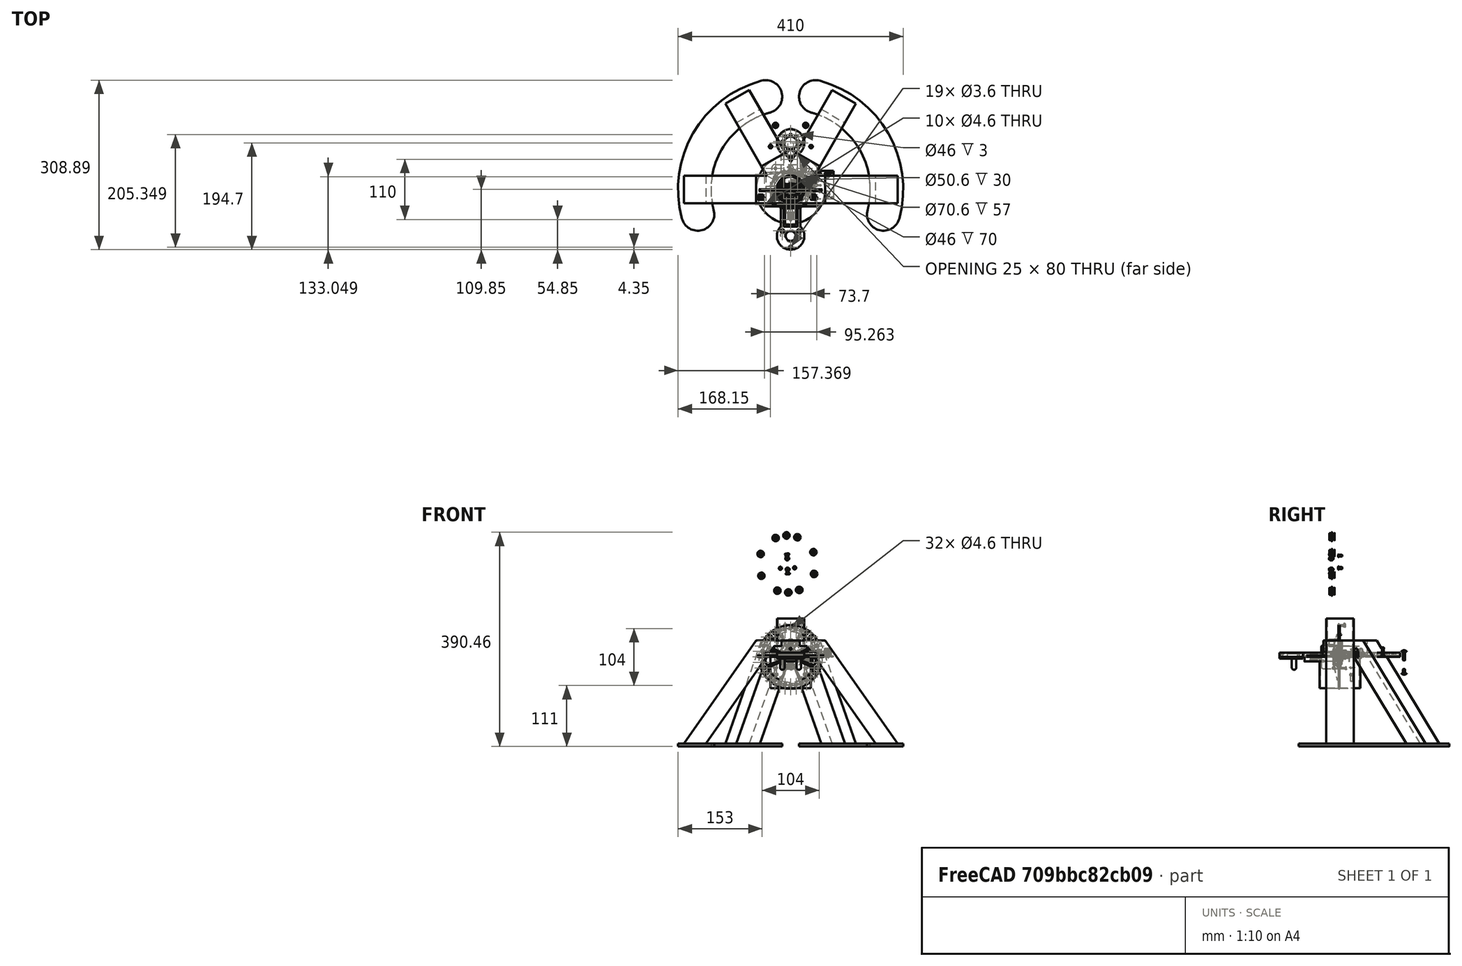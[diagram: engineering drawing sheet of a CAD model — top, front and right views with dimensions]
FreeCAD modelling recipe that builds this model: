
FCSTD DOCUMENT  (FreeCAD 1.1R44227 +568 (Git))
Label: assembly_Pendulum
License: All rights reserved
LicenseURL: https://en.wikipedia.org/wiki/All_rights_reserved
objects: Part::Feature×169, App::Point×115, App::Part×100, Sketcher::SketchObject×56, Part::FeaturePython×51, PartDesign::Pad×36, PartDesign::CoordinateSystem×29, PartDesign::Pocket×18, App::Link×17, PartDesign::Body×15, Mesh::Feature×9, PartDesign::Fillet×8, PartDesign::PolarPattern×7, App::DocumentObjectGroup×5, PartDesign::Chamfer×4, App::FeaturePython×1, PartDesign::Revolution×1, PartDesign::Hole×1
note: 594 computed .brp shape members not serialized (recipe doc carries the construction recipe); baked Part::Feature solids carry a one-line shape summary decoded from their .brp

FEATURE [PartDesign::CoordinateSystem] LCS_Origin
  AttacherType = Attacher::AttachEngine3D
  AttachmentSupport = -> [X_Axis]
  MapMode = 2
FEATURE [App::DocumentObjectGroup] Constraints
FEATURE [App::FeaturePython] Variables  # WARN: FeaturePython — macro-defined, semantics opaque (R4)
  Type = App::PropertyContainer
  arm_rotation = 2
FEATURE [App::DocumentObjectGroup] Configurations
FEATURE [Sketcher::SketchObject] Sketch
  ArcFitTolerance = 1e-06
  AttachmentSupport = -> [XZ_Plane001]
  ExternalTypes = [0]
  FullyConstrained = true
  MakeInternals = false
  MapMode = 5
  Placement = pos=(0,0,0) rot=(1,0,0;1.5708rad)
  _ExternalGeoVersion = 0
  sketch-geometry (13):
    g0: LineSegment StartX=5.6759 StartY=30.0968 StartZ=0 EndX=23.0689 EndY=6 EndZ=0
    g1: LineSegment StartX=23.0689 StartY=6 StartZ=0 EndX=34 EndY=6 EndZ=0
    g2: LineSegment StartX=34 StartY=6 StartZ=0 EndX=34 EndY=0 EndZ=0
    g3: LineSegment StartX=34 StartY=0 StartZ=0 EndX=20 EndY=0 EndZ=0
    g4: LineSegment StartX=20 StartY=0 StartZ=0 EndX=4.86567 EndY=20.9676 EndZ=0
    g5: LineSegment StartX=-4.86567 StartY=20.9676 StartZ=0 EndX=-20 EndY=0 EndZ=0
    g6: LineSegment StartX=-20 StartY=0 StartZ=0 EndX=-34 EndY=0 EndZ=0
    g7: LineSegment StartX=-34 StartY=0 StartZ=0 EndX=-34 EndY=6 EndZ=0
    g8: LineSegment StartX=-34 StartY=6 StartZ=0 EndX=-23.0689 EndY=6 EndZ=0
    g9: LineSegment StartX=-23.0689 StartY=6 StartZ=0 EndX=-5.6759 EndY=30.0968 EndZ=0
    g10: Circle CenterX=-1e-16 CenterY=26 CenterZ=0 NormalX=0 NormalY=0 NormalZ=1 AngleXU=0 Radius=2.8
    g11: ArcOfCircle CenterX=-1e-16 CenterY=26 CenterZ=0 NormalX=0 NormalY=0 NormalZ=1 AngleXU=0 Radius=7 StartAngle=0.625205 EndAngle=2.51639
    g12: ArcOfCircle CenterX=-1e-16 CenterY=26 CenterZ=0 NormalX=0 NormalY=0 NormalZ=1 AngleXU=0 Radius=7 StartAngle=3.94384 EndAngle=5.48094
  constraints (36):
    c: Coincident(g0,g1)
    c: Horizontal(g1)
    c: Coincident(g1,g2)
    c: PointOnObject(g2,g-1)
    c: Coincident(g2,g3)
    c: PointOnObject(g3,g-1)
    c: Coincident(g3,g4)
    c: Coincident(g5,g6)
    c: PointOnObject(g6,g-1)
    c: Coincident(g6,g7)
    c: Vertical(g7)
    c: Coincident(g7,g8)
    c: Horizontal(g8)
    c: Coincident(g8,g9)
    c: Symmetric(g9,g0,g-2)
    c: Parallel(g9,g5)
    c: Parallel(g0,g4)
    c: Vertical(g2)
    c: Equal(g7,g2)
    c: DistanceY(g7,g7) = 6
    c: Equal(g8,g1)
    c: DistanceX(g6,g6) = 14
    c: DistanceX(g5,g3) = 40
    c: Diameter(g10) = 5.6
    c: Coincident(g11,g10)
    c: Coincident(g11,g0)
    c: Equal(g11,g12)
    c: Coincident(g11,g12)
    c: Coincident(g4,g12)
    c: Coincident(g5,g12)
    c: DistanceY(g-1,g10) = 26
    c: Distance(g5,g9) = 6
    c: Distance(g4,g0) = 6
    c: Tangent(g9,g11) = 1.5708
    c: Diameter(g11) = 14
    c: Symmetric(g5,g3,g-2)
FEATURE [PartDesign::Pad] Pad  label="Pad_Main"
  Direction = (0,-1,2e-16)
  Length = 10
  Length2 = 10
  Placement = pos=(0,0,0) rot=(1,0,0;1.5708rad)
  Profile = -> Sketch
  ReferenceAxis = -> Sketch [N_Axis]
  Refine = true
  SideType = 0
  Suppressed = false
  Type = 0
  Type2 = 0
FEATURE [Sketcher::SketchObject] Sketch001
  ArcFitTolerance = 1e-06
  AttachmentSupport = -> [Pad]
  ExternalGeometry = -> [Pad]
  ExternalTypes = [0]
  FullyConstrained = true
  MakeInternals = false
  MapMode = 5
  Placement = pos=(0,-10,0) rot=(1,0,0;1.5708rad)
  _ExternalGeoVersion = 0
  sketch-geometry (2):
    g0: Circle CenterX=0 CenterY=26 CenterZ=0 NormalX=0 NormalY=0 NormalZ=1 AngleXU=0 Radius=3.8
    g1: Circle CenterX=0 CenterY=26 CenterZ=0 NormalX=0 NormalY=0 NormalZ=1 AngleXU=0 Radius=2.8
  constraints (4):
    c: Coincident(g0,g-3)
    c: Coincident(g1,g0)
    c: Diameter(g1) = 5.6
    c: Diameter(g0) = 7.6
FEATURE [PartDesign::Pad] Pad001  label="Pad_Shaft"
  BaseFeature = -> Pad
  Direction = (0,-1,2e-16)
  Length = 16.6
  Length2 = 10
  Placement = pos=(0,0,0) rot=(1,0,0;1.5708rad)
  Profile = -> Sketch001
  ReferenceAxis = -> Sketch001 [N_Axis]
  Refine = true
  SideType = 0
  Suppressed = false
  Type = 0
  Type2 = 0
FEATURE [Sketcher::SketchObject] Sketch002
  ArcFitTolerance = 1e-06
  AttachmentSupport = -> [Pad001]
  ExternalGeometry = -> [Pad001]
  ExternalTypes = [0]
  FullyConstrained = true
  MakeInternals = false
  MapMode = 5
  Placement = pos=(0,-10,0) rot=(1,0,0;1.5708rad)
  _ExternalGeoVersion = 0
  sketch-geometry (2):
    g0: Circle CenterX=0 CenterY=26 CenterZ=0 NormalX=0 NormalY=0 NormalZ=1 AngleXU=0 Radius=3.8
    g1: Circle CenterX=0 CenterY=26 CenterZ=0 NormalX=0 NormalY=0 NormalZ=1 AngleXU=0 Radius=6.5
  constraints (4):
    c: Coincident(g0,g-3)
    c: Equal(g0,g-3)
    c: Coincident(g1,g0)
    c: Diameter(g1) = 13
FEATURE [PartDesign::Pad] Pad002  label="Pad_Thrust"
  BaseFeature = -> Pad001
  Direction = (0,-1,2e-16)
  Length = 10
  Length2 = 10
  Placement = pos=(0,0,0) rot=(1,0,0;1.5708rad)
  Profile = -> Sketch002
  ReferenceAxis = -> Sketch002 [N_Axis]
  Refine = true
  SideType = 0
  Suppressed = false
  Type = 0
  Type2 = 0
FEATURE [Sketcher::SketchObject] Sketch003
  ArcFitTolerance = 1e-06
  AttachmentSupport = -> [Pad002]
  ExternalTypes = [0]
  FullyConstrained = true
  MakeInternals = false
  MapMode = 5
  Placement = pos=(0,2.9e-15,0) rot=(-1,0,0;1.5708rad)
  _ExternalGeoVersion = 0
  sketch-geometry (7):
    g0: LineSegment StartX=-4.8 StartY=-26 StartZ=0 EndX=-2.4 EndY=-30.1569 EndZ=0
    g1: LineSegment StartX=-2.4 StartY=-30.1569 StartZ=0 EndX=2.4 EndY=-30.1569 EndZ=0
    g2: LineSegment StartX=2.4 StartY=-30.1569 StartZ=0 EndX=4.8 EndY=-26 EndZ=0
    g3: LineSegment StartX=4.8 StartY=-26 StartZ=0 EndX=2.4 EndY=-21.8431 EndZ=0
    g4: LineSegment StartX=2.4 StartY=-21.8431 StartZ=0 EndX=-2.4 EndY=-21.8431 EndZ=0
    g5: LineSegment StartX=-2.4 StartY=-21.8431 StartZ=0 EndX=-4.8 EndY=-26 EndZ=0
    g6: Circle [constr] CenterX=0 CenterY=-26 CenterZ=0 NormalX=0 NormalY=0 NormalZ=1 AngleXU=0 Radius=4.8
  constraints (16):
    c: Coincident(g0,g1)
    c: Coincident(g1,g2)
    c: Coincident(g2,g3)
    c: Coincident(g3,g4)
    c: Coincident(g4,g5)
    c: Coincident(g5,g0)
    c: Equal(g0, g1-g5) x5
    c: PointOnObject(g0,g6)
    c: PointOnObject(g1,g6)
    c: PointOnObject(g2,g6)
    c: PointOnObject(g3,g6)
    c: PointOnObject(g4,g6)
    c: PointOnObject(g5,g6)
    c: Coincident(g6,g-3)
    c: Horizontal(g4)
    c: Diameter(g6) = 9.6
FEATURE [PartDesign::Pocket] Pocket
  BaseFeature = -> Pad002
  Direction = (0,-1,-2e-16)
  Length = 3
  Length2 = 5
  Placement = pos=(0,0,0) rot=(1,0,0;1.5708rad)
  Profile = -> Sketch003
  ReferenceAxis = -> Sketch003 [N_Axis]
  Refine = true
  SideType = 0
  Suppressed = false
  Type = 0
  Type2 = 0
FEATURE [Sketcher::SketchObject] Sketch005  label="Sketch_section"
  ArcFitTolerance = 0
  AttachmentSupport = -> [XZ_Plane003]
  ExternalTypes = [0]
  FullyConstrained = true
  MakeInternals = false
  MapMode = 5
  Placement = pos=(0,0,0) rot=(1,0,0;1.5708rad)
  _ExternalGeoVersion = 0
  sketch-geometry (12):
    g0: LineSegment StartX=4 StartY=-3.5 StartZ=0 EndX=6.5 EndY=-3.5 EndZ=0
    g1: LineSegment StartX=11 StartY=-3.5 StartZ=0 EndX=11 EndY=3.5 EndZ=0
    g2: LineSegment StartX=11 StartY=3.5 StartZ=0 EndX=9.25 EndY=3.5 EndZ=0
    g3: LineSegment StartX=4 StartY=3.5 StartZ=0 EndX=4 EndY=-3.5 EndZ=0
    g4: LineSegment StartX=6.5 StartY=3.5 StartZ=0 EndX=6.75 EndY=3.25 EndZ=0
    g5: LineSegment StartX=6.75 StartY=3.25 StartZ=0 EndX=9 EndY=3.25 EndZ=0
    g6: LineSegment StartX=9 StartY=3.25 StartZ=0 EndX=9.25 EndY=3.5 EndZ=0
    g7: LineSegment StartX=6.5 StartY=-3.5 StartZ=0 EndX=6.75 EndY=-3.25 EndZ=0
    g8: LineSegment StartX=6.75 StartY=-3.25 StartZ=0 EndX=9 EndY=-3.25 EndZ=0
    g9: LineSegment StartX=9 StartY=-3.25 StartZ=0 EndX=9.25 EndY=-3.5 EndZ=0
    g10: LineSegment StartX=6.5 StartY=3.5 StartZ=0 EndX=4 EndY=3.5 EndZ=0
    g11: LineSegment StartX=9.25 StartY=-3.5 StartZ=0 EndX=11 EndY=-3.5 EndZ=0
  constraints (33):
    c: Coincident(g11,g1)
    c: Coincident(g1,g2)
    c: Coincident(g10,g3)
    c: Coincident(g3,g0)
    c: Horizontal(g0)
    c: Horizontal(g2)
    c: Vertical(g1)
    c: DistanceY(g1) = 7
    c: DistanceX(g0) = 4
    c: DistanceX(g11) = 11
    c: Coincident(g4,g5)
    c: Horizontal(g5)
    c: Coincident(g5,g6)
    c: Coincident(g7,g8)
    c: Horizontal(g8)
    c: Coincident(g8,g9)
    c: Coincident(g2,g6)
    c: Coincident(g10,g4)
    c: Tangent(g2,g10)
    c: Coincident(g0,g7)
    c: Coincident(g11,g9)
    c: Tangent(g0,g11)
    c: Equal(g4,g6)
    c: Equal(g6,g7)
    c: Angle(g10,g4) = 2.35619
    c: DistanceX(g2) = -1.75
    c: DistanceX(g10) = -2.5
    c: Equal(g0,g10)
    c: Equal(g11,g2)
    c: Equal(g9,g7)
    c: Parallel(g9,g4)
    c: DistanceY(g5,g1) = 0.25
    c: Symmetric(g0,g3,g-1)
FEATURE [PartDesign::Revolution] Revolution
  Angle = 360
  Angle2 = 60
  Axis = (0,2e-16,1)
  Base = (0,0,0)
  FuseOrder = 1
  Placement = pos=(0,0,0) rot=(1,0,0;1.5708rad)
  Profile = -> Sketch005
  ReferenceAxis = -> Sketch005 [V_Axis]
  Refine = true
  Suppressed = false
  Type = 0
FEATURE [PartDesign::Chamfer] Chamfer
  Angle = 45
  Base = -> Revolution [Edge12,Edge11]
  BaseFeature = -> Revolution
  ChamferType = 0
  FlipDirection = false
  Placement = pos=(0,0,0) rot=(1,0,0;1.5708rad)
  Refine = true
  Size = 0.25
  Size2 = 1
  SupportTransform = false
  Suppressed = false
  UseAllEdges = false
FEATURE [PartDesign::CoordinateSystem] Bearing_Axis
  AttacherType = Attacher::AttachEngine3D
  AttachmentSupport = -> [Chamfer]
  MapMode = 45
  Placement = pos=(1.89e-14,1.7e-15,3.5) rot=(0,0,1;0rad)
FEATURE [PartDesign::Body] Body002  label="Body_Bearing"
  AllowCompound = false
  Group = -> [Sketch005,Revolution,Chamfer,Bearing_Axis]
  Origin = -> Origin003
  Tip = -> Chamfer
FEATURE [Sketcher::SketchObject] Sketch006
  ArcFitTolerance = 1e-06
  AttachmentSupport = -> [XY_Plane004]
  ExternalTypes = [0]
  FullyConstrained = true
  MakeInternals = false
  MapMode = 5
  _ExternalGeoVersion = 0
  sketch-geometry (1):
    g0: Circle CenterX=0 CenterY=84.85 CenterZ=0 NormalX=0 NormalY=0 NormalZ=1 AngleXU=0 Radius=23
  constraints (3):
    c: PointOnObject(g0,g-2)
    c: DistanceY(g-1,g0) = 84.85
    c: Diameter(g0) = 46
FEATURE [Sketcher::SketchObject] Sketch007
  ArcFitTolerance = 1e-06
  AttachmentSupport = -> [XY_Plane004]
  ExternalTypes = [0]
  FullyConstrained = true
  MakeInternals = false
  MapMode = 5
  _ExternalGeoVersion = 0
  sketch-geometry (33):
    g0: LineSegment StartX=-18 StartY=67.5 StartZ=0 EndX=-18 EndY=-67.5 EndZ=0
    g1: LineSegment StartX=18 StartY=-67.5 StartZ=0 EndX=18 EndY=67.5 EndZ=0
    g2: ArcOfCircle CenterX=0 CenterY=84.8494 CenterZ=0 NormalX=0 NormalY=0 NormalZ=1 AngleXU=0 Radius=25 StartAngle=5.51619 EndAngle=10.1918
    g3: Circle CenterX=0 CenterY=84.8494 CenterZ=0 NormalX=0 NormalY=0 NormalZ=1 AngleXU=0 Radius=11.5
    g4: Circle CenterX=0 CenterY=99.8494 CenterZ=0 NormalX=0 NormalY=0 NormalZ=1 AngleXU=0 Radius=1.8
    g5: Circle CenterX=9.64181 CenterY=96.34 CenterZ=0 NormalX=0 NormalY=0 NormalZ=1 AngleXU=0 Radius=1.8
    g6: Circle CenterX=14.7721 CenterY=87.4541 CenterZ=0 NormalX=0 NormalY=0 NormalZ=1 AngleXU=0 Radius=1.8
    g7: Circle CenterX=12.9904 CenterY=77.3494 CenterZ=0 NormalX=0 NormalY=0 NormalZ=1 AngleXU=0 Radius=1.8
    g8: Circle CenterX=5.1303 CenterY=70.754 CenterZ=0 NormalX=0 NormalY=0 NormalZ=1 AngleXU=0 Radius=1.8
    g9: Circle CenterX=-5.1303 CenterY=70.754 CenterZ=0 NormalX=0 NormalY=0 NormalZ=1 AngleXU=0 Radius=1.8
    g10: Circle CenterX=-12.9904 CenterY=77.3494 CenterZ=0 NormalX=0 NormalY=0 NormalZ=1 AngleXU=0 Radius=1.8
    g11: Circle CenterX=-14.7721 CenterY=87.4541 CenterZ=0 NormalX=0 NormalY=0 NormalZ=1 AngleXU=0 Radius=1.8
    g12: Circle CenterX=-9.64181 CenterY=96.34 CenterZ=0 NormalX=0 NormalY=0 NormalZ=1 AngleXU=0 Radius=1.8
    g13: LineSegment [constr] StartX=-9.64181 StartY=96.34 StartZ=0 EndX=0 EndY=84.8494 EndZ=0
    g14: LineSegment [constr] StartX=-14.7721 StartY=87.4541 StartZ=0 EndX=0 EndY=84.8494 EndZ=0
    g15: LineSegment [constr] StartX=-12.9904 StartY=77.3494 StartZ=0 EndX=0 EndY=84.8494 EndZ=0
    g16: LineSegment [constr] StartX=-5.1303 StartY=70.754 StartZ=0 EndX=0 EndY=84.8494 EndZ=0
    g17: LineSegment [constr] StartX=5.1303 StartY=70.754 StartZ=0 EndX=0 EndY=84.8494 EndZ=0
    g18: LineSegment [constr] StartX=12.9904 StartY=77.3494 StartZ=0 EndX=0 EndY=84.8494 EndZ=0
    g19: LineSegment [constr] StartX=14.7721 StartY=87.4541 StartZ=0 EndX=0 EndY=84.8494 EndZ=0
    g20: LineSegment [constr] StartX=9.64181 StartY=96.34 StartZ=0 EndX=0 EndY=84.8494 EndZ=0
    g21: Circle CenterX=-7.78 CenterY=-27 CenterZ=0 NormalX=0 NormalY=0 NormalZ=1 AngleXU=0 Radius=1.8
    g22: Circle CenterX=7.78 CenterY=-27 CenterZ=0 NormalX=0 NormalY=0 NormalZ=1 AngleXU=0 Radius=1.8
    g23: ArcOfCircle CenterX=0 CenterY=-84.8494 CenterZ=0 NormalX=0 NormalY=0 NormalZ=1 AngleXU=0 Radius=25 StartAngle=2.3746 EndAngle=7.05018
    g24: Circle CenterX=0 CenterY=-84.8494 CenterZ=0 NormalX=0 NormalY=0 NormalZ=1 AngleXU=0 Radius=11.25
    g25: LineSegment StartX=-12.5 StartY=63.1987 StartZ=0 EndX=-12.5 EndY=-16.8013 EndZ=0
    g26: LineSegment StartX=-12.5 StartY=-16.8013 StartZ=0 EndX=12.5 EndY=-16.8013 EndZ=0
    g27: LineSegment StartX=12.5 StartY=-16.8013 StartZ=0 EndX=12.5 EndY=63.1987 EndZ=0
    g28: LineSegment StartX=-12.5 StartY=-33.5 StartZ=0 EndX=-12.5 EndY=-67.5 EndZ=0
    g29: LineSegment StartX=-12.5 StartY=-67.5 StartZ=0 EndX=12.5 EndY=-67.5 EndZ=0
    g30: LineSegment StartX=12.5 StartY=-67.5 StartZ=0 EndX=12.5 EndY=-33.5 EndZ=0
    g31: LineSegment StartX=12.5 StartY=-33.5 StartZ=0 EndX=-12.5 EndY=-33.5 EndZ=0
    g32: ArcOfCircle CenterX=0 CenterY=84.8494 CenterZ=0 NormalX=0 NormalY=0 NormalZ=1 AngleXU=0 Radius=25 StartAngle=4.18879 EndAngle=5.23599
  constraints (88):
    c: Vertical(g0)
    c: Vertical(g1)
    c: Symmetric(g0,g1,g-1)
    c: DistanceX(g0,g1) = 36
    c: DistanceY(g1,g1) = 135
    c: PointOnObject(g2,g-2)
    c: Diameter(g2) = 50
    c: Coincident(g2,g0)
    c: Coincident(g2,g1)
    c: Coincident(g3,g2)
    c: Diameter(g3) = 23
    c: PointOnObject(g4,g-2)
    c: Coincident(g13,g12)
    c: Coincident(g13,g2)
    c: Coincident(g14,g11)
    c: Coincident(g14,g2)
    c: Coincident(g15,g10)
    c: Coincident(g15,g2)
    c: Coincident(g16,g9)
    c: Coincident(g16,g2)
    c: Coincident(g17,g8)
    c: Coincident(g17,g2)
    c: Coincident(g18,g7)
    c: Coincident(g18,g2)
    c: Coincident(g19,g6)
    c: Coincident(g19,g2)
    c: Coincident(g20,g5)
    c: Coincident(g20,g2)
    c: Equal(g4,g5)
    c: Equal(g5,g6)
    c: Equal(g6,g7)
    c: Equal(g7,g8)
    c: Equal(g8,g9)
    c: Equal(g9,g10)
    c: Equal(g10,g11)
    c: Equal(g11,g12)
    c: Equal(g13,g14)
    c: Equal(g14,g15)
    c: Equal(g15,g16)
    c: Equal(g16,g17)
    c: Equal(g17,g18)
    c: Equal(g18,g19)
    c: Equal(g19,g20)
    c: DistanceY(g2,g4) = 15
    c: Distance(g13) = 15
    c: Diameter(g4) = 3.6
    c: Angle(g-2,g20) = 2.44346
    c: Angle(g19,g20) = 0.698132
    c: Angle(g18,g19) = 0.698132
    c: Angle(g17,g18) = 0.698132
    c: Angle(g16,g17) = 0.698132
    c: Angle(g15,g16) = 0.698132
    c: Angle(g14,g15) = 0.698132
    c: Angle(g13,g14) = 0.698132
    c: Equal(g22,g21)
    c: Diameter(g21) = 3.6
    c: DistanceX(g21,g22) = 15.56
    c: Symmetric(g21,g22,g-2)
    c: DistanceY(g22,g-1) = 27
    c: PointOnObject(g23,g-2)
    c: Diameter(g23) = 50
    c: Coincident(g23,g1)
    c: Coincident(g23,g0)
    c: Coincident(g24,g23)
    c: Diameter(g24) = 22.5
    c: Vertical(g25)
    c: Vertical(g27)
    c: Horizontal(g26)
    c: Coincident(g28,g29)
    c: Coincident(g29,g30)
    c: Coincident(g30,g31)
    c: Coincident(g31,g28)
    c: Vertical(g28)
    c: Vertical(g30)
    c: Horizontal(g29)
    c: Symmetric(g27,g25,g-2)
    c: DistanceY(g25,g25) = 80
    c: DistanceX(g25,g27) = 25
    c: PointOnObject(g1,g29)
    c: Symmetric(g28,g30,g-2)
    c: DistanceX(g31,g31) = 25
    c: DistanceY(g28,g28) = 34
    c: Diameter(g32) = 50
    c: Coincident(g32,g25)
    c: Coincident(g32,g27)
    c: Coincident(g32,g2)
    c: Coincident(g26,g25)
    c: Coincident(g27,g26)
FEATURE [PartDesign::Pad] Pad004  label="Pad_Arm"
  Direction = (0,0,1)
  Length = 8
  Length2 = 10
  Profile = -> Sketch007
  ReferenceAxis = -> Sketch007 [N_Axis]
  Refine = true
  SideType = 0
  Suppressed = false
  Type = 0
  Type2 = 0
FEATURE [PartDesign::Pocket] Pocket001  label="Pocket_Motor"
  BaseFeature = -> Pad004
  Direction = (0,0,-1)
  Length = 3
  Length2 = 5
  Profile = -> Sketch006
  ReferenceAxis = -> Sketch006 [N_Axis]
  Refine = true
  Reversed = true
  SideType = 0
  Suppressed = false
  Type = 0
  Type2 = 0
FEATURE [PartDesign::CoordinateSystem] Arm_Axis_Top
  AttacherType = Attacher::AttachEngine3D
  AttachmentOffset = pos=(0,0,0) rot=(0,0,-1;1.5708rad)
  AttachmentSupport = -> [Pocket001]
  MapMode = 11
  Placement = pos=(2e-16,99.8494,8) rot=(0,0,1;0rad)
FEATURE [Sketcher::SketchObject] Sketch008
  ArcFitTolerance = 1e-06
  AttachmentSupport = -> [XZ_Plane005]
  ExternalTypes = [0]
  FullyConstrained = true
  MakeInternals = false
  MapMode = 5
  Placement = pos=(0,0,0) rot=(1,0,0;1.5708rad)
  _ExternalGeoVersion = 0
  sketch-geometry (8):
    g0: LineSegment StartX=-3.7 StartY=11.6 StartZ=0 EndX=-3.7 EndY=8 EndZ=0
    g1: LineSegment StartX=-3.7 StartY=8 StartZ=0 EndX=3.7 EndY=8 EndZ=0
    g2: LineSegment StartX=3.7 StartY=8 StartZ=0 EndX=3.7 EndY=11.6 EndZ=0
    g3: LineSegment StartX=3.7 StartY=11.6 StartZ=0 EndX=-3.7 EndY=11.6 EndZ=0
    g4: LineSegment StartX=-3.7 StartY=-8 StartZ=0 EndX=-3.7 EndY=-11.6 EndZ=0
    g5: LineSegment StartX=-3.7 StartY=-11.6 StartZ=0 EndX=3.7 EndY=-11.6 EndZ=0
    g6: LineSegment StartX=3.7 StartY=-11.6 StartZ=0 EndX=3.7 EndY=-8 EndZ=0
    g7: LineSegment StartX=3.7 StartY=-8 StartZ=0 EndX=-3.7 EndY=-8 EndZ=0
  constraints (21):
    c: Coincident(g0,g1)
    c: Coincident(g1,g2)
    c: Coincident(g2,g3)
    c: Coincident(g3,g0)
    c: Vertical(g0)
    c: Vertical(g2)
    c: Coincident(g4,g5)
    c: Coincident(g5,g6)
    c: Coincident(g6,g7)
    c: Coincident(g7,g4)
    c: Vertical(g4)
    c: Vertical(g6)
    c: Horizontal(g5)
    c: Horizontal(g7)
    c: Symmetric(g0,g6,g-1)
    c: DistanceY(g-1,g1) = 8
    c: DistanceY(g2,g2) = 3.6
    c: DistanceX(g3,g3) = 7.4
    c: Symmetric(g2,g4,g-1)
    c: Symmetric(g1,g0,g-2)
    c: Horizontal(g3)
FEATURE [Sketcher::SketchObject] Sketch009
  ArcFitTolerance = 1e-06
  AttachmentSupport = -> [XY_Plane005]
  ExternalTypes = [0]
  FullyConstrained = true
  MakeInternals = false
  MapMode = 5
  _ExternalGeoVersion = 0
  sketch-geometry (1):
    g0: Circle CenterX=0 CenterY=-6 CenterZ=0 NormalX=0 NormalY=0 NormalZ=1 AngleXU=0 Radius=2.25
  constraints (3):
    c: PointOnObject(g0,g-2)
    c: Diameter(g0) = 4.5
    c: DistanceY(g0,g-1) = 6
FEATURE [Sketcher::SketchObject] Sketch010
  ArcFitTolerance = 1e-06
  AttachmentOffset = pos=(0,0,0) rot=(1,0,0;0.392699rad)
  AttachmentSupport = -> [YZ_Plane005]
  ExternalTypes = [0]
  FullyConstrained = true
  MakeInternals = false
  MapMode = 5
  Placement = pos=(0,0,0) rot=(0.639338,0.639338,0.427192;2.33414rad)
  _ExternalGeoVersion = 0
  sketch-geometry (4):
    g0: LineSegment StartX=-3 StartY=14.5 StartZ=0 EndX=-12 EndY=14.5 EndZ=0
    g1: LineSegment StartX=-12 StartY=14.5 StartZ=0 EndX=-5 EndY=44.5 EndZ=0
    g2: LineSegment StartX=-5 StartY=44.5 StartZ=0 EndX=-3 EndY=44.5 EndZ=0
    g3: LineSegment StartX=-3 StartY=44.5 StartZ=0 EndX=-3 EndY=14.5 EndZ=0
  constraints (12):
    c: Coincident(g0,g1)
    c: Coincident(g1,g2)
    c: Horizontal(g2)
    c: Coincident(g2,g3)
    c: Coincident(g3,g0)
    c: Horizontal(g0)
    c: Vertical(g3)
    c: DistanceX(g0,g-1) = 3
    c: DistanceY(g-1,g0) = 14.5
    c: DistanceY(g3,g3) = 30
    c: DistanceX(g2,g2) = 2
    c: DistanceX(g0,g0) = 9
FEATURE [Sketcher::SketchObject] Sketch011
  ArcFitTolerance = 1e-06
  AttachmentSupport = -> [XZ_Plane005]
  ExternalTypes = [0]
  FullyConstrained = true
  MakeInternals = false
  MapMode = 5
  Placement = pos=(0,0,0) rot=(1,0,0;1.5708rad)
  _ExternalGeoVersion = 0
  sketch-geometry (1):
    g0: Circle CenterX=0 CenterY=52 CenterZ=0 NormalX=0 NormalY=0 NormalZ=1 AngleXU=0 Radius=2.3
  constraints (3):
    c: PointOnObject(g0,g-2)
    c: Diameter(g0) = 4.6
    c: DistanceY(g-1,g0) = 52
FEATURE [Sketcher::SketchObject] Sketch012
  ArcFitTolerance = 1e-06
  AttachmentSupport = -> [XZ_Plane005]
  ExternalTypes = [0]
  FullyConstrained = true
  MakeInternals = false
  MapMode = 5
  Placement = pos=(0,0,0) rot=(1,0,0;1.5708rad)
  _ExternalGeoVersion = 0
  sketch-geometry (5):
    g0: LineSegment StartX=0 StartY=0 StartZ=0 EndX=-1.04189 EndY=5.90885 EndZ=0
    g1: LineSegment StartX=-1.04189 StartY=5.90885 StartZ=0 EndX=-0.2 EndY=5.3692 EndZ=0
    g2: LineSegment StartX=-0.2 StartY=5.3692 StartZ=0 EndX=0.2 EndY=5.3692 EndZ=0
    g3: LineSegment StartX=0.2 StartY=5.3692 StartZ=0 EndX=1.04189 EndY=5.90885 EndZ=0
    g4: LineSegment StartX=1.04189 StartY=5.90885 StartZ=0 EndX=0 EndY=0 EndZ=0
  constraints (13):
    c: Coincident(g-1,g0)
    c: Coincident(g0,g1)
    c: Coincident(g1,g2)
    c: Horizontal(g2)
    c: Coincident(g2,g3)
    c: Coincident(g3,g4)
    c: Coincident(g4,g0)
    c: Symmetric(g3,g0,g-2)
    c: Angle(g4,g0) = 0.349066
    c: DistanceX(g2,g2) = 0.4
    c: Distance(g4) = 6
    c: Distance(g3) = 1
    c: Distance(g1) = 1
FEATURE [Sketcher::SketchObject] Sketch013
  ArcFitTolerance = 1e-06
  AttachmentSupport = -> [XZ_Plane005]
  ExternalTypes = [0]
  FullyConstrained = true
  MakeInternals = false
  MapMode = 5
  Placement = pos=(0,0,0) rot=(1,0,0;1.5708rad)
  _ExternalGeoVersion = 0
  sketch-geometry (2):
    g0: Circle CenterX=0 CenterY=0 CenterZ=0 NormalX=0 NormalY=0 NormalZ=1 AngleXU=0 Radius=5
    g1: Circle CenterX=0 CenterY=0 CenterZ=0 NormalX=0 NormalY=0 NormalZ=1 AngleXU=0 Radius=15
  constraints (4):
    c: Coincident(g0,g-1)
    c: Coincident(g1,g0)
    c: Diameter(g1) = 30
    c: Diameter(g0) = 10
FEATURE [Sketcher::SketchObject] Sketch014
  ArcFitTolerance = 1e-06
  AttachmentSupport = -> [XZ_Plane005]
  ExternalTypes = [0]
  FullyConstrained = true
  MakeInternals = false
  MapMode = 5
  Placement = pos=(0,0,0) rot=(1,0,0;1.5708rad)
  _ExternalGeoVersion = 0
  sketch-geometry (6):
    g0: ArcOfCircle CenterX=0 CenterY=0 CenterZ=0 NormalX=0 NormalY=0 NormalZ=1 AngleXU=0 Radius=15 StartAngle=1.23918 EndAngle=1.90241
    g1: ArcOfCircle CenterX=0 CenterY=0 CenterZ=0 NormalX=0 NormalY=0 NormalZ=1 AngleXU=0 Radius=46 StartAngle=1.23918 EndAngle=1.90241
    g2: LineSegment [constr] StartX=0 StartY=0 StartZ=0 EndX=-19.5341 EndY=56.7311 EndZ=0
    g3: LineSegment [constr] StartX=0 StartY=0 StartZ=0 EndX=19.5341 EndY=56.7311 EndZ=0
    g4: LineSegment StartX=-4.88352 StartY=14.1828 StartZ=0 EndX=-14.9761 EndY=43.4939 EndZ=0
    g5: LineSegment StartX=14.9761 StartY=43.4939 StartZ=0 EndX=4.88352 EndY=14.1828 EndZ=0
  constraints (17):
    c: Coincident(g0,g-1)
    c: Coincident(g1,g0)
    c: Coincident(g2,g0)
    c: Coincident(g3,g0)
    c: Coincident(g4,g0)
    c: Coincident(g4,g1)
    c: Coincident(g5,g1)
    c: Coincident(g5,g0)
    c: Symmetric(g2,g3,g-2)
    c: Angle(g3,g2) = 0.663225
    c: PointOnObject(g0,g3)
    c: PointOnObject(g1,g3)
    c: PointOnObject(g0,g2)
    c: PointOnObject(g1,g2)
    c: Diameter(g1) = 92
    c: Diameter(g0) = 30
    c: Distance(g3) = 60
FEATURE [Sketcher::SketchObject] Sketch015
  ArcFitTolerance = 1e-06
  AttachmentSupport = -> [XZ_Plane005]
  ExternalTypes = [0]
  FullyConstrained = true
  MakeInternals = false
  MapMode = 5
  Placement = pos=(0,0,0) rot=(1,0,0;1.5708rad)
  _ExternalGeoVersion = 0
  sketch-geometry (2):
    g0: Circle CenterX=0 CenterY=0 CenterZ=0 NormalX=0 NormalY=0 NormalZ=1 AngleXU=0 Radius=58
    g1: Circle CenterX=0 CenterY=0 CenterZ=0 NormalX=0 NormalY=0 NormalZ=1 AngleXU=0 Radius=5
  constraints (4):
    c: Coincident(g0,g-1)
    c: Diameter(g0) = 116
    c: Coincident(g1,g0)
    c: Diameter(g1) = 10
FEATURE [PartDesign::Pad] Pad005  label="Pad_External"
  Direction = (0,-1,2e-16)
  Length = 3
  Length2 = 10
  Placement = pos=(0,0,0) rot=(1,0,0;1.5708rad)
  Profile = -> Sketch015
  ReferenceAxis = -> Sketch015 [N_Axis]
  Refine = true
  SideType = 0
  Suppressed = false
  Type = 0
  Type2 = 0
FEATURE [PartDesign::Pocket] Pocket002  label="Pocket_Gap"
  BaseFeature = -> Pad005
  Direction = (0,1,-2e-16)
  Length = 5
  Length2 = 5
  Placement = pos=(0,0,0) rot=(1,0,0;1.5708rad)
  Profile = -> Sketch014
  ReferenceAxis = -> Sketch014 [N_Axis]
  Refine = true
  Reversed = true
  SideType = 0
  Suppressed = false
  Type = 0
  Type2 = 0
FEATURE [PartDesign::PolarPattern] PolarPattern  label="PolarPattern_Gaps"
  Angle = 360
  Axis = -> Sketch014 [N_Axis]
  BaseFeature = -> Pocket002
  Mode = 0
  Occurrences = 8
  Offset = 120
  Originals = -> [Pocket002]
  Placement = pos=(0,0,0) rot=(1,0,0;1.5708rad)
  Refine = true
  SpacingPattern = [0]
  Spacings = [-1,-1,-1,-1,-1,-1,-1]
  Suppressed = false
  TransformMode = 0
FEATURE [PartDesign::Pad] Pad006  label="Pad_Center"
  BaseFeature = -> PolarPattern
  Direction = (0,-1,2e-16)
  Length = 12
  Length2 = 10
  Placement = pos=(0,0,0) rot=(1,0,0;1.5708rad)
  Profile = -> Sketch013
  ReferenceAxis = -> Sketch013 [N_Axis]
  Refine = true
  SideType = 0
  Suppressed = false
  Type = 0
  Type2 = 0
FEATURE [PartDesign::Pocket] Pocket003  label="Pocket_Shaft"
  BaseFeature = -> Pad006
  Direction = (0,1,-2e-16)
  Length = 5
  Length2 = 5
  Placement = pos=(0,0,0) rot=(1,0,0;1.5708rad)
  Profile = -> Sketch012
  ReferenceAxis = -> Sketch012 [N_Axis]
  Refine = true
  Reversed = true
  SideType = 0
  Suppressed = false
  Type = 1
  Type2 = 0
FEATURE [PartDesign::PolarPattern] PolarPattern001  label="PolarPattern_DriveShaft"
  Angle = 360
  Axis = -> Sketch012 [N_Axis]
  BaseFeature = -> Pocket003
  Mode = 0
  Occurrences = 18
  Offset = 120
  Originals = -> [Pocket003]
  Placement = pos=(0,0,0) rot=(1,0,0;1.5708rad)
  Refine = true
  SpacingPattern = [0]
  Spacings = [-1,-1,-1,-1,-1,-1,-1,-1,-1,-1,-1,-1,-1,-1,-1,-1,-1]
  Suppressed = false
  TransformMode = 0
FEATURE [PartDesign::Pocket] Pocket004  label="Pocket_Screw"
  BaseFeature = -> PolarPattern001
  Direction = (0,1,-2e-16)
  Length = 5
  Length2 = 5
  Placement = pos=(0,0,0) rot=(1,0,0;1.5708rad)
  Profile = -> Sketch011
  ReferenceAxis = -> Sketch011 [N_Axis]
  Refine = true
  Reversed = true
  SideType = 0
  Suppressed = false
  Type = 1
  Type2 = 0
FEATURE [PartDesign::PolarPattern] PolarPattern002  label="PolarPattern_Inertia"
  Angle = 360
  Axis = -> Sketch011 [N_Axis]
  BaseFeature = -> Pocket004
  Mode = 0
  Occurrences = 32
  Offset = 120
  Originals = -> [Pocket004]
  Placement = pos=(0,0,0) rot=(1,0,0;1.5708rad)
  Refine = true
  SpacingPattern = [0]
  Spacings = [-1,-1,-1,-1,-1,-1,-1,-1,-1,-1,-1,-1,-1,-1,-1,-1,-1,-1,-1,-1,-1,-1,-1,-1,-1,-1,-1,-1,-1,-1,-1]
  Suppressed = false
  TransformMode = 0
FEATURE [PartDesign::Pad] Pad007  label="Pad_Reinforcement"
  BaseFeature = -> PolarPattern002
  Direction = (0.92388,0,-0.382683)
  Length = 2
  Length2 = 10
  Placement = pos=(0,0,0) rot=(1,0,0;1.5708rad)
  Profile = -> Sketch010
  ReferenceAxis = -> Sketch010 [N_Axis]
  Refine = true
  SideType = 2
  Suppressed = false
  Type = 0
  Type2 = 0
FEATURE [PartDesign::PolarPattern] PolarPattern003  label="PolarPattern_Reinforcements"
  Angle = 360
  Axis = -> Y_Axis005
  BaseFeature = -> Pad007
  Mode = 0
  Occurrences = 8
  Offset = 120
  Originals = -> [Pad007]
  Placement = pos=(0,0,0) rot=(1,0,0;1.5708rad)
  Refine = true
  SpacingPattern = [0]
  Spacings = [-1,-1,-1,-1,-1,-1,-1]
  Suppressed = false
  TransformMode = 0
FEATURE [PartDesign::Pocket] Pocket005  label="Pocket_Fixation"
  BaseFeature = -> PolarPattern003
  Direction = (0,0,-1)
  Length = 30
  Length2 = 5
  Placement = pos=(0,0,0) rot=(1,0,0;1.5708rad)
  Profile = -> Sketch009
  ReferenceAxis = -> Sketch009 [N_Axis]
  Refine = true
  SideType = 2
  Suppressed = false
  Type = 0
  Type2 = 0
FEATURE [PartDesign::Pocket] Pocket006  label="Pocket_Bolts"
  BaseFeature = -> Pocket005
  Direction = (0,1,-2e-16)
  Length = 12
  Length2 = 5
  Placement = pos=(0,0,0) rot=(1,0,0;1.5708rad)
  Profile = -> Sketch008
  ReferenceAxis = -> Sketch008 [N_Axis]
  Refine = true
  Reversed = true
  SideType = 0
  Suppressed = false
  Type = 0
  Type2 = 0
FEATURE [Sketcher::SketchObject] Sketch016
  ArcFitTolerance = 1e-06
  AttachmentSupport = -> [XY_Plane006]
  ExternalTypes = [0]
  FullyConstrained = true
  MakeInternals = false
  MapMode = 5
  _ExternalGeoVersion = 0
  sketch-geometry (8):
    g0: LineSegment StartX=-7.5 StartY=-8 StartZ=0 EndX=-7.5 EndY=-13 EndZ=0
    g1: LineSegment StartX=7.5 StartY=-13 StartZ=0 EndX=7.5 EndY=-8 EndZ=0
    g2: LineSegment StartX=7.5 StartY=-8 StartZ=0 EndX=-7.5 EndY=-8 EndZ=0
    g3: LineSegment StartX=-10 StartY=-13 StartZ=0 EndX=-10 EndY=-14.2 EndZ=0
    g4: LineSegment StartX=-10 StartY=-14.2 StartZ=0 EndX=10 EndY=-14.2 EndZ=0
    g5: LineSegment StartX=10 StartY=-14.2 StartZ=0 EndX=10 EndY=-13 EndZ=0
    g6: LineSegment StartX=10 StartY=-13 StartZ=0 EndX=7.5 EndY=-13 EndZ=0
    g7: LineSegment StartX=-7.5 StartY=-13 StartZ=0 EndX=-10 EndY=-13 EndZ=0
  constraints (21):
    c: Coincident(g1,g2)
    c: Coincident(g2,g0)
    c: Vertical(g0)
    c: Coincident(g3,g4)
    c: Coincident(g4,g5)
    c: Coincident(g5,g6)
    c: Coincident(g7,g3)
    c: Vertical(g3)
    c: Vertical(g5)
    c: Horizontal(g6)
    c: Coincident(g6,g1)
    c: Coincident(g0,g7)
    c: Symmetric(g0,g1,g-2)
    c: Symmetric(g3,g4,g-2)
    c: Symmetric(g0,g1,g-2)
    c: DistanceX(g2,g2) = 15
    c: DistanceX(g4,g4) = 20
    c: DistanceY(g3,g3) = 1.2
    c: Horizontal(g7)
    c: DistanceY(g0,g0) = 5
    c: DistanceY(g0,g-1) = 8
FEATURE [Sketcher::SketchObject] Sketch017
  ArcFitTolerance = 1e-06
  AttachmentOffset = pos=(0,0,42) rot=(0,0,1;0rad)
  AttachmentSupport = -> [XZ_Plane006]
  ExternalTypes = [0]
  FullyConstrained = true
  MakeInternals = false
  MapMode = 5
  Placement = pos=(0,-42,9.3e-15) rot=(1,0,0;1.5708rad)
  _ExternalGeoVersion = 0
  sketch-geometry (5):
    g0: LineSegment StartX=-0.955065 StartY=5.41644 StartZ=0 EndX=0 EndY=0 EndZ=0
    g1: LineSegment StartX=0.955065 StartY=5.41644 StartZ=0 EndX=0 EndY=0 EndZ=0
    g2: LineSegment StartX=-0.955065 StartY=5.41644 StartZ=0 EndX=-0.2 EndY=4.76079 EndZ=0
    g3: LineSegment StartX=-0.2 StartY=4.76079 StartZ=0 EndX=0.2 EndY=4.76079 EndZ=0
    g4: LineSegment StartX=0.2 StartY=4.76079 StartZ=0 EndX=0.955065 EndY=5.41644 EndZ=0
  constraints (12):
    c: Coincident(g0,g-1)
    c: Coincident(g1,g0)
    c: Coincident(g3,g2)
    c: Coincident(g4,g3)
    c: Coincident(g4,g1)
    c: Symmetric(g3,g2,g-2)
    c: Coincident(g2,g0)
    c: Symmetric(g0,g1,g-2)
    c: Angle(g1,g0) = 0.349066
    c: DistanceX(g3,g3) = 0.4
    c: Distance(g1) = 5.5
    c: Distance(g4) = 1
FEATURE [Sketcher::SketchObject] Sketch018
  ArcFitTolerance = 1e-06
  AttachmentSupport = -> [XZ_Plane006]
  ExternalTypes = [0]
  FullyConstrained = true
  MakeInternals = false
  MapMode = 5
  Placement = pos=(0,0,0) rot=(1,0,0;1.5708rad)
  _ExternalGeoVersion = 0
  sketch-geometry (1):
    g0: Circle CenterX=0 CenterY=0 CenterZ=0 NormalX=0 NormalY=0 NormalZ=1 AngleXU=0 Radius=21
  constraints (2):
    c: Coincident(g0,g-1)
    c: Diameter(g0) = 42
FEATURE [PartDesign::Pad] Pad008  label="Pad_Cylinder"
  Direction = (0,-1,2e-16)
  Length = 34
  Length2 = 10
  Placement = pos=(0,0,0) rot=(1,0,0;1.5708rad)
  Profile = -> Sketch018
  ReferenceAxis = -> Sketch018 [N_Axis]
  Refine = true
  SideType = 0
  Suppressed = false
  Type = 0
  Type2 = 0
FEATURE [Sketcher::SketchObject] Sketch019
  ArcFitTolerance = 1e-06
  AttachmentSupport = -> [Pad008]
  ExternalTypes = [0]
  FullyConstrained = true
  MakeInternals = false
  MapMode = 5
  Placement = pos=(0,-34,0) rot=(1,0,0;1.5708rad)
  _ExternalGeoVersion = 0
  sketch-geometry (1):
    g0: Circle CenterX=0 CenterY=0 CenterZ=0 NormalX=0 NormalY=0 NormalZ=1 AngleXU=0 Radius=7.5
  constraints (2):
    c: Coincident(g0,g-1)
    c: Diameter(g0) = 15
FEATURE [PartDesign::Pad] Pad009  label="Pad_Bearing"
  BaseFeature = -> Pad008
  Direction = (0,-1,2e-16)
  Length = 1.2
  Length2 = 10
  Placement = pos=(0,0,0) rot=(1,0,0;1.5708rad)
  Profile = -> Sketch019
  ReferenceAxis = -> Sketch019 [N_Axis]
  Refine = true
  SideType = 0
  Suppressed = false
  Type = 0
  Type2 = 0
FEATURE [Sketcher::SketchObject] Sketch020
  ArcFitTolerance = 1e-06
  AttachmentSupport = -> [Pad009]
  ExternalTypes = [0]
  FullyConstrained = true
  MakeInternals = false
  MapMode = 5
  Placement = pos=(0,-35.2,0) rot=(1,0,0;1.5708rad)
  _ExternalGeoVersion = 0
  sketch-geometry (1):
    g0: Circle CenterX=0 CenterY=0 CenterZ=0 NormalX=0 NormalY=0 NormalZ=1 AngleXU=0 Radius=3
  constraints (2):
    c: Coincident(g0,g-1)
    c: Diameter(g0) = 6
FEATURE [PartDesign::Pad] Pad010  label="Pad_Drive_Shaft"
  BaseFeature = -> Pad009
  Direction = (0,-1,2e-16)
  Length = 6.4
  Length2 = 10
  Placement = pos=(0,0,0) rot=(1,0,0;1.5708rad)
  Profile = -> Sketch020
  ReferenceAxis = -> Sketch020 [N_Axis]
  Refine = true
  SideType = 0
  Suppressed = false
  Type = 0
  Type2 = 0
FEATURE [Sketcher::SketchObject] Sketch021
  ArcFitTolerance = 1e-06
  AttachmentSupport = -> [Pad010]
  ExternalTypes = [0]
  FullyConstrained = true
  MakeInternals = false
  MapMode = 5
  Placement = pos=(0,-41.6,0) rot=(1,0,0;1.5708rad)
  _ExternalGeoVersion = 0
  sketch-geometry (1):
    g0: Circle CenterX=0 CenterY=0 CenterZ=0 NormalX=0 NormalY=0 NormalZ=1 AngleXU=0 Radius=7.5
  constraints (2):
    c: Coincident(g0,g-1)
    c: Diameter(g0) = 15
FEATURE [PartDesign::Pad] Pad011  label="Pad_Thrust001"
  BaseFeature = -> Pad010
  Direction = (0,-1,2e-16)
  Length = 1.3
  Length2 = 10
  Placement = pos=(0,0,0) rot=(1,0,0;1.5708rad)
  Profile = -> Sketch021
  ReferenceAxis = -> Sketch021 [N_Axis]
  Refine = true
  SideType = 0
  Suppressed = false
  Type = 0
  Type2 = 0
FEATURE [PartDesign::Pad] Pad012  label="Pad_Tooth"
  BaseFeature = -> Pad011
  Direction = (0,-1,2e-16)
  Length = 12
  Length2 = 10
  Placement = pos=(0,0,0) rot=(1,0,0;1.5708rad)
  Profile = -> Sketch017
  ReferenceAxis = -> Sketch017 [N_Axis]
  Refine = true
  SideType = 0
  Suppressed = false
  Type = 0
  Type2 = 0
FEATURE [PartDesign::PolarPattern] PolarPattern004  label="PolarPattern_Shaft"
  Angle = 360
  Axis = -> Sketch017 [N_Axis]
  BaseFeature = -> Pad012
  Mode = 0
  Occurrences = 18
  Offset = 120
  Originals = -> [Pad012]
  Placement = pos=(0,0,0) rot=(1,0,0;1.5708rad)
  Refine = true
  SpacingPattern = [0]
  Spacings = [-1,-1,-1,-1,-1,-1,-1,-1,-1,-1,-1,-1,-1,-1,-1,-1,-1]
  Suppressed = false
  TransformMode = 0
FEATURE [Sketcher::SketchObject] Sketch022
  ArcFitTolerance = 1e-06
  AttachmentSupport = -> [PolarPattern004]
  ExternalTypes = [0]
  FullyConstrained = true
  MakeInternals = false
  MapMode = 5
  Placement = pos=(0,-34,0) rot=(1,0,0;1.5708rad)
  _ExternalGeoVersion = 0
  sketch-geometry (1):
    g0: Circle CenterX=0 CenterY=15 CenterZ=0 NormalX=0 NormalY=0 NormalZ=1 AngleXU=0 Radius=1.75
  constraints (3):
    c: PointOnObject(g0,g-2)
    c: Diameter(g0) = 3.5
    c: DistanceY(g-1,g0) = 15
FEATURE [PartDesign::Pocket] Pocket007  label="Pocket_Screw001"
  BaseFeature = -> PolarPattern004
  Direction = (0,1,-2e-16)
  Length = 5
  Length2 = 5
  Placement = pos=(0,0,0) rot=(1,0,0;1.5708rad)
  Profile = -> Sketch022
  ReferenceAxis = -> Sketch022 [N_Axis]
  Refine = true
  SideType = 0
  Suppressed = false
  Type = 0
  Type2 = 0
FEATURE [PartDesign::PolarPattern] PolarPattern005  label="PolarPattern_Fixations"
  Angle = 360
  Axis = -> Sketch022 [N_Axis]
  BaseFeature = -> Pocket007
  Mode = 0
  Occurrences = 3
  Offset = 120
  Originals = -> [Pocket007]
  Placement = pos=(0,0,0) rot=(1,0,0;1.5708rad)
  Refine = true
  SpacingPattern = [0]
  Spacings = [-1,-1]
  Suppressed = false
  TransformMode = 0
FEATURE [PartDesign::Pad] Pad013  label="Pad_Connector"
  BaseFeature = -> PolarPattern005
  Direction = (0,0,1)
  Length = 22
  Length2 = 10
  Placement = pos=(0,0,0) rot=(1,0,0;1.5708rad)
  Profile = -> Sketch016
  ReferenceAxis = -> Sketch016 [N_Axis]
  Refine = true
  Reversed = true
  SideType = 0
  Suppressed = false
  Type = 0
  Type2 = 0
FEATURE [Sketcher::SketchObject] Sketch023
  ArcFitTolerance = 1e-06
  AttachmentSupport = -> [Pad013]
  ExternalGeometry = -> [Pad013]
  ExternalTypes = [0]
  FullyConstrained = true
  MakeInternals = false
  MapMode = 5
  Placement = pos=(0,0,-22) rot=(1,0,0;3.14159rad)
  _ExternalGeoVersion = 0
  sketch-geometry (4):
    g0: LineSegment StartX=-6.5 StartY=12 StartZ=0 EndX=-6.5 EndY=9 EndZ=0
    g1: LineSegment StartX=-6.5 StartY=9 StartZ=0 EndX=6.5 EndY=9 EndZ=0
    g2: LineSegment StartX=6.5 StartY=9 StartZ=0 EndX=6.5 EndY=12 EndZ=0
    g3: LineSegment StartX=6.5 StartY=12 StartZ=0 EndX=-6.5 EndY=12 EndZ=0
  constraints (12):
    c: Coincident(g0,g1)
    c: Coincident(g1,g2)
    c: Coincident(g2,g3)
    c: Coincident(g3,g0)
    c: Vertical(g0)
    c: Vertical(g2)
    c: Horizontal(g1)
    c: Horizontal(g3)
    c: DistanceX(g-3,g0) = 1
    c: DistanceX(g1,g-4) = 1
    c: DistanceY(g-4,g1) = 1
    c: DistanceY(g0,g-3) = 1
FEATURE [PartDesign::Pocket] Pocket008  label="Pocket_Pins"
  BaseFeature = -> Pad013
  Direction = (0,0,1)
  Length = 5
  Length2 = 5
  Placement = pos=(0,0,0) rot=(1,0,0;1.5708rad)
  Profile = -> Sketch023
  ReferenceAxis = -> Sketch023 [N_Axis]
  Refine = true
  SideType = 0
  Suppressed = false
  Type = 0
  Type2 = 0
FEATURE [PartDesign::Fillet] Fillet001  label="Fillet_Cylinder"
  Base = -> Pocket008 [Edge3,Edge1]
  BaseFeature = -> Pocket008
  Placement = pos=(0,0,0) rot=(1,0,0;1.5708rad)
  Radius = 3
  Refine = true
  SupportTransform = false
  Suppressed = false
  UseAllEdges = false
FEATURE [PartDesign::Fillet] Fillet002  label="Fillet_Thrust_Bearing"
  Base = -> Fillet001 [Edge61,Edge43]
  BaseFeature = -> Fillet001
  Placement = pos=(0,0,0) rot=(1,0,0;1.5708rad)
  Radius = 1
  Refine = true
  SupportTransform = false
  Suppressed = false
  UseAllEdges = false
FEATURE [PartDesign::CoordinateSystem] Motor
  AttacherType = Attacher::AttachEngine3D
  AttachmentOffset = pos=(0,0,0) rot=(-0.57735,0.57735,-0.57735;2.0944rad)
  AttachmentSupport = -> [Fillet002]
  MapMode = 11
  Placement = pos=(0,-34,15) rot=(0,0,1;0rad)
FEATURE [PartDesign::Chamfer] Chamfer001
  Angle = 45
  Base = -> Pocket006 [Edge336,Edge335,Edge334,Edge333,Edge315,Edge311,Edge310,Edge292,Edge291,Edge284,Edge285,Edge283,Edge286,Edge287,Edge296,Edge297,Edge298,Edge299,Edge300,Edge301,Edge305,Edge309,Edge342,Edge343,Edge344,Edge351,Edge350,Edge352,Edge349,Edge348,Edge338,Edge337]
  BaseFeature = -> Pocket006
  ChamferType = 0
  FlipDirection = true
  Placement = pos=(0,0,0) rot=(1,0,0;1.5708rad)
  Refine = true
  Size = 1.5
  Size2 = 1
  SupportTransform = false
  Suppressed = false
  UseAllEdges = false
FEATURE [PartDesign::CoordinateSystem] reactionWheel
  AttacherType = Attacher::AttachEngine3D
  AttachmentOffset = pos=(0,0,0) rot=(-0.57735,0.57735,-0.57735;2.0944rad)
  AttachmentSupport = -> [Chamfer001]
  MapMode = 11
  Placement = pos=(0,-12,5.3e-15) rot=(0,0,1;0rad)
FEATURE [PartDesign::Body] Body004  label="Body_ReactionWheel"
  AllowCompound = false
  Group = -> [Sketch015,Pad005,Sketch014,Pocket002,PolarPattern,Sketch013,Pad006,Sketch012,Pocket003,PolarPattern001,Sketch011,Pocket004,PolarPattern002,Sketch010,Pad007,PolarPattern003,Sketch009,Pocket005,Sketch008,Pocket006,reactionWheel,Chamfer001]
  Origin = -> Origin005
  Tip = -> Chamfer001
FEATURE [PartDesign::CoordinateSystem] Support
  AttacherType = Attacher::AttachEngine3D
  AttachmentOffset = pos=(0,0,0) rot=(-0.57735,0.57735,-0.57735;2.0944rad)
  AttachmentSupport = -> [Pocket]
  MapMode = 11
  Placement = pos=(0,-26.6,26) rot=(0,0,1;0rad)
FEATURE [App::Link] Body_Support  label="Body_Support001"
  AttachedBy = #Support
  AttachedTo = Parent Assembly#LCS_Origin
  Description = Pendulum
  LinkPlacement = pos=(0,26.6,-26) rot=(0,0,1;0rad)
  LinkedObject = -> Body
  Placement = pos=(0,26.6,-26) rot=(0,0,1;0rad)
  SolverId = Asm4EE
  expr: Placement = LCS_Origin.Placement * AttachmentOffset * Support.Placement ^ -1
FEATURE [App::Link] Body_Bearing  label="Body_Bearing001"
  AttachedBy = #Bearing_Axis
  AttachedTo = Body_Support#Support
  AttachmentOffset = pos=(0,-1,0) rot=(1,0,0;1.5708rad)
  LinkPlacement = pos=(-2.99e-14,2.5,-7.4e-15) rot=(1,0,0;1.5708rad)
  LinkedObject = -> Body002
  Placement = pos=(-2.99e-14,2.5,-7.4e-15) rot=(1,0,0;1.5708rad)
  SolverId = Asm4EE
  expr: Placement = Body_Support.Placement * Support.Placement * AttachmentOffset * Bearing_Axis.Placement ^ -1
FEATURE [PartDesign::CoordinateSystem] Rondelle001
  AttacherType = Attacher::AttachEngine3D
  AttachmentOffset = pos=(0,0,0) rot=(-0.57735,0.57735,-0.57735;2.0944rad)
  MapMode = 11
  Placement = pos=(0,-20.2,26) rot=(0,0,1;0rad)
FEATURE [PartDesign::Body] Body001  label="Body_Rondelle"
  AllowCompound = false
  Group = -> [Rondelle001]
  Origin = -> Origin007
FEATURE [App::Link] Body_Rondelle  label="Body_Rondelle001"
  AttachedBy = #Rondelle001
  AttachedTo = Body_Bearing#Bearing_Axis
  AttachmentOffset = pos=(0,0,0.5) rot=(1,0,0;1.5708rad)
  LinkPlacement = pos=(-3.38e-14,-21.7,26) rot=(1,0,0;3.14159rad)
  LinkedObject = -> Body001
  Placement = pos=(-3.38e-14,-21.7,26) rot=(1,0,0;3.14159rad)
  SolverId = Asm4EE
  expr: Placement = Body_Bearing.Placement * Bearing_Axis.Placement * AttachmentOffset * Rondelle001.Placement ^ -1
FEATURE [App::Link] Body_Arm  label="Body_Arm001"
  AttachedBy = #Arm_Axis_Bottom
  AttachedTo = Body_Bearing#Bearing_Axis
  AttachmentOffset = pos=(0,0,1) rot=(0,0,1;0.034907rad)
  LinkPlacement = pos=(-2.9612,6,84.7977) rot=(0.999695,-0.01745,0.01745;1.5711rad)
  LinkedObject = -> Body003
  Placement = pos=(-2.9612,6,84.7977) rot=(0.999695,-0.01745,0.01745;1.5711rad)
  SolverId = Asm4EE
  expr: .AttachmentOffset.Rotation.Angle = Variables.arm_rotation
  expr: Placement = Body_Bearing.Placement * Bearing_Axis.Placement * AttachmentOffset * Arm_Axis_Bottom.Placement ^ -1
FEATURE [App::Link] Body_Motor  label="Body_Motor001"
  AttachedBy = #Motor
  AttachedTo = Body_Arm#Arm_Axis_Top
  AttachmentOffset = pos=(0,0,-2) rot=(1,0,0;4.71239rad)
  LinkPlacement = pos=(-5.9224,34,169.595) rot=(0,1,0;6.24828rad)
  LinkedObject = -> Body005
  Placement = pos=(-5.9224,34,169.595) rot=(0,1,0;6.24828rad)
  SolverId = Asm4EE
  expr: Placement = Body_Arm.Placement * Arm_Axis_Top.Placement * AttachmentOffset * Motor.Placement ^ -1
FEATURE [App::Link] Body_ReactionWheel  label="Body_ReactionWheel001"
  AttachedBy = #reactionWheel
  AttachedTo = Body_Motor#Motor_Shaft001
  AttachmentOffset = pos=(0,-13,0) rot=(0,0,1;0rad)
  LinkPlacement = pos=(-5.9224,-9.9,169.595) rot=(0,1,0;6.24828rad)
  LinkedObject = -> Body004
  Placement = pos=(-5.9224,-9.9,169.595) rot=(0,1,0;6.24828rad)
  SolverId = Asm4EE
  expr: Placement = Body_Motor.Placement * Motor_Shaft001.Placement * AttachmentOffset * reactionWheel.Placement ^ -1
FEATURE [PartDesign::CoordinateSystem] Motor_Shaft
  AttacherType = Attacher::AttachEngine3D
  AttachmentSupport = -> [Fillet002]
  MapMode = 11
  Placement = pos=(0,-42.9,9.5e-15) rot=(0.57735,-0.57735,0.57735;2.0944rad)
FEATURE [PartDesign::CoordinateSystem] Motor_Shaft001
  AttacherType = Attacher::AttachEngine3D
  AttachmentOffset = pos=(0,0,0) rot=(-0.57735,0.57735,-0.57735;2.0944rad)
  AttachmentSupport = -> [Fillet002]
  MapMode = 11
  Placement = pos=(0,-42.9,9.5e-15) rot=(0,0,1;0rad)
FEATURE [PartDesign::Body] Body005  label="Body_Motor"
  AllowCompound = false
  Group = -> [Sketch018,Pad008,Sketch019,Pad009,Sketch020,Pad010,Sketch021,Pad011,Sketch017,Pad012,PolarPattern004,Sketch022,Pocket007,PolarPattern005,Sketch016,Pad013,Sketch023,Pocket008,Fillet001,Fillet002,Motor,Motor_Shaft001]
  Origin = -> Origin006
  Tip = -> Fillet002
FEATURE [Sketcher::SketchObject] Sketch024
  ArcFitTolerance = 1e-06
  AttachmentSupport = -> [XZ_Plane008]
  ExternalTypes = [0]
  FullyConstrained = true
  MakeInternals = false
  MapMode = 5
  Placement = pos=(0,0,0) rot=(1,0,0;1.5708rad)
  _ExternalGeoVersion = 0
  sketch-geometry (76):
    g0: LineSegment StartX=-8.94 StartY=-2.15 StartZ=0 EndX=-11.04 EndY=-2.15 EndZ=0
    g1: LineSegment StartX=-11.04 StartY=-2.15 StartZ=0 EndX=-11.04 EndY=-3.15 EndZ=0
    g2: LineSegment StartX=-11.04 StartY=-3.15 StartZ=0 EndX=-8.94 EndY=-3.15 EndZ=0
    g3: LineSegment StartX=-8.94 StartY=-3.15 StartZ=0 EndX=-8.94 EndY=-2.15 EndZ=0
    g4: LineSegment StartX=-8.94 StartY=-3.65 StartZ=0 EndX=-11.04 EndY=-3.65 EndZ=0
    g5: LineSegment StartX=-11.04 StartY=-3.65 StartZ=0 EndX=-11.04 EndY=-4.65 EndZ=0
    g6: LineSegment StartX=-11.04 StartY=-4.65 StartZ=0 EndX=-8.94 EndY=-4.65 EndZ=0
    g7: LineSegment StartX=-8.94 StartY=-4.65 StartZ=0 EndX=-8.94 EndY=-3.65 EndZ=0
    g8: LineSegment StartX=-8.94 StartY=-5.15 StartZ=0 EndX=-11.04 EndY=-5.15 EndZ=0
    g9: LineSegment StartX=-11.04 StartY=-5.15 StartZ=0 EndX=-11.04 EndY=-6.15 EndZ=0
    g10: LineSegment StartX=-11.04 StartY=-6.15 StartZ=0 EndX=-8.94 EndY=-6.15 EndZ=0
    g11: LineSegment StartX=-8.94 StartY=-6.15 StartZ=0 EndX=-8.94 EndY=-5.15 EndZ=0
    g12: LineSegment StartX=-5.34 StartY=-3.65 StartZ=0 EndX=-7.44 EndY=-3.65 EndZ=0
    g13: LineSegment StartX=-7.44 StartY=-3.65 StartZ=0 EndX=-7.44 EndY=-4.65 EndZ=0
    g14: LineSegment StartX=-7.44 StartY=-4.65 StartZ=0 EndX=-5.34 EndY=-4.65 EndZ=0
    g15: LineSegment StartX=-5.34 StartY=-4.65 StartZ=0 EndX=-5.34 EndY=-3.65 EndZ=0
    g16: LineSegment StartX=-5.34 StartY=-5.15 StartZ=0 EndX=-7.44 EndY=-5.15 EndZ=0
    g17: LineSegment StartX=-7.44 StartY=-5.15 StartZ=0 EndX=-7.44 EndY=-6.15 EndZ=0
    g18: LineSegment StartX=-7.44 StartY=-6.15 StartZ=0 EndX=-5.34 EndY=-6.15 EndZ=0
    g19: LineSegment StartX=-5.34 StartY=-6.15 StartZ=0 EndX=-5.34 EndY=-5.15 EndZ=0
    g20: LineSegment StartX=-1.68 StartY=-9.16 StartZ=0 EndX=-3.06 EndY=-9.16 EndZ=0
    g21: LineSegment StartX=-3.06 StartY=-9.16 StartZ=0 EndX=-3.06 EndY=-13.54 EndZ=0
    g22: LineSegment StartX=-3.06 StartY=-13.54 StartZ=0 EndX=-1.68 EndY=-13.54 EndZ=0
    g23: LineSegment StartX=-1.68 StartY=-13.54 StartZ=0 EndX=-1.68 EndY=-9.16 EndZ=0
    g24: LineSegment StartX=-4.18 StartY=-6.8 StartZ=0 EndX=-11.54 EndY=-6.8 EndZ=0
    g25: LineSegment StartX=-11.54 StartY=-6.8 StartZ=0 EndX=-11.54 EndY=-14.14 EndZ=0
    g26: LineSegment StartX=-11.54 StartY=-14.14 StartZ=0 EndX=-4.18 EndY=-14.14 EndZ=0
    g27: LineSegment StartX=-4.18 StartY=-14.14 StartZ=0 EndX=-4.18 EndY=-6.8 EndZ=0
    g28: LineSegment StartX=-4 StartY=-15.5 StartZ=0 EndX=-7.4 EndY=-15.5 EndZ=0
    g29: LineSegment StartX=-7.4 StartY=-15.5 StartZ=0 EndX=-7.4 EndY=-15.96 EndZ=0
    g30: LineSegment StartX=-7.4 StartY=-15.96 StartZ=0 EndX=-4 EndY=-15.96 EndZ=0
    g31: LineSegment StartX=-4 StartY=-15.96 StartZ=0 EndX=-4 EndY=-15.5 EndZ=0
    g32: LineSegment StartX=-8.9 StartY=-15.5 StartZ=0 EndX=-12.3 EndY=-15.5 EndZ=0
    g33: LineSegment StartX=-12.3 StartY=-15.5 StartZ=0 EndX=-12.3 EndY=-15.96 EndZ=0
    g34: LineSegment StartX=-12.3 StartY=-15.96 StartZ=0 EndX=-8.9 EndY=-15.96 EndZ=0
    g35: LineSegment StartX=-8.9 StartY=-15.96 StartZ=0 EndX=-8.9 EndY=-15.5 EndZ=0
    g36: LineSegment StartX=-8.9 StartY=-16.11 StartZ=0 EndX=-12.3 EndY=-16.11 EndZ=0
    g37: LineSegment StartX=-12.3 StartY=-16.11 StartZ=0 EndX=-12.3 EndY=-16.81 EndZ=0
    g38: LineSegment StartX=-12.3 StartY=-16.81 StartZ=0 EndX=-8.9 EndY=-16.81 EndZ=0
    g39: LineSegment StartX=-8.9 StartY=-16.81 StartZ=0 EndX=-8.9 EndY=-16.11 EndZ=0
    g40: LineSegment StartX=-4 StartY=-16.11 StartZ=0 EndX=-7.4 EndY=-16.11 EndZ=0
    g41: LineSegment StartX=-7.4 StartY=-16.11 StartZ=0 EndX=-7.4 EndY=-16.81 EndZ=0
    g42: LineSegment StartX=-7.4 StartY=-16.81 StartZ=0 EndX=-4 EndY=-16.81 EndZ=0
    g43: LineSegment StartX=-4 StartY=-16.81 StartZ=0 EndX=-4 EndY=-16.11 EndZ=0
    g44: LineSegment StartX=-4.78 StartY=-17.8 StartZ=0 EndX=-5.58 EndY=-17.8 EndZ=0
    g45: LineSegment StartX=-5.58 StartY=-17.8 StartZ=0 EndX=-5.58 EndY=-20.1 EndZ=0
    g46: LineSegment StartX=-5.58 StartY=-20.1 StartZ=0 EndX=-4.78 EndY=-20.1 EndZ=0
    g47: LineSegment StartX=-4.78 StartY=-20.1 StartZ=0 EndX=-4.78 EndY=-17.8 EndZ=0
    g48: LineSegment StartX=-10.88 StartY=-17.8 StartZ=0 EndX=-11.68 EndY=-17.8 EndZ=0
    g49: LineSegment StartX=-11.68 StartY=-17.8 StartZ=0 EndX=-11.68 EndY=-20.1 EndZ=0
    g50: LineSegment StartX=-11.68 StartY=-20.1 StartZ=0 EndX=-10.88 EndY=-20.1 EndZ=0
    g51: LineSegment StartX=-10.88 StartY=-20.1 StartZ=0 EndX=-10.88 EndY=-17.8 EndZ=0
    g52: LineSegment StartX=-6.28 StartY=-17.8 StartZ=0 EndX=-6.73 EndY=-17.8 EndZ=0
    g53: LineSegment StartX=-6.73 StartY=-18.12 StartZ=0 EndX=-6.28 EndY=-18.12 EndZ=0
    g54: LineSegment StartX=-6.28 StartY=-18.12 StartZ=0 EndX=-6.28 EndY=-17.8 EndZ=0
    g55: LineSegment StartX=-6.28 StartY=-19.72 StartZ=0 EndX=-6.73 EndY=-19.72 EndZ=0
    g56: LineSegment StartX=-6.73 StartY=-20.04 StartZ=0 EndX=-6.28 EndY=-20.04 EndZ=0
    g57: LineSegment StartX=-6.28 StartY=-20.04 StartZ=0 EndX=-6.28 EndY=-19.72 EndZ=0
    g58: LineSegment StartX=-9.17 StartY=-17.915 StartZ=0 EndX=-9.95 EndY=-17.915 EndZ=0
    g59: LineSegment StartX=-9.95 StartY=-17.915 StartZ=0 EndX=-9.95 EndY=-18.275 EndZ=0
    g60: LineSegment StartX=-9.95 StartY=-18.275 StartZ=0 EndX=-9.17 EndY=-18.275 EndZ=0
    g61: LineSegment StartX=-9.17 StartY=-18.74 StartZ=0 EndX=-9.95 EndY=-18.74 EndZ=0
    g62: LineSegment StartX=-9.95 StartY=-18.74 StartZ=0 EndX=-9.95 EndY=-19.1 EndZ=0
    g63: LineSegment StartX=-9.95 StartY=-19.1 StartZ=0 EndX=-9.17 EndY=-19.1 EndZ=0
    g64: LineSegment StartX=-9.17 StartY=-19.565 StartZ=0 EndX=-9.95 EndY=-19.565 EndZ=0
    g65: LineSegment StartX=-9.95 StartY=-19.565 StartZ=0 EndX=-9.95 EndY=-19.925 EndZ=0
    g66: LineSegment StartX=-9.95 StartY=-19.925 StartZ=0 EndX=-9.17 EndY=-19.925 EndZ=0
    g67: LineSegment StartX=-6.73 StartY=-17.45 StartZ=0 EndX=-9.17 EndY=-17.45 EndZ=0
    g68: LineSegment StartX=-9.17 StartY=-17.45 StartZ=0 EndX=-9.17 EndY=-17.915 EndZ=0
    g69: LineSegment StartX=-9.17 StartY=-20.39 StartZ=0 EndX=-6.73 EndY=-20.39 EndZ=0
    g70: LineSegment StartX=-6.73 StartY=-20.39 StartZ=0 EndX=-6.73 EndY=-20.04 EndZ=0
    g71: LineSegment StartX=-6.73 StartY=-17.8 StartZ=0 EndX=-6.73 EndY=-17.45 EndZ=0
    g72: LineSegment StartX=-6.73 StartY=-19.72 StartZ=0 EndX=-6.73 EndY=-18.12 EndZ=0
    g73: LineSegment StartX=-9.17 StartY=-18.275 StartZ=0 EndX=-9.17 EndY=-18.74 EndZ=0
    g74: LineSegment StartX=-9.17 StartY=-19.1 StartZ=0 EndX=-9.17 EndY=-19.565 EndZ=0
    g75: LineSegment StartX=-9.17 StartY=-19.925 StartZ=0 EndX=-9.17 EndY=-20.39 EndZ=0
  constraints (228):
    c: Coincident(g0,g1)
    c: Coincident(g1,g2)
    c: Coincident(g2,g3)
    c: Coincident(g3,g0)
    c: Horizontal(g0)
    c: Horizontal(g2)
    c: Vertical(g1)
    c: Vertical(g3)
    c: Coincident(g4,g5)
    c: Coincident(g5,g6)
    c: Coincident(g6,g7)
    c: Coincident(g7,g4)
    c: Horizontal(g4)
    c: Horizontal(g6)
    c: Vertical(g5)
    c: Vertical(g7)
    c: Coincident(g8,g9)
    c: Coincident(g9,g10)
    c: Coincident(g10,g11)
    c: Coincident(g11,g8)
    c: Horizontal(g8)
    c: Horizontal(g10)
    c: Vertical(g9)
    c: Vertical(g11)
    c: Coincident(g12,g13)
    c: Coincident(g13,g14)
    c: Coincident(g14,g15)
    c: Coincident(g15,g12)
    c: Horizontal(g12)
    c: Horizontal(g14)
    c: Vertical(g13)
    c: Vertical(g15)
    c: Coincident(g16,g17)
    c: Coincident(g17,g18)
    c: Coincident(g18,g19)
    c: Coincident(g19,g16)
    c: Horizontal(g16)
    c: Horizontal(g18)
    c: Vertical(g17)
    c: Vertical(g19)
    c: Coincident(g20,g21)
    c: Coincident(g21,g22)
    c: Coincident(g22,g23)
    c: Coincident(g23,g20)
    c: Horizontal(g20)
    c: Horizontal(g22)
    c: Vertical(g21)
    c: Vertical(g23)
    c: Coincident(g24,g25)
    c: Coincident(g25,g26)
    c: Coincident(g26,g27)
    c: Coincident(g27,g24)
    c: Horizontal(g24)
    c: Horizontal(g26)
    c: Vertical(g25)
    c: Vertical(g27)
    c: Coincident(g28,g29)
    c: Coincident(g29,g30)
    c: Coincident(g30,g31)
    c: Coincident(g31,g28)
    c: Horizontal(g28)
    c: Horizontal(g30)
    c: Vertical(g29)
    c: Vertical(g31)
    c: Coincident(g32,g33)
    c: Coincident(g33,g34)
    c: Coincident(g34,g35)
    c: Coincident(g35,g32)
    c: Horizontal(g32)
    c: Horizontal(g34)
    c: Vertical(g33)
    c: Vertical(g35)
    c: Coincident(g36,g37)
    c: Coincident(g37,g38)
    c: Coincident(g38,g39)
    c: Coincident(g39,g36)
    c: Horizontal(g36)
    c: Horizontal(g38)
    c: Vertical(g37)
    c: Vertical(g39)
    c: Coincident(g40,g41)
    c: Coincident(g41,g42)
    c: Coincident(g42,g43)
    c: Coincident(g43,g40)
    c: Horizontal(g40)
    c: Horizontal(g42)
    c: Vertical(g41)
    c: Vertical(g43)
    c: Coincident(g44,g45)
    c: Coincident(g45,g46)
    c: Coincident(g46,g47)
    c: Coincident(g47,g44)
    c: Horizontal(g44)
    c: Horizontal(g46)
    c: Vertical(g45)
    c: Vertical(g47)
    c: Coincident(g48,g49)
    c: Coincident(g49,g50)
    c: Coincident(g50,g51)
    c: Coincident(g51,g48)
    c: Horizontal(g48)
    c: Horizontal(g50)
    c: Vertical(g49)
    c: Vertical(g51)
    c: Coincident(g53,g54)
    c: Coincident(g54,g52)
    c: Horizontal(g52)
    c: Horizontal(g53)
    c: Vertical(g54)
    c: Coincident(g56,g57)
    c: Coincident(g57,g55)
    c: Horizontal(g55)
    c: Horizontal(g56)
    c: Vertical(g57)
    c: Coincident(g58,g59)
    c: Coincident(g59,g60)
    c: Horizontal(g58)
    c: Horizontal(g60)
    c: Vertical(g59)
    c: Coincident(g61,g62)
    c: Coincident(g62,g63)
    c: Horizontal(g61)
    c: Horizontal(g63)
    c: Vertical(g62)
    c: Coincident(g64,g65)
    c: Coincident(g65,g66)
    c: Horizontal(g64)
    c: Horizontal(g66)
    c: Vertical(g65)
    c: Coincident(g67,g68)
    c: Coincident(g75,g69)
    c: Coincident(g69,g70)
    c: Coincident(g71,g67)
    c: Horizontal(g67)
    c: Horizontal(g69)
    c: Vertical(g68)
    c: Vertical(g70)
    c: Equal(g0,g4)
    c: Equal(g4,g8)
    c: Equal(g8,g16)
    c: Equal(g16,g12)
    c: Equal(g19,g11)
    c: Equal(g11,g15)
    c: Equal(g15,g7)
    c: Equal(g7,g3)
    c: DistanceX(g0,g0) = 2.1
    c: DistanceY(g1,g1) = 1
    c: DistanceX(g0,g-1) = 8.94
    c: DistanceX(g4,g12) = 1.5
    c: DistanceY(g4,g1) = 0.5
    c: DistanceY(g8,g5) = 0.5
    c: PointOnObject(g17,g10)
    c: PointOnObject(g13,g6)
    c: PointOnObject(g13,g17)
    c: PointOnObject(g6,g11)
    c: DistanceY(g0,g-1) = 2.15
    c: PointOnObject(g4,g3)
    c: DistanceX(g24,g24) = 7.36
    c: DistanceY(g27,g27) = 7.34
    c: DistanceX(g24,g-1) = 4.18
    c: DistanceY(g24,g-1) = 6.8
    c: DistanceX(g20,g20) = 1.38
    c: DistanceY(g23,g23) = 4.38
    c: DistanceX(g20,g-1) = 1.68
    c: DistanceY(g20,g-1) = 9.16
    c: Equal(g28,g40)
    c: Equal(g40,g32)
    c: Equal(g32,g36)
    c: Equal(g29,g35)
    c: Equal(g43,g39)
    c: PointOnObject(g30,g43)
    c: PointOnObject(g34,g39)
    c: PointOnObject(g40,g36)
    c: PointOnObject(g29,g34)
    c: DistanceX(g28,g28) = 3.4
    c: DistanceY(g31,g31) = 0.46
    c: DistanceY(g40,g30) = 0.15
    c: DistanceY(g43,g43) = 0.7
    c: DistanceX(g32,g28) = 1.5
    c: DistanceX(g28,g-1) = 4
    c: DistanceY(g28,g-1) = 15.5
    c: Equal(g44,g48)
    c: Equal(g47,g51)
    c: PointOnObject(g44,g48)
    c: DistanceX(g46,g46) = 0.8
    c: DistanceY(g47,g47) = 2.3
    c: DistanceX(g46,g-1) = 4.78
    c: DistanceY(g44,g-1) = 17.8
    c: DistanceX(g50,g45) = 5.3
    c: Coincident(g72,g55)
    c: Coincident(g56,g70)
    c: Vertical(g72)
    c: PointOnObject(g56,g72)
    c: Vertical(g71)
    c: Coincident(g72,g53)
    c: Coincident(g52,g71)
    c: Coincident(g58,g68)
    c: Coincident(g73,g60)
    c: Coincident(g61,g73)
    c: Coincident(g74,g63)
    c: Coincident(g64,g74)
    c: Coincident(g66,g75)
    c: Vertical(g74)
    c: Vertical(g75)
    c: PointOnObject(g58,g73)
    c: Vertical(g73)
    c: PointOnObject(g61,g74)
    c: PointOnObject(g64,g75)
    c: Equal(g58,g61)
    c: Equal(g61,g64)
    c: Equal(g59,g62)
    c: Equal(g62,g65)
    c: Equal(g52,g55)
    c: Equal(g54,g57)
    c: Equal(g71,g70)
    c: Equal(g68,g73)
    c: Equal(g73,g74)
    c: Equal(g74,g75)
    c: DistanceY(g71,g71) = 0.35
    c: DistanceY(g54,g54) = 0.32
    c: PointOnObject(g52,g72)
    c: DistanceX(g52,g52) = 0.45
    c: DistanceX(g53,g44) = 0.7
    c: DistanceY(g72,g72) = 1.6
    c: PointOnObject(g52,g44)
    c: DistanceX(g67,g67) = 2.44
    c: DistanceX(g58,g58) = 0.78
    c: DistanceY(g59,g59) = 0.36
FEATURE [Sketcher::SketchObject] Sketch025
  ArcFitTolerance = 1e-06
  AttachmentSupport = -> [XZ_Plane008]
  ExternalTypes = [0]
  FullyConstrained = true
  MakeInternals = false
  MapMode = 5
  Placement = pos=(0,0,0) rot=(1,0,0;1.5708rad)
  _ExternalGeoVersion = 0
  sketch-geometry (15):
    g0: LineSegment StartX=0 StartY=0 StartZ=0 EndX=-15.75 EndY=0 EndZ=0
    g1: LineSegment StartX=-15.75 StartY=0 StartZ=0 EndX=-15.75 EndY=-21.11 EndZ=0
    g2: LineSegment StartX=-15.75 StartY=-21.11 StartZ=0 EndX=0 EndY=-21.11 EndZ=0
    g3: LineSegment StartX=0 StartY=-21.11 StartZ=0 EndX=0 EndY=0 EndZ=0
    g4: Circle CenterX=-2.775 CenterY=-2.775 CenterZ=0 NormalX=0 NormalY=0 NormalZ=1 AngleXU=0 Radius=1.56
    g5: Circle CenterX=-2.775 CenterY=-18.335 CenterZ=0 NormalX=0 NormalY=0 NormalZ=1 AngleXU=0 Radius=1.56
    g6: Circle CenterX=-14.19 CenterY=-2.39 CenterZ=0 NormalX=0 NormalY=0 NormalZ=1 AngleXU=0 Radius=1.05
    g7: Circle CenterX=-14.19 CenterY=-4.73 CenterZ=0 NormalX=0 NormalY=0 NormalZ=1 AngleXU=0 Radius=1.05
    g8: Circle CenterX=-14.19 CenterY=-7.07 CenterZ=0 NormalX=0 NormalY=0 NormalZ=1 AngleXU=0 Radius=1.05
    g9: Circle CenterX=-14.19 CenterY=-9.41 CenterZ=0 NormalX=0 NormalY=0 NormalZ=1 AngleXU=0 Radius=1.05
    g10: Circle CenterX=-14.19 CenterY=-11.75 CenterZ=0 NormalX=0 NormalY=0 NormalZ=1 AngleXU=0 Radius=1.05
    g11: Circle CenterX=-14.19 CenterY=-14.09 CenterZ=0 NormalX=0 NormalY=0 NormalZ=1 AngleXU=0 Radius=1.05
    g12: Circle CenterX=-14.19 CenterY=-16.43 CenterZ=0 NormalX=0 NormalY=0 NormalZ=1 AngleXU=0 Radius=1.05
    g13: Circle CenterX=-14.19 CenterY=-18.77 CenterZ=0 NormalX=0 NormalY=0 NormalZ=1 AngleXU=0 Radius=1.05
    g14: LineSegment [constr] StartX=-14.19 StartY=0 StartZ=0 EndX=-14.19 EndY=-21.11 EndZ=0
  constraints (45):
    c: Coincident(g0,g1)
    c: Coincident(g1,g2)
    c: Coincident(g2,g3)
    c: Coincident(g3,g0)
    c: Horizontal(g0)
    c: Horizontal(g2)
    c: Vertical(g1)
    c: Vertical(g3)
    c: Coincident(g0,g-1)
    c: DistanceX(g2,g2) = 15.75
    c: DistanceY(g1,g1) = 21.11
    c: Equal(g5,g4)
    c: DistanceY(g5,g4) = 15.56
    c: Diameter(g4) = 3.12
    c: DistanceY(g4,g0) = 2.775
    c: DistanceX(g4,g0) = 2.775
    c: DistanceX(g5,g2) = 2.775
    c: Diameter(g6) = 2.1
    c: Equal(g6,g7)
    c: Equal(g7,g8)
    c: Equal(g8,g9)
    c: Equal(g9,g10)
    c: Equal(g10,g11)
    c: Equal(g11,g12)
    c: Equal(g12,g13)
    c: PointOnObject(g14,g0)
    c: PointOnObject(g14,g2)
    c: Vertical(g14)
    c: DistanceX(g0,g14) = 1.56
    c: PointOnObject(g6,g14)
    c: PointOnObject(g7,g14)
    c: PointOnObject(g8,g14)
    c: PointOnObject(g9,g14)
    c: PointOnObject(g10,g14)
    c: PointOnObject(g12,g14)
    c: PointOnObject(g11,g14)
    c: PointOnObject(g13,g14)
    c: DistanceY(g7,g6) = 2.34
    c: DistanceY(g8,g7) = 2.34
    c: DistanceY(g9,g8) = 2.34
    c: DistanceY(g10,g9) = 2.34
    c: DistanceY(g11,g10) = 2.34
    c: DistanceY(g12,g11) = 2.34
    c: DistanceY(g13,g12) = 2.34
    c: DistanceY(g6,g0) = 2.39
FEATURE [PartDesign::Pad] Pad014  label="Pad_Plate"
  Direction = (0,-1,2e-16)
  Length = 1
  Length2 = 10
  Placement = pos=(0,0,0) rot=(1,0,0;1.5708rad)
  Profile = -> Sketch025
  ReferenceAxis = -> Sketch025 [N_Axis]
  Refine = true
  SideType = 0
  Suppressed = false
  Type = 0
  Type2 = 0
FEATURE [PartDesign::Pad] Pad015  label="Pad_Circuit1"
  BaseFeature = -> Pad014
  Direction = (0,-1,2e-16)
  Length = 0.5
  Length2 = 10
  Placement = pos=(0,0,0) rot=(1,0,0;1.5708rad)
  Profile = -> Sketch024
  ReferenceAxis = -> Sketch024 [N_Axis]
  Refine = true
  Reversed = true
  SideType = 0
  Suppressed = false
  Type = 0
  Type2 = 0
FEATURE [Sketcher::SketchObject] Sketch026
  ArcFitTolerance = 1e-06
  AttachmentOffset = pos=(0,0,-0.5) rot=(0,0,1;0rad)
  AttachmentSupport = -> [XZ_Plane008]
  ExternalGeometry = -> [Pad015]
  ExternalTypes = [0]
  FullyConstrained = true
  MakeInternals = false
  MapMode = 5
  Placement = pos=(0,0.5,-1e-16) rot=(1,0,0;1.5708rad)
  _ExternalGeoVersion = 0
  sketch-geometry (56):
    g0: LineSegment StartX=-9.44 StartY=-2.15 StartZ=0 EndX=-10.44 EndY=-2.15 EndZ=0
    g1: LineSegment StartX=-10.44 StartY=-2.15 StartZ=0 EndX=-10.44 EndY=-3.15 EndZ=0
    g2: LineSegment StartX=-10.44 StartY=-3.15 StartZ=0 EndX=-9.44 EndY=-3.15 EndZ=0
    g3: LineSegment StartX=-9.44 StartY=-3.15 StartZ=0 EndX=-9.44 EndY=-2.15 EndZ=0
    g4: LineSegment StartX=-5.84 StartY=-3.65 StartZ=0 EndX=-6.84 EndY=-3.65 EndZ=0
    g5: LineSegment StartX=-6.84 StartY=-3.65 StartZ=0 EndX=-6.84 EndY=-4.65 EndZ=0
    g6: LineSegment StartX=-6.84 StartY=-4.65 StartZ=0 EndX=-5.84 EndY=-4.65 EndZ=0
    g7: LineSegment StartX=-5.84 StartY=-4.65 StartZ=0 EndX=-5.84 EndY=-3.65 EndZ=0
    g8: LineSegment StartX=-9.44 StartY=-3.65 StartZ=0 EndX=-10.44 EndY=-3.65 EndZ=0
    g9: LineSegment StartX=-10.44 StartY=-3.65 StartZ=0 EndX=-10.44 EndY=-4.65 EndZ=0
    g10: LineSegment StartX=-10.44 StartY=-4.65 StartZ=0 EndX=-9.44 EndY=-4.65 EndZ=0
    g11: LineSegment StartX=-9.44 StartY=-4.65 StartZ=0 EndX=-9.44 EndY=-3.65 EndZ=0
    g12: LineSegment StartX=-9.44 StartY=-5.15 StartZ=0 EndX=-10.44 EndY=-5.15 EndZ=0
    g13: LineSegment StartX=-10.44 StartY=-5.15 StartZ=0 EndX=-10.44 EndY=-6.15 EndZ=0
    g14: LineSegment StartX=-10.44 StartY=-6.15 StartZ=0 EndX=-9.44 EndY=-6.15 EndZ=0
    g15: LineSegment StartX=-9.44 StartY=-6.15 StartZ=0 EndX=-9.44 EndY=-5.15 EndZ=0
    g16: LineSegment StartX=-5.84 StartY=-5.15 StartZ=0 EndX=-6.84 EndY=-5.15 EndZ=0
    g17: LineSegment StartX=-6.84 StartY=-5.15 StartZ=0 EndX=-6.84 EndY=-6.15 EndZ=0
    g18: LineSegment StartX=-6.84 StartY=-6.15 StartZ=0 EndX=-5.84 EndY=-6.15 EndZ=0
    g19: LineSegment StartX=-5.84 StartY=-6.15 StartZ=0 EndX=-5.84 EndY=-5.15 EndZ=0
    g20: LineSegment StartX=-1.68 StartY=-9.96 StartZ=0 EndX=-3.06 EndY=-9.96 EndZ=0
    g21: LineSegment StartX=-3.06 StartY=-9.96 StartZ=0 EndX=-3.06 EndY=-12.74 EndZ=0
    g22: LineSegment StartX=-3.06 StartY=-12.74 StartZ=0 EndX=-1.68 EndY=-12.74 EndZ=0
    g23: LineSegment StartX=-1.68 StartY=-12.74 StartZ=0 EndX=-1.68 EndY=-9.96 EndZ=0
    g24: LineSegment StartX=-4.82 StartY=-7.44 StartZ=0 EndX=-10.9 EndY=-7.44 EndZ=0
    g25: LineSegment StartX=-10.9 StartY=-7.44 StartZ=0 EndX=-10.9 EndY=-13.5 EndZ=0
    g26: LineSegment StartX=-10.9 StartY=-13.5 StartZ=0 EndX=-4.82 EndY=-13.5 EndZ=0
    g27: LineSegment StartX=-4.82 StartY=-13.5 StartZ=0 EndX=-4.82 EndY=-7.44 EndZ=0
    g28: LineSegment StartX=-4.8 StartY=-15.5 StartZ=0 EndX=-6.6 EndY=-15.5 EndZ=0
    g29: LineSegment StartX=-6.6 StartY=-15.5 StartZ=0 EndX=-6.6 EndY=-15.96 EndZ=0
    g30: LineSegment StartX=-6.6 StartY=-15.96 StartZ=0 EndX=-4.8 EndY=-15.96 EndZ=0
    g31: LineSegment StartX=-4.8 StartY=-15.96 StartZ=0 EndX=-4.8 EndY=-15.5 EndZ=0
    g32: LineSegment StartX=-4.8 StartY=-16.11 StartZ=0 EndX=-6.6 EndY=-16.11 EndZ=0
    g33: LineSegment StartX=-6.6 StartY=-16.11 StartZ=0 EndX=-6.6 EndY=-16.81 EndZ=0
    g34: LineSegment StartX=-6.6 StartY=-16.81 StartZ=0 EndX=-4.8 EndY=-16.81 EndZ=0
    g35: LineSegment StartX=-4.8 StartY=-16.81 StartZ=0 EndX=-4.8 EndY=-16.11 EndZ=0
    g36: LineSegment StartX=-9.5 StartY=-15.5 StartZ=0 EndX=-11.7 EndY=-15.5 EndZ=0
    g37: LineSegment StartX=-11.7 StartY=-15.5 StartZ=0 EndX=-11.7 EndY=-15.96 EndZ=0
    g38: LineSegment StartX=-11.7 StartY=-15.96 StartZ=0 EndX=-9.5 EndY=-15.96 EndZ=0
    g39: LineSegment StartX=-9.5 StartY=-15.96 StartZ=0 EndX=-9.5 EndY=-15.5 EndZ=0
    g40: LineSegment StartX=-9.5 StartY=-16.11 StartZ=0 EndX=-11.7 EndY=-16.11 EndZ=0
    g41: LineSegment StartX=-11.7 StartY=-16.11 StartZ=0 EndX=-11.7 EndY=-16.81 EndZ=0
    g42: LineSegment StartX=-11.7 StartY=-16.81 StartZ=0 EndX=-9.5 EndY=-16.81 EndZ=0
    g43: LineSegment StartX=-9.5 StartY=-16.81 StartZ=0 EndX=-9.5 EndY=-16.11 EndZ=0
    g44: LineSegment StartX=-4.78 StartY=-18.4 StartZ=0 EndX=-5.58 EndY=-18.4 EndZ=0
    g45: LineSegment StartX=-5.58 StartY=-18.4 StartZ=0 EndX=-5.58 EndY=-19.5 EndZ=0
    g46: LineSegment StartX=-5.58 StartY=-19.5 StartZ=0 EndX=-4.78 EndY=-19.5 EndZ=0
    g47: LineSegment StartX=-4.78 StartY=-19.5 StartZ=0 EndX=-4.78 EndY=-18.4 EndZ=0
    g48: LineSegment StartX=-6.98 StartY=-17.7 StartZ=0 EndX=-8.92 EndY=-17.7 EndZ=0
    g49: LineSegment StartX=-8.92 StartY=-17.7 StartZ=0 EndX=-8.92 EndY=-20.14 EndZ=0
    g50: LineSegment StartX=-8.92 StartY=-20.14 StartZ=0 EndX=-6.98 EndY=-20.14 EndZ=0
    g51: LineSegment StartX=-6.98 StartY=-20.14 StartZ=0 EndX=-6.98 EndY=-17.7 EndZ=0
    g52: LineSegment StartX=-10.88 StartY=-18.4 StartZ=0 EndX=-11.68 EndY=-18.4 EndZ=0
    g53: LineSegment StartX=-11.68 StartY=-18.4 StartZ=0 EndX=-11.68 EndY=-19.5 EndZ=0
    g54: LineSegment StartX=-11.68 StartY=-19.5 StartZ=0 EndX=-10.88 EndY=-19.5 EndZ=0
    g55: LineSegment StartX=-10.88 StartY=-19.5 StartZ=0 EndX=-10.88 EndY=-18.4 EndZ=0
  constraints (168):
    c: Coincident(g0,g1)
    c: Coincident(g1,g2)
    c: Coincident(g2,g3)
    c: Coincident(g3,g0)
    c: Horizontal(g0)
    c: Horizontal(g2)
    c: Vertical(g1)
    c: Vertical(g3)
    c: Coincident(g4,g5)
    c: Coincident(g5,g6)
    c: Coincident(g6,g7)
    c: Coincident(g7,g4)
    c: Horizontal(g4)
    c: Horizontal(g6)
    c: Vertical(g5)
    c: Vertical(g7)
    c: Coincident(g8,g9)
    c: Coincident(g9,g10)
    c: Coincident(g10,g11)
    c: Coincident(g11,g8)
    c: Horizontal(g8)
    c: Horizontal(g10)
    c: Vertical(g9)
    c: Vertical(g11)
    c: Coincident(g12,g13)
    c: Coincident(g13,g14)
    c: Coincident(g14,g15)
    c: Coincident(g15,g12)
    c: Horizontal(g12)
    c: Horizontal(g14)
    c: Vertical(g13)
    c: Vertical(g15)
    c: Coincident(g16,g17)
    c: Coincident(g17,g18)
    c: Coincident(g18,g19)
    c: Coincident(g19,g16)
    c: Horizontal(g16)
    c: Horizontal(g18)
    c: Vertical(g17)
    c: Vertical(g19)
    c: Coincident(g20,g21)
    c: Coincident(g21,g22)
    c: Coincident(g22,g23)
    c: Coincident(g23,g20)
    c: Horizontal(g20)
    c: Horizontal(g22)
    c: Vertical(g21)
    c: Vertical(g23)
    c: Coincident(g24,g25)
    c: Coincident(g25,g26)
    c: Coincident(g26,g27)
    c: Coincident(g27,g24)
    c: Horizontal(g24)
    c: Horizontal(g26)
    c: Vertical(g25)
    c: Vertical(g27)
    c: Coincident(g28,g29)
    c: Coincident(g29,g30)
    c: Coincident(g30,g31)
    c: Coincident(g31,g28)
    c: Horizontal(g28)
    c: Horizontal(g30)
    c: Vertical(g29)
    c: Vertical(g31)
    c: Coincident(g32,g33)
    c: Coincident(g33,g34)
    c: Coincident(g34,g35)
    c: Coincident(g35,g32)
    c: Horizontal(g32)
    c: Horizontal(g34)
    c: Vertical(g33)
    c: Vertical(g35)
    c: Coincident(g36,g37)
    c: Coincident(g37,g38)
    c: Coincident(g38,g39)
    c: Coincident(g39,g36)
    c: Horizontal(g36)
    c: Horizontal(g38)
    c: Vertical(g37)
    c: Vertical(g39)
    c: Coincident(g40,g41)
    c: Coincident(g41,g42)
    c: Coincident(g42,g43)
    c: Coincident(g43,g40)
    c: Horizontal(g40)
    c: Horizontal(g42)
    c: Vertical(g41)
    c: Vertical(g43)
    c: Coincident(g44,g45)
    c: Coincident(g45,g46)
    c: Coincident(g46,g47)
    c: Coincident(g47,g44)
    c: Horizontal(g44)
    c: Horizontal(g46)
    c: Vertical(g45)
    c: Vertical(g47)
    c: Coincident(g48,g49)
    c: Coincident(g49,g50)
    c: Coincident(g50,g51)
    c: Coincident(g51,g48)
    c: Horizontal(g48)
    c: Horizontal(g50)
    c: Vertical(g49)
    c: Vertical(g51)
    c: Coincident(g52,g53)
    c: Coincident(g53,g54)
    c: Coincident(g54,g55)
    c: Coincident(g55,g52)
    c: Horizontal(g52)
    c: Horizontal(g54)
    c: Vertical(g53)
    c: Vertical(g55)
    c: Equal(g0,g3)
    c: Equal(g3,g4)
    c: Equal(g4,g7)
    c: Equal(g7,g16)
    c: Equal(g16,g19)
    c: Equal(g19,g12)
    c: Equal(g12,g15)
    c: Equal(g15,g8)
    c: Equal(g8,g11)
    c: PointOnObject(g0,g-3)
    c: PointOnObject(g2,g-4)
    c: DistanceX(g-4,g1) = 0.6
    c: PointOnObject(g8,g-5)
    c: PointOnObject(g1,g9)
    c: PointOnObject(g12,g-6)
    c: PointOnObject(g9,g13)
    c: PointOnObject(g5,g17)
    c: PointOnObject(g4,g8)
    c: PointOnObject(g16,g12)
    c: DistanceX(g-7,g4) = 0.6
    c: DistanceX(g-8,g24) = 0.64
    c: DistanceY(g24,g-8) = 0.64
    c: DistanceX(g26,g-9) = 0.64
    c: DistanceY(g-9,g26) = 0.64
    c: PointOnObject(g20,g-11)
    c: PointOnObject(g20,g-10)
    c: DistanceY(g20,g-10) = 0.8
    c: DistanceY(g-10,g21) = 0.8
    c: DistanceX(g50,g-25) = 0.25
    c: DistanceY(g-25,g50) = 0.25
    c: DistanceY(g48,g-24) = 0.25
    c: DistanceX(g-24,g48) = 0.25
    c: PointOnObject(g28,g-12)
    c: PointOnObject(g29,g-13)
    c: DistanceX(g-12,g28) = 0.8
    c: DistanceX(g28,g-12) = 0.8
    c: PointOnObject(g32,g-14)
    c: PointOnObject(g33,g-15)
    c: PointOnObject(g29,g33)
    c: PointOnObject(g30,g35)
    c: PointOnObject(g36,g-16)
    c: PointOnObject(g37,g-17)
    c: DistanceX(g-16,g36) = 0.6
    c: DistanceX(g36,g-16) = 0.6
    c: PointOnObject(g40,g-18)
    c: PointOnObject(g41,g-19)
    c: PointOnObject(g37,g41)
    c: PointOnObject(g38,g43)
    c: PointOnObject(g52,g-23)
    c: PointOnObject(g54,g-22)
    c: DistanceY(g52,g-22) = 0.6
    c: DistanceY(g-23,g53) = 0.6
    c: PointOnObject(g44,g-20)
    c: PointOnObject(g46,g-21)
    c: PointOnObject(g44,g52)
    c: PointOnObject(g45,g54)
FEATURE [PartDesign::Pad] Pad016  label="Pad_Circuit2"
  BaseFeature = -> Pad015
  Direction = (0,-1,2e-16)
  Length = 1
  Length2 = 10
  Placement = pos=(0,0,0) rot=(1,0,0;1.5708rad)
  Profile = -> Sketch026
  ReferenceAxis = -> Sketch026 [N_Axis]
  Refine = true
  SideType = 2
  Suppressed = false
  Type = 0
  Type2 = 0
FEATURE [PartDesign::CoordinateSystem] MPU6050
  AttacherType = Attacher::AttachEngine3D
  AttachmentOffset = pos=(0,0,0) rot=(-0.57735,0.57735,-0.57735;2.0944rad)
  AttachmentSupport = -> [Pad016]
  MapMode = 11
  Placement = pos=(-2.775,0,-2.775) rot=(0,0,1;0rad)
FEATURE [PartDesign::Body] Body006  label="Body_MPU6050"
  AllowCompound = false
  Group = -> [Sketch025,Pad014,Sketch024,Pad015,Sketch026,Pad016,MPU6050]
  Origin = -> Origin008
  Tip = -> Pad016
FEATURE [App::Link] Body_MPU6050  label="Body_MPU6051"
  AttachedBy = #MPU6050
  AttachedTo = Body_Arm#Arm_MPU6050_Right
  AttachmentOffset = pos=(0,1,0) rot=(0,0,1;0rad)
  LinkPlacement = pos=(-12.6643,7,60.2191) rot=(0,-1,0;1.6057rad)
  LinkedObject = -> Body006
  Placement = pos=(-12.6643,7,60.2191) rot=(0,-1,0;1.6057rad)
  SolverId = Asm4EE
  expr: Placement = Body_Arm.Placement * Arm_MPU6050_Right.Placement * AttachmentOffset * MPU6050.Placement ^ -1
FEATURE [PartDesign::CoordinateSystem] Arm_MPU6050_Right
  AttacherType = Attacher::AttachEngine3D
  AttachmentOffset = pos=(0,0,0) rot=(-1,0,0;1.5708rad)
  AttachmentSupport = -> [Pocket001]
  MapMode = 11
  Placement = pos=(-7.78,-27,0) rot=(-0.57735,-0.57735,0.57735;2.0944rad)
FEATURE [PartDesign::Chamfer] Chamfer002
  Angle = 45
  Base = -> Pocket001 [Edge44,Edge45]
  BaseFeature = -> Pocket001
  ChamferType = 0
  FlipDirection = false
  Refine = true
  Size = 1.5
  Size2 = 1
  SupportTransform = false
  Suppressed = false
  UseAllEdges = false
FEATURE [Part::FeaturePython] Screw  label="M3x6-Screw1063"  # WARN: FeaturePython — macro-defined, semantics opaque (R4)
  BaseObject = -> Body_Arm [Chamfer002.Edge16]
  Diameter = 1
  Invert = false
  LeftHanded = false
  Length = 0
  LengthCustom = 6
  MatchOuter = false
  OffsetAngle = 0
  Placement = pos=(-6.44589,-2,184.586) rot=(1,0,0;1.5708rad)
  Thread = false
  Type = 85
FEATURE [Part::FeaturePython] Screw001  label="M3x6-Screw1064"  # WARN: FeaturePython — macro-defined, semantics opaque (R4)
  BaseObject = -> Body_Arm [Chamfer002.Edge22]
  Diameter = 1
  Invert = false
  LeftHanded = false
  Length = 0
  LengthCustom = 6
  MatchOuter = false
  OffsetAngle = 0
  Placement = pos=(-18.6431,-2,161.647) rot=(1,0,0;1.5708rad)
  Thread = false
  Type = 85
FEATURE [Part::FeaturePython] Screw002  label="M3x6-Screw"  # WARN: FeaturePython — macro-defined, semantics opaque (R4)
  BaseObject = -> Body_Arm [Chamfer002.Edge19]
  Diameter = 1
  Invert = false
  LeftHanded = false
  Length = 0
  LengthCustom = 6
  MatchOuter = false
  OffsetAngle = 0
  Placement = pos=(7.32181,-2,162.553) rot=(1,0,0;1.5708rad)
  Thread = false
  Type = 85
FEATURE [Part::FeaturePython] Screw003  label="M3x12-Screw"  # WARN: FeaturePython — macro-defined, semantics opaque (R4)
  BaseObject = -> Body_Arm [Chamfer002.Edge1]
  Diameter = 1
  Invert = false
  LeftHanded = false
  Length = 3
  LengthCustom = 12
  MatchOuter = false
  OffsetAngle = 0
  Placement = pos=(-9.79417,-2,57.5426) rot=(1,0,0;1.5708rad)
  Thread = false
  Type = 85
FEATURE [Part::FeaturePython] Screw004  label="M3x12-Screw002"  # WARN: FeaturePython — macro-defined, semantics opaque (R4)
  BaseObject = -> Body_Arm [Chamfer002.Edge25]
  Diameter = 1
  Invert = false
  LeftHanded = false
  Length = 3
  LengthCustom = 12
  MatchOuter = false
  OffsetAngle = 0
  Placement = pos=(5.75635,-2,58.0856) rot=(1,0,0;1.5708rad)
  Thread = false
  Type = 85
FEATURE [Part::FeaturePython] Nut  label="(M3.5)-Nut"  # WARN: FeaturePython — macro-defined, semantics opaque (R4)
  BaseObject = -> Screw004 [Edge27]
  Diameter = 5
  Invert = false
  LeftHanded = false
  MatchOuter = false
  OffsetAngle = 0
  Placement = pos=(5.75635,9.7,58.0856) rot=(1,0,0;1.5708rad)
  Thread = false
  Type = 31
FEATURE [Part::FeaturePython] Nut003  label="(M3.5)-Nut002"  # WARN: FeaturePython — macro-defined, semantics opaque (R4)
  BaseObject = -> Screw003 [Edge27]
  Diameter = 5
  Invert = false
  LeftHanded = false
  MatchOuter = false
  OffsetAngle = 0
  Placement = pos=(-9.79417,9.7,57.5426) rot=(1,0,0;1.5708rad)
  Thread = false
  Type = 31
FEATURE [Part::FeaturePython] Screw006  label="M4x8-Screw"  # WARN: FeaturePython — macro-defined, semantics opaque (R4)
  BaseObject = -> Body_ReactionWheel [Chamfer001.Edge406]
  Diameter = 5
  Invert = true
  LeftHanded = false
  Length = 0
  LengthCustom = 8
  MatchOuter = false
  Offset = 2
  OffsetAngle = 0
  Placement = pos=(12.2884,-9.4,218.302) rot=(-1,0,0;1.5708rad)
  Thread = false
  Type = 55
FEATURE [Part::FeaturePython] Screw007  label="M4x8-Screw4798"  # WARN: FeaturePython — macro-defined, semantics opaque (R4)
  BaseObject = -> Body_ReactionWheel [Chamfer001.Edge402]
  Diameter = 5
  Invert = true
  LeftHanded = false
  Length = 0
  LengthCustom = 8
  MatchOuter = false
  Offset = 2
  OffsetAngle = 0
  Placement = pos=(-7.73718,-9.4,221.564) rot=(-1,0,0;1.5708rad)
  Thread = false
  Type = 55
FEATURE [Part::FeaturePython] Screw008  label="M4x8-Screw4799"  # WARN: FeaturePython — macro-defined, semantics opaque (R4)
  BaseObject = -> Body_ReactionWheel [Chamfer001.Edge398]
  Diameter = 5
  Invert = true
  LeftHanded = false
  Length = 0
  LengthCustom = 8
  MatchOuter = false
  Offset = 2
  OffsetAngle = 0
  Placement = pos=(-27.4865,-9.4,216.913) rot=(-1,0,0;1.5708rad)
  Thread = false
  Type = 55
FEATURE [Part::FeaturePython] Screw009  label="M4x8-Screw4800"  # WARN: FeaturePython — macro-defined, semantics opaque (R4)
  BaseObject = -> Body_ReactionWheel [Chamfer001.Edge430]
  Diameter = 5
  Invert = true
  LeftHanded = false
  Length = 0
  LengthCustom = 8
  MatchOuter = false
  Offset = 2
  OffsetAngle = 0
  Placement = pos=(15.6416,-9.4,122.277) rot=(-1,0,0;1.5708rad)
  Thread = false
  Type = 55
FEATURE [Part::FeaturePython] Screw010  label="M4x8-Screw4801"  # WARN: FeaturePython — macro-defined, semantics opaque (R4)
  BaseObject = -> Body_ReactionWheel [Chamfer001.Edge434]
  Diameter = 5
  Invert = true
  LeftHanded = false
  Length = 0
  LengthCustom = 8
  MatchOuter = false
  Offset = 2
  OffsetAngle = 0
  Placement = pos=(-4.10763,-9.4,117.627) rot=(-1,0,0;1.5708rad)
  Thread = false
  Type = 55
FEATURE [Part::FeaturePython] Screw011  label="M4x8-Screw4802"  # WARN: FeaturePython — macro-defined, semantics opaque (R4)
  BaseObject = -> Body_ReactionWheel [Chamfer001.Edge438]
  Diameter = 5
  Invert = true
  LeftHanded = false
  Length = 0
  LengthCustom = 8
  MatchOuter = false
  Offset = 2
  OffsetAngle = 0
  Placement = pos=(-24.1332,-9.4,120.888) rot=(-1,0,0;1.5708rad)
  Thread = false
  Type = 55
FEATURE [Part::FeaturePython] Screw012  label="M4x8-Screw4803"  # WARN: FeaturePython — macro-defined, semantics opaque (R4)
  BaseObject = -> Body_ReactionWheel [Chamfer001.Edge446]
  Diameter = 5
  Invert = true
  LeftHanded = false
  Length = 0
  LengthCustom = 8
  MatchOuter = false
  Offset = 2
  OffsetAngle = 0
  Placement = pos=(-53.2404,-9.4,148.031) rot=(-1,0,0;1.5708rad)
  Thread = false
  Type = 55
FEATURE [Part::FeaturePython] Screw013  label="M4x8-Screw4804"  # WARN: FeaturePython — macro-defined, semantics opaque (R4)
  BaseObject = -> Body_ReactionWheel [Chamfer001.Edge130]
  Diameter = 5
  Invert = true
  LeftHanded = false
  Length = 0
  LengthCustom = 8
  MatchOuter = false
  Offset = 2
  OffsetAngle = 0
  Placement = pos=(-54.6294,-9.4,187.806) rot=(-1,0,0;1.5708rad)
  Thread = false
  Type = 55
FEATURE [Part::FeaturePython] Screw014  label="M4x8-Screw4805"  # WARN: FeaturePython — macro-defined, semantics opaque (R4)
  BaseObject = -> Body_ReactionWheel [Chamfer001.Edge414]
  Diameter = 5
  Invert = true
  LeftHanded = false
  Length = 0
  LengthCustom = 8
  MatchOuter = false
  Offset = 2
  OffsetAngle = 0
  Placement = pos=(41.3956,-9.4,191.159) rot=(-1,0,0;1.5708rad)
  Thread = false
  Type = 55
FEATURE [Part::FeaturePython] Screw015  label="M4x8-Screw4806"  # WARN: FeaturePython — macro-defined, semantics opaque (R4)
  BaseObject = -> Body_ReactionWheel [Chamfer001.Edge422]
  Diameter = 5
  Invert = true
  LeftHanded = false
  Length = 0
  LengthCustom = 8
  MatchOuter = false
  Offset = 2
  OffsetAngle = 0
  Placement = pos=(42.7846,-9.4,151.385) rot=(-1,0,0;1.5708rad)
  Thread = false
  Type = 55
FEATURE [Part::FeaturePython] Nut004  label="M5-Nut"  # WARN: FeaturePython — macro-defined, semantics opaque (R4)
  BaseObject = -> Screw008 [Edge2]
  Diameter = 1
  Invert = true
  LeftHanded = false
  MatchOuter = false
  Offset = -3
  OffsetAngle = 0
  Placement = pos=(-27.4865,-14,216.913) rot=(1,0,0;1.5708rad)
  Thread = false
  Type = 35
FEATURE [Part::FeaturePython] Nut005  label="M5-Nut4869"  # WARN: FeaturePython — macro-defined, semantics opaque (R4)
  BaseObject = -> Screw007 [Edge2]
  Diameter = 1
  Invert = true
  LeftHanded = false
  MatchOuter = false
  Offset = -3
  OffsetAngle = 0
  Placement = pos=(-7.73718,-14,221.564) rot=(1,0,0;1.5708rad)
  Thread = false
  Type = 35
FEATURE [Part::FeaturePython] Nut006  label="M5-Nut4870"  # WARN: FeaturePython — macro-defined, semantics opaque (R4)
  BaseObject = -> Screw006 [Edge2]
  Diameter = 1
  Invert = true
  LeftHanded = false
  MatchOuter = false
  Offset = -3
  OffsetAngle = 0
  Placement = pos=(12.2884,-14,218.302) rot=(1,0,0;1.5708rad)
  Thread = false
  Type = 35
FEATURE [Part::FeaturePython] Nut007  label="M5-Nut4871"  # WARN: FeaturePython — macro-defined, semantics opaque (R4)
  BaseObject = -> Screw014 [Edge2]
  Diameter = 1
  Invert = true
  LeftHanded = false
  MatchOuter = false
  Offset = -3
  OffsetAngle = 0
  Placement = pos=(41.3956,-14,191.159) rot=(1,0,0;1.5708rad)
  Thread = false
  Type = 35
FEATURE [Part::FeaturePython] Nut008  label="M5-Nut4872"  # WARN: FeaturePython — macro-defined, semantics opaque (R4)
  BaseObject = -> Screw015 [Edge2]
  Diameter = 1
  Invert = true
  LeftHanded = false
  MatchOuter = false
  Offset = -3
  OffsetAngle = 0
  Placement = pos=(42.7846,-14,151.385) rot=(1,0,0;1.5708rad)
  Thread = false
  Type = 35
FEATURE [Part::FeaturePython] Nut009  label="M5-Nut4873"  # WARN: FeaturePython — macro-defined, semantics opaque (R4)
  BaseObject = -> Screw009 [Edge2]
  Diameter = 1
  Invert = true
  LeftHanded = false
  MatchOuter = false
  Offset = -3
  OffsetAngle = 0
  Placement = pos=(15.6416,-14,122.277) rot=(1,0,0;1.5708rad)
  Thread = false
  Type = 35
FEATURE [Part::FeaturePython] Nut010  label="M5-Nut4874"  # WARN: FeaturePython — macro-defined, semantics opaque (R4)
  BaseObject = -> Screw010 [Edge2]
  Diameter = 1
  Invert = true
  LeftHanded = false
  MatchOuter = false
  Offset = -3
  OffsetAngle = 0
  Placement = pos=(-4.10763,-14,117.627) rot=(1,0,0;1.5708rad)
  Thread = false
  Type = 35
FEATURE [Part::FeaturePython] Nut011  label="M5-Nut4875"  # WARN: FeaturePython — macro-defined, semantics opaque (R4)
  BaseObject = -> Screw011 [Edge2]
  Diameter = 1
  Invert = true
  LeftHanded = false
  MatchOuter = false
  Offset = -3
  OffsetAngle = 0
  Placement = pos=(-24.1332,-14,120.888) rot=(1,0,0;1.5708rad)
  Thread = false
  Type = 35
FEATURE [Part::FeaturePython] Nut012  label="M5-Nut4876"  # WARN: FeaturePython — macro-defined, semantics opaque (R4)
  BaseObject = -> Screw012 [Edge2]
  Diameter = 1
  Invert = true
  LeftHanded = false
  MatchOuter = false
  Offset = -3
  OffsetAngle = 0
  Placement = pos=(-53.2404,-14,148.031) rot=(1,0,0;1.5708rad)
  Thread = false
  Type = 35
FEATURE [Part::FeaturePython] Nut013  label="M5-Nut4877"  # WARN: FeaturePython — macro-defined, semantics opaque (R4)
  BaseObject = -> Screw013 [Edge2]
  Diameter = 1
  Invert = true
  LeftHanded = false
  MatchOuter = false
  Offset = -3
  OffsetAngle = 0
  Placement = pos=(-54.6294,-14,187.806) rot=(1,0,0;1.5708rad)
  Thread = false
  Type = 35
FEATURE [Part::FeaturePython] Nut014  label="M4-Nut"  # WARN: FeaturePython — macro-defined, semantics opaque (R4)
  BaseObject = -> Body_ReactionWheel [Chamfer001.Edge240]
  Diameter = 6
  Invert = false
  LeftHanded = false
  MatchOuter = false
  Offset = 0.2
  OffsetAngle = 90
  Placement = pos=(-6.20858,-15.9,177.79) rot=(-0.01745,-0.01745,0.999695;1.5711rad)
  Thread = false
  Type = 31
FEATURE [Part::FeaturePython] Nut015  label="M4-Nut234"  # WARN: FeaturePython — macro-defined, semantics opaque (R4)
  BaseObject = -> Body_ReactionWheel [Chamfer001.Edge375]
  Diameter = 6
  Invert = false
  LeftHanded = false
  MatchOuter = false
  Offset = 0.2
  OffsetAngle = 90
  Placement = pos=(-5.52455,-15.9,158.202) rot=(-0.01745,-0.01745,0.999695;1.5711rad)
  Thread = false
  Type = 31
FEATURE [Part::FeaturePython] Screw016  label="M4x10-Screw"  # WARN: FeaturePython — macro-defined, semantics opaque (R4)
  BaseObject = -> Body_ReactionWheel [Chamfer001.Edge235]
  Diameter = 6
  Invert = false
  LeftHanded = false
  Length = 2
  LengthCustom = 10
  MatchOuter = false
  Offset = 5
  OffsetAngle = 0
  Placement = pos=(-6.50173,-15.9,186.185) rot=(0,-1,0;0.034907rad)
  Thread = false
  Type = 61
FEATURE [Part::FeaturePython] Screw017  label="M4x10-Screw002"  # WARN: FeaturePython — macro-defined, semantics opaque (R4)
  BaseObject = -> Body_ReactionWheel [Chamfer001.Edge375]
  Diameter = 6
  Invert = true
  LeftHanded = false
  Length = 2
  LengthCustom = 10
  MatchOuter = false
  Offset = 5
  OffsetAngle = 0
  Placement = pos=(-5.34307,-15.9,153.005) rot=(0,1,0;3.10669rad)
  Thread = false
  Type = 61
FEATURE [Mesh::Feature] Mesh002  label="Body_Rondelle (Meshed)"
FEATURE [Mesh::Feature] Mesh003  label="Body_ReactionWheel (Meshed)"
FEATURE [Sketcher::SketchObject] Sketch027
  ArcFitTolerance = 1e-06
  AttachmentSupport = -> [Chamfer002]
  ExternalGeometry = -> [Chamfer002]
  ExternalTypes = [0]
  FullyConstrained = true
  MakeInternals = false
  MapMode = 5
  Placement = pos=(0,0,8) rot=(0,0,1;0rad)
  _ExternalGeoVersion = 0
  sketch-geometry (3):
    g0: ArcOfCircle CenterX=0 CenterY=-84.8494 CenterZ=0 NormalX=0 NormalY=0 NormalZ=1 AngleXU=0 Radius=25 StartAngle=2.3746 EndAngle=7.05018
    g1: LineSegment StartX=-18 StartY=-67.5 StartZ=0 EndX=18 EndY=-67.5 EndZ=0
    g2: Circle CenterX=0 CenterY=-84.8494 CenterZ=0 NormalX=0 NormalY=0 NormalZ=1 AngleXU=0 Radius=9
  constraints (7):
    c: Coincident(g0,g-3)
    c: Coincident(g1,g-3)
    c: Coincident(g0,g1)
    c: Coincident(g0,g1)
    c: Horizontal(g1)
    c: Coincident(g2,g0)
    c: Diameter(g2) = 18
FEATURE [PartDesign::Pad] Pad017  label="Pad_LockBearing"
  BaseFeature = -> Chamfer002
  Direction = (0,0,1)
  Length = 2
  Length2 = 10
  Profile = -> Sketch027
  ReferenceAxis = -> Sketch027 [N_Axis]
  Refine = true
  Reversed = true
  SideType = 0
  Suppressed = false
  Type = 0
  Type2 = 0
FEATURE [Sketcher::SketchObject] Sketch030
  ArcFitTolerance = 1e-06
  AttachmentSupport = -> [XY_Plane009]
  ExternalTypes = [0]
  FullyConstrained = true
  MakeInternals = false
  MapMode = 5
  _ExternalGeoVersion = 0
  sketch-geometry (6):
    g0: ArcOfCircle CenterX=0 CenterY=-84.8494 CenterZ=0 NormalX=0 NormalY=0 NormalZ=1 AngleXU=0 Radius=25 StartAngle=2.3746 EndAngle=7.05018
    g1: LineSegment StartX=18 StartY=-67.5 StartZ=0 EndX=-18 EndY=-67.5 EndZ=0
    g2: Circle CenterX=15.1 CenterY=-75.5 CenterZ=0 NormalX=0 NormalY=0 NormalZ=1 AngleXU=0 Radius=1.8
    g3: Circle CenterX=-15.1 CenterY=-75.5 CenterZ=0 NormalX=0 NormalY=0 NormalZ=1 AngleXU=0 Radius=1.8
    g4: Circle CenterX=0 CenterY=-105.5 CenterZ=0 NormalX=0 NormalY=0 NormalZ=1 AngleXU=0 Radius=1.8
    g5: Circle CenterX=0 CenterY=-84.8494 CenterZ=0 NormalX=0 NormalY=0 NormalZ=1 AngleXU=0 Radius=9
  constraints (17):
    c: PointOnObject(g0,g-2)
    c: Diameter(g0) = 50
    c: Horizontal(g1)
    c: Coincident(g0,g1)
    c: Coincident(g0,g1)
    c: DistanceX(g1,g1) = 36
    c: PointOnObject(g4,g-2)
    c: Equal(g3,g2)
    c: Equal(g2,g4)
    c: Diameter(g2) = 3.6
    c: Symmetric(g2,g3,g-2)
    c: DistanceX(g3,g2) = 30.2
    c: DistanceY(g2,g0) = 8
    c: DistanceY(g4,g2) = 30
    c: DistanceY(g0,g-1) = 67.5
    c: Coincident(g5,g0)
    c: Diameter(g5) = 18
FEATURE [PartDesign::Pad] Pad018
  Direction = (0,0,1)
  Length = 3
  Length2 = 10
  Profile = -> Sketch030
  ReferenceAxis = -> Sketch030 [N_Axis]
  Refine = true
  Reversed = true
  SideType = 0
  Suppressed = false
  Type = 0
  Type2 = 0
FEATURE [PartDesign::CoordinateSystem] BearingLock
  AttacherType = Attacher::AttachEngine3D
  AttachmentOffset = pos=(0,0,0) rot=(0,0,-1;1.5708rad)
  AttachmentSupport = -> [Pad018]
  MapMode = 11
  Placement = pos=(0,-84.8494,-3) rot=(0,0,1;0rad)
FEATURE [App::Link] Body_BearingLock  label="Body_BearingLock001"
  AttachedBy = #BearingLock
  AttachedTo = Body_Arm#Arm_Axis_Bottom
  AttachmentOffset = pos=(0,0,-12) rot=(0,0,1;0rad)
  LinkPlacement = pos=(-2.9612,7,84.7977) rot=(0.999695,-0.01745,0.01745;1.5711rad)
  LinkedObject = -> Body007
  Placement = pos=(-2.9612,7,84.7977) rot=(0.999695,-0.01745,0.01745;1.5711rad)
  SolverId = Asm4EE
  expr: Placement = Body_Arm.Placement * Arm_Axis_Bottom.Placement * AttachmentOffset * BearingLock.Placement ^ -1
FEATURE [Part::FeaturePython] Screw018  label="M3x14-Screw"  # WARN: FeaturePython — macro-defined, semantics opaque (R4)
  BaseObject = -> Body_BearingLock [Pad018.Edge15]
  Diameter = 4
  Invert = true
  LeftHanded = false
  Length = 6
  LengthCustom = 14
  MatchOuter = false
  OffsetAngle = 0
  Placement = pos=(-15.4171,10,8.81667) rot=(-1,0,0;1.5708rad)
  Thread = false
  Type = 52
FEATURE [Part::FeaturePython] Screw019  label="M3x14-Screw979"  # WARN: FeaturePython — macro-defined, semantics opaque (R4)
  BaseObject = -> Body_BearingLock [Pad018.Edge12]
  Diameter = 4
  Invert = true
  LeftHanded = false
  Length = 6
  LengthCustom = 14
  MatchOuter = false
  OffsetAngle = 0
  Placement = pos=(14.7645,10,9.87064) rot=(-1,0,0;1.5708rad)
  Thread = false
  Type = 52
FEATURE [Part::FeaturePython] Screw020  label="M3x14-Screw980"  # WARN: FeaturePython — macro-defined, semantics opaque (R4)
  BaseObject = -> Body_BearingLock [Pad018.Edge18]
  Diameter = 4
  Invert = true
  LeftHanded = false
  Length = 6
  LengthCustom = 14
  MatchOuter = false
  OffsetAngle = 0
  Placement = pos=(0.720697,10,-20.6381) rot=(-1,0,0;1.5708rad)
  Thread = false
  Type = 52
FEATURE [Sketcher::SketchObject] Sketch031
  ArcFitTolerance = 1e-06
  AttachmentSupport = -> [Pad018]
  ExternalGeometry = -> [Pad018]
  ExternalTypes = [0]
  FullyConstrained = true
  MakeInternals = false
  MapMode = 5
  Placement = pos=(0,0,-3) rot=(1,0,0;3.14159rad)
  _ExternalGeoVersion = 0
  sketch-geometry (2):
    g0: Circle CenterX=-15 CenterY=83.5 CenterZ=0 NormalX=0 NormalY=0 NormalZ=1 AngleXU=0 Radius=4
    g1: Circle CenterX=15 CenterY=83.5 CenterZ=0 NormalX=0 NormalY=0 NormalZ=1 AngleXU=0 Radius=4
  constraints (5):
    c: Equal(g0,g1)
    c: Diameter(g0) = 8
    c: Symmetric(g0,g1,g-2)
    c: DistanceX(g0,g1) = 30
    c: DistanceY(g-3,g0) = 8
FEATURE [PartDesign::Pad] Pad019
  BaseFeature = -> Pad018
  Direction = (0,0,-1)
  Length = 20
  Length2 = 10
  Profile = -> Sketch031
  ReferenceAxis = -> Sketch031 [N_Axis]
  Refine = true
  SideType = 0
  Suppressed = false
  Type = 0
  Type2 = 0
FEATURE [PartDesign::Fillet] Fillet
  Base = -> Pad019 [Edge24,Edge22]
  BaseFeature = -> Pad019
  Radius = 3.5
  Refine = true
  SupportTransform = false
  Suppressed = false
  UseAllEdges = false
FEATURE [PartDesign::Body] Body007  label="Body_BearingLock"
  AllowCompound = false
  Group = -> [Sketch030,Pad018,BearingLock,Sketch031,Pad019,Fillet]
  Origin = -> Origin009
  Tip = -> Fillet
FEATURE [Sketcher::SketchObject] Sketch032
  ArcFitTolerance = 1e-06
  AttachmentSupport = -> [Pad017]
  ExternalGeometry = -> [Pad017]
  ExternalTypes = [0]
  FullyConstrained = true
  MakeInternals = false
  MapMode = 5
  Placement = pos=(0,0,8) rot=(0,0,1;0rad)
  _ExternalGeoVersion = 0
  sketch-geometry (3):
    g0: Circle CenterX=-15 CenterY=-75.5 CenterZ=0 NormalX=0 NormalY=0 NormalZ=1 AngleXU=0 Radius=1.8
    g1: Circle CenterX=15 CenterY=-75.5 CenterZ=0 NormalX=0 NormalY=0 NormalZ=1 AngleXU=0 Radius=1.8
    g2: Circle CenterX=0 CenterY=-105.5 CenterZ=0 NormalX=0 NormalY=0 NormalZ=1 AngleXU=0 Radius=1.8
  constraints (8):
    c: PointOnObject(g2,g-2)
    c: Equal(g2,g1)
    c: Equal(g1,g0)
    c: Diameter(g0) = 3.6
    c: DistanceY(g0,g-3) = 8
    c: DistanceY(g2,g0) = 30
    c: Symmetric(g0,g1,g-2)
    c: DistanceX(g0,g1) = 30
FEATURE [PartDesign::Pocket] Pocket009
  BaseFeature = -> Pad017
  Direction = (0,0,-1)
  Length = 5
  Length2 = 5
  Profile = -> Sketch032
  ReferenceAxis = -> Sketch032 [N_Axis]
  Refine = true
  SideType = 0
  Suppressed = false
  Type = 1
  Type2 = 0
FEATURE [Sketcher::SketchObject] Sketch033
  ArcFitTolerance = 1e-06
  AttachmentSupport = -> [Pocket009]
  ExternalGeometry = -> [Pocket009]
  ExternalTypes = [0]
  FullyConstrained = true
  MakeInternals = false
  MapMode = 5
  Placement = pos=(0,0,8) rot=(0,0,1;0rad)
  _ExternalGeoVersion = 0
  sketch-geometry (21):
    g0: LineSegment StartX=-13.35 StartY=-78.3579 StartZ=0 EndX=-11.7 EndY=-75.5 EndZ=0
    g1: LineSegment StartX=-11.7 StartY=-75.5 StartZ=0 EndX=-13.35 EndY=-72.6421 EndZ=0
    g2: LineSegment StartX=-13.35 StartY=-72.6421 StartZ=0 EndX=-16.65 EndY=-72.6421 EndZ=0
    g3: LineSegment StartX=-16.65 StartY=-72.6421 StartZ=0 EndX=-18.3 EndY=-75.5 EndZ=0
    g4: LineSegment StartX=-18.3 StartY=-75.5 StartZ=0 EndX=-16.65 EndY=-78.3579 EndZ=0
    g5: LineSegment StartX=-16.65 StartY=-78.3579 StartZ=0 EndX=-13.35 EndY=-78.3579 EndZ=0
    g6: Circle [constr] CenterX=-15 CenterY=-75.5 CenterZ=0 NormalX=0 NormalY=0 NormalZ=1 AngleXU=0 Radius=3.3
    g7: LineSegment StartX=16.65 StartY=-72.6421 StartZ=0 EndX=13.35 EndY=-72.6421 EndZ=0
    g8: LineSegment StartX=13.35 StartY=-72.6421 StartZ=0 EndX=11.7 EndY=-75.5 EndZ=0
    g9: LineSegment StartX=11.7 StartY=-75.5 StartZ=0 EndX=13.35 EndY=-78.3579 EndZ=0
    g10: LineSegment StartX=13.35 StartY=-78.3579 StartZ=0 EndX=16.65 EndY=-78.3579 EndZ=0
    g11: LineSegment StartX=16.65 StartY=-78.3579 StartZ=0 EndX=18.3 EndY=-75.5 EndZ=0
    g12: LineSegment StartX=18.3 StartY=-75.5 StartZ=0 EndX=16.65 EndY=-72.6421 EndZ=0
    g13: Circle [constr] CenterX=15 CenterY=-75.5 CenterZ=0 NormalX=0 NormalY=0 NormalZ=1 AngleXU=0 Radius=3.3
    g14: LineSegment StartX=1.65 StartY=-102.642 StartZ=0 EndX=-1.65 EndY=-102.642 EndZ=0
    g15: LineSegment StartX=-1.65 StartY=-102.642 StartZ=0 EndX=-3.3 EndY=-105.5 EndZ=0
    g16: LineSegment StartX=-3.3 StartY=-105.5 StartZ=0 EndX=-1.65 EndY=-108.358 EndZ=0
    g17: LineSegment StartX=-1.65 StartY=-108.358 StartZ=0 EndX=1.65 EndY=-108.358 EndZ=0
    g18: LineSegment StartX=1.65 StartY=-108.358 StartZ=0 EndX=3.3 EndY=-105.5 EndZ=0
    g19: LineSegment StartX=3.3 StartY=-105.5 StartZ=0 EndX=1.65 EndY=-102.642 EndZ=0
    g20: Circle [constr] CenterX=0 CenterY=-105.5 CenterZ=0 NormalX=0 NormalY=0 NormalZ=1 AngleXU=0 Radius=3.3
  constraints (48):
    c: Coincident(g0,g1)
    c: Coincident(g1,g2)
    c: Coincident(g2,g3)
    c: Coincident(g3,g4)
    c: Coincident(g4,g5)
    c: Coincident(g5,g0)
    c: Equal(g0, g1-g5) x5
    c: PointOnObject(g0,g6)
    c: PointOnObject(g1,g6)
    c: PointOnObject(g2,g6)
    c: PointOnObject(g3,g6)
    c: PointOnObject(g4,g6)
    c: PointOnObject(g5,g6)
    c: Coincident(g6,g-3)
    c: Coincident(g7,g8)
    c: Coincident(g8,g9)
    c: Coincident(g9,g10)
    c: Coincident(g10,g11)
    c: Coincident(g11,g12)
    c: Coincident(g12,g7)
    c: Equal(g7, g8-g12) x5
    c: PointOnObject(g7,g13)
    c: PointOnObject(g8,g13)
    c: PointOnObject(g9,g13)
    c: PointOnObject(g10,g13)
    c: PointOnObject(g11,g13)
    c: PointOnObject(g12,g13)
    c: Coincident(g13,g-4)
    c: Coincident(g14,g15)
    c: Coincident(g15,g16)
    c: Coincident(g16,g17)
    c: Coincident(g17,g18)
    c: Coincident(g18,g19)
    c: Coincident(g19,g14)
    c: Equal(g14, g15-g19) x5
    c: PointOnObject(g14,g20)
    c: PointOnObject(g15,g20)
    c: PointOnObject(g16,g20)
    c: PointOnObject(g17,g20)
    c: PointOnObject(g18,g20)
    c: PointOnObject(g19,g20)
    c: Coincident(g20,g-5)
    c: Equal(g13,g6)
    c: Equal(g6,g20)
    c: Diameter(g13) = 6.6
    c: Horizontal(g2)
    c: Horizontal(g7)
    c: Horizontal(g14)
FEATURE [PartDesign::Pocket] Pocket010
  BaseFeature = -> Pocket009
  Direction = (0,0,-1)
  Length = 3
  Length2 = 5
  Profile = -> Sketch033
  ReferenceAxis = -> Sketch033 [N_Axis]
  Refine = true
  SideType = 0
  Suppressed = false
  Type = 0
  Type2 = 0
FEATURE [Mesh::Feature] Mesh006  label="Body_Arm (Meshed)"
FEATURE [Part::FeaturePython] Nut019  label="M3-Nut981"  # WARN: FeaturePython — macro-defined, semantics opaque (R4)
  BaseObject = -> Body_Arm [Pocket010.Edge140]
  Diameter = 4
  Invert = false
  LeftHanded = false
  MatchOuter = false
  Offset = 1
  OffsetAngle = 0
  Placement = pos=(0.720698,2.04e-14,-20.6381) rot=(1,0,0;1.5708rad)
  Thread = false
  Type = 31
FEATURE [Part::FeaturePython] Nut020  label="M3-Nut982"  # WARN: FeaturePython — macro-defined, semantics opaque (R4)
  BaseObject = -> Body_Arm [Pocket010.Edge138]
  Diameter = 4
  Invert = false
  LeftHanded = false
  MatchOuter = false
  Offset = 1
  OffsetAngle = 0
  Placement = pos=(-15.3172,4.4e-15,8.82016) rot=(1,0,0;1.5708rad)
  Thread = false
  Type = 31
FEATURE [Part::FeaturePython] Nut021  label="M3-Nut"  # WARN: FeaturePython — macro-defined, semantics opaque (R4)
  BaseObject = -> Body_Arm [Pocket010.Edge142]
  Diameter = 4
  Invert = false
  LeftHanded = false
  MatchOuter = false
  Offset = 1
  OffsetAngle = 0
  Placement = pos=(14.6646,-2.7e-15,9.86715) rot=(1,0,0;1.5708rad)
  Thread = false
  Type = 31
FEATURE [Mesh::Feature] Mesh  label="Body_Front_Left (Meshed)"
FEATURE [Mesh::Feature] Mesh008  label="Body_Front_Right (Meshed)"
FEATURE [Part::Feature] Part__Feature  label="Open CASCADE STEP translator 7.5 4.1.1"
  Placement = pos=(0,0,-1.6368) rot=(0,0,1;0rad)
  shape: bbox 43.18 x 17.78 x 1.637 mm, 125 faces (baked)
FEATURE [App::Part] Board
  Group = -> [Part__Feature]
  Origin = -> Origin097
FEATURE [Part::Feature] Part__Feature001  label="CAP-0402"
  Placement = pos=(36.266,6.49561,0) rot=(0,0,-1;1.5708rad)
  shape: bbox 0.5 x 1 x 0.5 mm, 58 faces (baked)
FEATURE [App::Part] C1
  Group = -> [Part__Feature001]
  Origin = -> Origin098
FEATURE [App::Part] L1
  Origin = -> Origin002
FEATURE [Part::Feature] Part__Feature003  label="CAP-0603"
  Placement = pos=(11.05,4.77,0) rot=(0,0,-1;1.5708rad)
  shape: bbox 0.8 x 1.6 x 0.8 mm, 58 faces (baked)
FEATURE [App::Part] C24
  Group = -> [Part__Feature003]
  Origin = -> Origin099
FEATURE [Part::Feature] Part__Feature004  label="Extruded"
  shape: bbox 1.75 x 0.95 x 0.23 mm, 6 faces (baked)
FEATURE [App::Part] _855924864  label="6855924864"
  Group = -> [Part__Feature004]
  Origin = -> Origin101
  Placement = pos=(7.57979,10.341,0) rot=(0,0,1;0rad)
FEATURE [App::Part] Z3
  Group = -> [_855924864]
  Origin = -> Origin100
FEATURE [Part::Feature] Part__Feature005  label="SOT-23"
  Placement = pos=(36.0642,13.5591,0.499999) rot=(0,0.707107,0.707107;3.14159rad)
  shape: bbox 3 x 2.5 x 1.1 mm, 49 faces (baked)
FEATURE [App::Part] Q1
  Group = -> [Part__Feature005]
  Origin = -> Origin102
FEATURE [Part::Feature] Part__Feature006  label="Open CASCADE STEP translator 7.5 15.1.1"
  shape: bbox 3.006 x 2.006 x 1.205 mm, 48 faces (baked)
FEATURE [App::Part] Body009
  Group = -> [Part__Feature006]
  Origin = -> Origin106
  Placement = pos=(-1.5,-1,0) rot=(0,0,1;0rad)
FEATURE [Part::Feature] Part__Feature007  label="lead"
  Placement = pos=(-1.85,-0.425,0) rot=(0,0,1;0rad)
  shape: bbox 0.8 x 0.85 x 0.2 mm, 6 faces (baked)
FEATURE [Part::Feature] Part__Feature008  label="lead001"
  Placement = pos=(1.85,0.425,0) rot=(0,0,1;3.14159rad)
  shape: bbox 0.8 x 0.85 x 0.2 mm, 6 faces (baked)
FEATURE [App::Part] _279795424  label="8279795424"
  Group = -> [Body009,Part__Feature007,Part__Feature008]
  Origin = -> Origin105
  Placement = pos=(4,2,0) rot=(0,0,1;0rad)
FEATURE [App::Part] SOD123FL
  Group = -> [_279795424]
  Origin = -> Origin104
  Placement = pos=(11.5642,15.379,0) rot=(0,0,-1;1.5708rad)
FEATURE [App::Part] D1
  Group = -> [SOD123FL]
  Origin = -> Origin103
FEATURE [Part::Feature] Part__Feature009  label="RES-0402"
  Placement = pos=(19.2067,10.5539,0) rot=(0,0,1;3.14159rad)
  shape: bbox 1 x 0.5 x 0.3375 mm, 36 faces (baked)
FEATURE [App::Part] R25
  Group = -> [Part__Feature009]
  Origin = -> Origin107
FEATURE [Part::Feature] Part__Feature010  label="Open CASCADE STEP translator 6.8 13.1.1"
  shape: bbox 1.44 x 3.11 x 1.14 mm, 58 faces (baked)
FEATURE [App::Part] Body010
  Group = -> [Part__Feature010]
  Origin = -> Origin108
  Placement = pos=(-0.715,-1.55,0) rot=(0,0,1;0rad)
FEATURE [Part::Feature] Part__Feature011  label="Leader"
  Placement = pos=(-0.715,-0.95,0) rot=(0,0,1;3.14159rad)
  shape: bbox 0.585 x 0.45 x 0.63 mm, 22 faces (baked)
FEATURE [Part::Feature] Part__Feature012  label="Leader001"
  Placement = pos=(-0.715,0.95,0) rot=(0,0,1;3.14159rad)
  shape: bbox 0.585 x 0.45 x 0.63 mm, 22 faces (baked)
FEATURE [Part::Feature] Part__Feature013  label="Leader002"
  Placement = pos=(0.715,0,0) rot=(0,0,1;0rad)
  shape: bbox 0.585 x 0.45 x 0.63 mm, 22 faces (baked)
FEATURE [App::Part] _734649824  label="6734649824"
  Group = -> [Body010,Part__Feature011,Part__Feature012,Part__Feature013]
  Origin = -> Origin013
  Placement = pos=(16.5073,9.46363,0) rot=(0,0,1;1.5708rad)
FEATURE [App::Part] Q2
  Group = -> [_734649824]
  Origin = -> Origin014
FEATURE [Part::Feature] Part__Feature014  label="Extruded001"
  shape: bbox 1.75 x 0.95 x 0.23 mm, 6 faces (baked)
FEATURE [App::Part] _855924865  label="6855924864001"
  Group = -> [Part__Feature014]
  Origin = -> Origin015
  Placement = pos=(7.58,7.29,0) rot=(0,0,1;0rad)
FEATURE [App::Part] Z2
  Group = -> [_855924865]
  Origin = -> Origin016
FEATURE [Part::Feature] Part__Feature015  label="Extruded002"
  shape: bbox 1.75 x 0.95 x 0.23 mm, 6 faces (baked)
FEATURE [App::Part] _855924866  label="6855924864002"
  Group = -> [Part__Feature015]
  Origin = -> Origin017
  Placement = pos=(7.58,9.09,0) rot=(0,0,1;0rad)
FEATURE [App::Part] Z1
  Group = -> [_855924866]
  Origin = -> Origin018
FEATURE [Part::Feature] Part__Feature016  label="RES-0403"
  Placement = pos=(10.8563,13.9862,0) rot=(0,0,1;3.14159rad)
  shape: bbox 1 x 0.5 x 0.3375 mm, 36 faces (baked)
FEATURE [App::Part] R23
  Group = -> [Part__Feature016]
  Origin = -> Origin019
FEATURE [Part::Feature] Part__Feature017  label="RES-0404"
  Placement = pos=(10.8563,12.1424,0) rot=(0,0,1;3.14159rad)
  shape: bbox 1 x 0.5 x 0.3375 mm, 36 faces (baked)
FEATURE [App::Part] R22
  Group = -> [Part__Feature017]
  Origin = -> Origin020
FEATURE [Part::Feature] Part__Feature018  label="RES-0405"
  Placement = pos=(10.8563,13.0642,0) rot=(0,0,1;3.14159rad)
  shape: bbox 1 x 0.5 x 0.3375 mm, 36 faces (baked)
FEATURE [App::Part] R20
  Group = -> [Part__Feature018]
  Origin = -> Origin021
FEATURE [Part::Feature] Part__Feature019  label="Extruded003"
  shape: bbox 0.15 x 0.3 x 0.57 mm, 6 faces (baked)
FEATURE [App::Part] _855929024  label="6855929024"
  Group = -> [Part__Feature019]
  Origin = -> Origin022
  Placement = pos=(8.7574,12.1158,0.0499999) rot=(0,0,1;0rad)
FEATURE [Part::Feature] Part__Feature020  label="Extruded004"
  shape: bbox 0.15 x 0.3 x 0.13 mm, 6 faces (baked)
FEATURE [App::Part] _855929184  label="6855929184"
  Group = -> [Part__Feature020]
  Origin = -> Origin023
  Placement = pos=(8.4174,12.1158,0.499999) rot=(0,0,1;0rad)
FEATURE [Part::Feature] Part__Feature021  label="Extruded005"
  shape: bbox 0.3 x 0.15 x 0.57 mm, 6 faces (baked)
FEATURE [App::Part] _855929344  label="6855929344"
  Group = -> [Part__Feature021]
  Origin = -> Origin024
  Placement = pos=(8.5974,12.4758,0.0499999) rot=(0,0,1;0rad)
FEATURE [Part::Feature] Part__Feature022  label="Extruded006"
  shape: bbox 1 x 1 x 0.6 mm, 6 faces (baked)
FEATURE [App::Part] _855929504  label="6855929504"
  Group = -> [Part__Feature022]
  Origin = -> Origin025
  Placement = pos=(8.5974,12.2758,0) rot=(0,0,1;0rad)
FEATURE [App::Part] DL1
  Group = -> [_855929024,_855929184,_855929344,_855929504]
  Origin = -> Origin026
FEATURE [Part::Feature] Part__Feature023  label="CAP-0604"
  Placement = pos=(19.1793,13.0283,0) rot=(0,0,1;1.5708rad)
  shape: bbox 0.8 x 1.6 x 0.8 mm, 58 faces (baked)
FEATURE [App::Part] C12
  Group = -> [Part__Feature023]
  Origin = -> Origin027
FEATURE [Part::Feature] Part__Feature024  label="sot25"
  Placement = pos=(17.4624,14.0659,0) rot=(0,0.707107,0.707107;3.14159rad)
  shape: bbox 2.4 x 3 x 1.15 mm, 75 faces (baked)
FEATURE [App::Part] U3
  Group = -> [Part__Feature024]
  Origin = -> Origin028
FEATURE [Part::Feature] Part__Feature025  label="CAP-0605"
  Placement = pos=(13.5642,14.528,0) rot=(0,0,0.991678;0rad)
  shape: bbox 1.6 x 0.8 x 0.8 mm, 58 faces (baked)
FEATURE [App::Part] C11
  Group = -> [Part__Feature025]
  Origin = -> Origin029
FEATURE [Part::Feature] Part__Feature026  label="RES-0406"
  Placement = pos=(40.3,3.53208,0) rot=(0,0,-1;1.5708rad)
  shape: bbox 0.5 x 1 x 0.3375 mm, 36 faces (baked)
FEATURE [App::Part] R19
  Group = -> [Part__Feature026]
  Origin = -> Origin030
FEATURE [Part::Feature] Part__Feature027  label="RES-0407"
  Placement = pos=(38.46,3.53208,0) rot=(0,0,1;1.5708rad)
  shape: bbox 0.5 x 1 x 0.3375 mm, 36 faces (baked)
FEATURE [App::Part] R17
  Group = -> [Part__Feature027]
  Origin = -> Origin031
FEATURE [Part::Feature] Part__Feature028  label="RES-0408"
  Placement = pos=(33.5665,3.53208,0) rot=(0,0,1;1.5708rad)
  shape: bbox 0.5 x 1 x 0.3375 mm, 36 faces (baked)
FEATURE [App::Part] R16
  Group = -> [Part__Feature028]
  Origin = -> Origin032
FEATURE [Part::Feature] Part__Feature029  label="RES-0409"
  Placement = pos=(39.38,3.53208,0) rot=(0,0,1;1.5708rad)
  shape: bbox 0.5 x 1 x 0.3375 mm, 36 faces (baked)
FEATURE [App::Part] R15
  Group = -> [Part__Feature029]
  Origin = -> Origin033
FEATURE [Part::Feature] Part__Feature030  label="SOT-024"
  Placement = pos=(39.2471,13.5591,0.499999) rot=(0,0.707107,0.707107;3.14159rad)
  shape: bbox 3 x 2.5 x 1.1 mm, 49 faces (baked)
FEATURE [App::Part] Q3
  Group = -> [Part__Feature030]
  Origin = -> Origin034
FEATURE [Part::Feature] Part__Feature031  label="SM04B-SRSS-TB_RGB12040119"
  Placement = pos=(38.877,8.875,-0.279999) rot=(0.57735,0.57735,0.57735;2.0944rad)
  shape: bbox 4.95 x 6 x 2.96 mm, 89 faces (baked)
FEATURE [App::Part] J2
  Group = -> [Part__Feature031]
  Origin = -> Origin035
FEATURE [Part::Feature] Part__Feature032  label="Open CASCADE STEP translator 6.8 6.1.1"
  shape: bbox 0.2 x 2.15 x 1 mm, 18 faces (baked)
FEATURE [Part::Feature] Part__Feature033  label="Open CASCADE STEP translator 6.8 6.1.2"
  shape: bbox 0.2 x 2.15 x 1 mm, 18 faces (baked)
FEATURE [App::Part] Terminal
  Group = -> [Part__Feature032,Part__Feature033]
  Origin = -> Origin036
  Placement = pos=(-1.325,-1.075,0) rot=(0,0,1;0rad)
FEATURE [Part::Feature] Part__Feature034  label="Open CASCADE STEP translator 6.8 6.2.1"
  shape: bbox 2.25 x 2.15 x 1 mm, 10 faces (baked)
FEATURE [App::Part] Mid_Body
  Group = -> [Part__Feature034]
  Origin = -> Origin037
  Placement = pos=(-1.325,-1.075,0) rot=(0,0,1;0rad)
FEATURE [App::Part] _734648784  label="6734648784"
  Group = -> [Terminal,Mid_Body]
  Origin = -> Origin038
  Placement = pos=(16.4718,6.21749,0) rot=(0,0,1;1.5708rad)
FEATURE [App::Part] L3
  Group = -> [_734648784]
  Origin = -> Origin039
FEATURE [Part::Feature] Part__Feature035  label="quartz_3_2__2_5_16MHz v2"
  Placement = pos=(34.13,10.99,0) rot=(0,0,-1;1.5708rad)
  shape: bbox 2.5 x 3.2 x 0.8 mm, 115 faces (baked)
FEATURE [App::Part] Y1
  Group = -> [Part__Feature035]
  Origin = -> Origin040
FEATURE [Part::Feature] Part__Feature036  label="RES-0410"
  Placement = pos=(35.4065,3.53205,0) rot=(0,0,1;1.5708rad)
  shape: bbox 0.5 x 1 x 0.3375 mm, 36 faces (baked)
FEATURE [App::Part] R14
  Group = -> [Part__Feature036]
  Origin = -> Origin041
FEATURE [Part::Feature] Part__Feature037  label="RES-0411"
  Placement = pos=(34.4865,3.53205,0) rot=(0,0,-1;1.5708rad)
  shape: bbox 0.5 x 1 x 0.3375 mm, 36 faces (baked)
FEATURE [App::Part] R11
  Group = -> [Part__Feature037]
  Origin = -> Origin042
FEATURE [Part::Feature] Part__Feature038  label="RES-0412"
  Placement = pos=(21.7,14.7,0) rot=(0,0,1;0rad)
  shape: bbox 1 x 0.5 x 0.3375 mm, 36 faces (baked)
FEATURE [App::Part] R2
  Group = -> [Part__Feature038]
  Origin = -> Origin043
FEATURE [Part::Feature] Part__Feature039  label="RES-0413"
  Placement = pos=(19.2025,8.46753,0) rot=(0,0,1;3.14159rad)
  shape: bbox 1 x 0.5 x 0.3375 mm, 36 faces (baked)
FEATURE [App::Part] R1
  Group = -> [Part__Feature039]
  Origin = -> Origin044
FEATURE [Part::Feature] Part__Feature040  label="FER-0604"
  Placement = pos=(19.548,3.84062,0) rot=(0,0,-1;1.5708rad)
  shape: bbox 0.8 x 1.6 x 0.8 mm, 58 faces (baked)
FEATURE [App::Part] L2
  Group = -> [Part__Feature040]
  Origin = -> Origin045
FEATURE [Part::Feature] Part__Feature041  label="CAP-0606"
  Placement = pos=(35.346,6.49576,0) rot=(0,0,1;1.5708rad)
  shape: bbox 0.5 x 1 x 0.5 mm, 58 faces (baked)
FEATURE [App::Part] C10
  Group = -> [Part__Feature041]
  Origin = -> Origin046
FEATURE [Part::Feature] Part__Feature042  label="CAP-0607"
  Placement = pos=(34.426,6.49576,0) rot=(0,0,1;1.5708rad)
  shape: bbox 0.5 x 1 x 0.5 mm, 58 faces (baked)
FEATURE [App::Part] C9
  Group = -> [Part__Feature042]
  Origin = -> Origin047
FEATURE [Part::Feature] Part__Feature043  label="CAP-0608"
  Placement = pos=(18.4971,6.62667,0) rot=(0,0,1;1.5708rad)
  shape: bbox 0.5 x 1 x 0.5 mm, 58 faces (baked)
FEATURE [App::Part] C8
  Group = -> [Part__Feature043]
  Origin = -> Origin048
FEATURE [Part::Feature] Part__Feature044  label="CAP-0609"
  Placement = pos=(18.4871,3.842,0) rot=(0,0,-1;1.5708rad)
  shape: bbox 0.5 x 1 x 0.5 mm, 58 faces (baked)
FEATURE [App::Part] C7
  Group = -> [Part__Feature044]
  Origin = -> Origin049
FEATURE [Part::Feature] Part__Feature045  label="CAP-0610"
  Placement = pos=(32.5465,14.1061,0) rot=(0,0,1;1.5708rad)
  shape: bbox 0.5 x 1 x 0.5 mm, 58 faces (baked)
FEATURE [App::Part] C6
  Group = -> [Part__Feature045]
  Origin = -> Origin050
FEATURE [Part::Feature] Part__Feature046  label="CAP-0611"
  Placement = pos=(33.4665,14.1061,0) rot=(0,0,1;1.5708rad)
  shape: bbox 0.5 x 1 x 0.5 mm, 58 faces (baked)
FEATURE [App::Part] C5
  Group = -> [Part__Feature046]
  Origin = -> Origin051
FEATURE [Part::Feature] Part__Feature047  label="CAP-0612"
  Placement = pos=(19.2067,9.42267,0) rot=(0,0,1;3.14159rad)
  shape: bbox 1 x 0.5 x 0.5 mm, 58 faces (baked)
FEATURE [App::Part] C4
  Group = -> [Part__Feature047]
  Origin = -> Origin052
FEATURE [Part::Feature] Part__Feature048  label="CAP-0613"
  Placement = pos=(39.8346,4.87242,0) rot=(0,0,0.991678;0rad)
  shape: bbox 1 x 0.5 x 0.5 mm, 58 faces (baked)
FEATURE [App::Part] C3
  Group = -> [Part__Feature048]
  Origin = -> Origin053
FEATURE [Part::Feature] Part__Feature049  label="CAP-0614"
  Placement = pos=(34.0482,12.305,0) rot=(0,0,1;1.5708rad)
  shape: bbox 0.5 x 1 x 0.5 mm, 58 faces (baked)
FEATURE [App::Part] C2
  Group = -> [Part__Feature049]
  Origin = -> Origin054
FEATURE [Part::Feature] Part__Feature050  label="Open CASCADE STEP translator 6.8 23.1.1"
  shape: bbox 10 x 10 x 1.65 mm, 117 faces (baked)
FEATURE [App::Part] Body011
  Group = -> [Part__Feature050]
  Origin = -> Origin055
  Placement = pos=(-5,-5,0) rot=(0,0,1;0rad)
FEATURE [Part::Feature] Part__Feature051  label="Leader003"
  Placement = pos=(-5,-3.75,0) rot=(0,0,1;3.14159rad)
  shape: bbox 1.1 x 0.27 x 0.875 mm, 22 faces (baked)
FEATURE [Part::Feature] Part__Feature052  label="Leader004"
  Placement = pos=(-3.75,5,0) rot=(0,0,1;1.5708rad)
  shape: bbox 0.27 x 1.1 x 0.875 mm, 22 faces (baked)
FEATURE [Part::Feature] Part__Feature053  label="Leader005"
  Placement = pos=(5,-3.75,0) rot=(0,0,1;0rad)
  shape: bbox 1.1 x 0.27 x 0.875 mm, 22 faces (baked)
FEATURE [Part::Feature] Part__Feature054  label="Leader006"
  Placement = pos=(-3.75,-5,0) rot=(0,0,-1;1.5708rad)
  shape: bbox 0.27 x 1.1 x 0.875 mm, 22 faces (baked)
FEATURE [Part::Feature] Part__Feature055  label="Leader007"
  Placement = pos=(-5,-3.25,0) rot=(0,0,1;3.14159rad)
  shape: bbox 1.1 x 0.27 x 0.875 mm, 22 faces (baked)
FEATURE [Part::Feature] Part__Feature056  label="Leader008"
  Placement = pos=(-3.25,5,0) rot=(0,0,1;1.5708rad)
  shape: bbox 0.27 x 1.1 x 0.875 mm, 22 faces (baked)
FEATURE [Part::Feature] Part__Feature057  label="Leader009"
  Placement = pos=(5,-3.25,0) rot=(0,0,1;0rad)
  shape: bbox 1.1 x 0.27 x 0.875 mm, 22 faces (baked)
FEATURE [Part::Feature] Part__Feature058  label="Leader010"
  Placement = pos=(-3.25,-5,0) rot=(0,0,-1;1.5708rad)
  shape: bbox 0.27 x 1.1 x 0.875 mm, 22 faces (baked)
FEATURE [Part::Feature] Part__Feature059  label="Leader011"
  Placement = pos=(-5,-2.75,0) rot=(0,0,1;3.14159rad)
  shape: bbox 1.1 x 0.27 x 0.875 mm, 22 faces (baked)
FEATURE [Part::Feature] Part__Feature060  label="Leader012"
  Placement = pos=(-2.75,5,0) rot=(0,0,1;1.5708rad)
  shape: bbox 0.27 x 1.1 x 0.875 mm, 22 faces (baked)
FEATURE [Part::Feature] Part__Feature061  label="Leader013"
  Placement = pos=(5,-2.75,0) rot=(0,0,1;0rad)
  shape: bbox 1.1 x 0.27 x 0.875 mm, 22 faces (baked)
FEATURE [Part::Feature] Part__Feature062  label="Leader014"
  Placement = pos=(-2.75,-5,0) rot=(0,0,-1;1.5708rad)
  shape: bbox 0.27 x 1.1 x 0.875 mm, 22 faces (baked)
FEATURE [Part::Feature] Part__Feature063  label="Leader015"
  Placement = pos=(-5,-2.25,0) rot=(0,0,1;3.14159rad)
  shape: bbox 1.1 x 0.27 x 0.875 mm, 22 faces (baked)
FEATURE [Part::Feature] Part__Feature064  label="Leader016"
  Placement = pos=(-2.25,5,0) rot=(0,0,1;1.5708rad)
  shape: bbox 0.27 x 1.1 x 0.875 mm, 22 faces (baked)
FEATURE [Part::Feature] Part__Feature065  label="Leader017"
  Placement = pos=(5,-2.25,0) rot=(0,0,1;0rad)
  shape: bbox 1.1 x 0.27 x 0.875 mm, 22 faces (baked)
FEATURE [Part::Feature] Part__Feature066  label="Leader018"
  Placement = pos=(-2.25,-5,0) rot=(0,0,-1;1.5708rad)
  shape: bbox 0.27 x 1.1 x 0.875 mm, 22 faces (baked)
FEATURE [Part::Feature] Part__Feature067  label="Leader019"
  Placement = pos=(-5,-1.75,0) rot=(0,0,1;3.14159rad)
  shape: bbox 1.1 x 0.27 x 0.875 mm, 22 faces (baked)
FEATURE [Part::Feature] Part__Feature068  label="Leader020"
  Placement = pos=(-1.75,5,0) rot=(0,0,1;1.5708rad)
  shape: bbox 0.27 x 1.1 x 0.875 mm, 22 faces (baked)
FEATURE [Part::Feature] Part__Feature069  label="Leader021"
  Placement = pos=(5,-1.75,0) rot=(0,0,1;0rad)
  shape: bbox 1.1 x 0.27 x 0.875 mm, 22 faces (baked)
FEATURE [Part::Feature] Part__Feature070  label="Leader022"
  Placement = pos=(-1.75,-5,0) rot=(0,0,-1;1.5708rad)
  shape: bbox 0.27 x 1.1 x 0.875 mm, 22 faces (baked)
FEATURE [Part::Feature] Part__Feature071  label="Leader023"
  Placement = pos=(-5,-1.25,0) rot=(0,0,1;3.14159rad)
  shape: bbox 1.1 x 0.27 x 0.875 mm, 22 faces (baked)
FEATURE [Part::Feature] Part__Feature072  label="Leader024"
  Placement = pos=(-1.25,5,0) rot=(0,0,1;1.5708rad)
  shape: bbox 0.27 x 1.1 x 0.875 mm, 22 faces (baked)
FEATURE [Part::Feature] Part__Feature073  label="Leader025"
  Placement = pos=(5,-1.25,0) rot=(0,0,1;0rad)
  shape: bbox 1.1 x 0.27 x 0.875 mm, 22 faces (baked)
FEATURE [Part::Feature] Part__Feature074  label="Leader026"
  Placement = pos=(-1.25,-5,0) rot=(0,0,-1;1.5708rad)
  shape: bbox 0.27 x 1.1 x 0.875 mm, 22 faces (baked)
FEATURE [Part::Feature] Part__Feature075  label="Leader027"
  Placement = pos=(-5,-0.75,0) rot=(0,0,1;3.14159rad)
  shape: bbox 1.1 x 0.27 x 0.875 mm, 22 faces (baked)
FEATURE [Part::Feature] Part__Feature076  label="Leader028"
  Placement = pos=(-0.75,5,0) rot=(0,0,1;1.5708rad)
  shape: bbox 0.27 x 1.1 x 0.875 mm, 22 faces (baked)
FEATURE [Part::Feature] Part__Feature077  label="Leader029"
  Placement = pos=(5,-0.75,0) rot=(0,0,1;0rad)
  shape: bbox 1.1 x 0.27 x 0.875 mm, 22 faces (baked)
FEATURE [Part::Feature] Part__Feature078  label="Leader030"
  Placement = pos=(-0.75,-5,0) rot=(0,0,-1;1.5708rad)
  shape: bbox 0.27 x 1.1 x 0.875 mm, 22 faces (baked)
FEATURE [Part::Feature] Part__Feature079  label="Leader031"
  Placement = pos=(-5,-0.25,0) rot=(0,0,1;3.14159rad)
  shape: bbox 1.1 x 0.27 x 0.875 mm, 22 faces (baked)
FEATURE [Part::Feature] Part__Feature080  label="Leader032"
  Placement = pos=(-0.25,5,0) rot=(0,0,1;1.5708rad)
  shape: bbox 0.27 x 1.1 x 0.875 mm, 22 faces (baked)
FEATURE [Part::Feature] Part__Feature081  label="Leader033"
  Placement = pos=(5,-0.25,0) rot=(0,0,1;0rad)
  shape: bbox 1.1 x 0.27 x 0.875 mm, 22 faces (baked)
FEATURE [Part::Feature] Part__Feature082  label="Leader034"
  Placement = pos=(-0.25,-5,0) rot=(0,0,-1;1.5708rad)
  shape: bbox 0.27 x 1.1 x 0.875 mm, 22 faces (baked)
FEATURE [Part::Feature] Part__Feature083  label="Leader035"
  Placement = pos=(-5,0.25,0) rot=(0,0,1;3.14159rad)
  shape: bbox 1.1 x 0.27 x 0.875 mm, 22 faces (baked)
FEATURE [Part::Feature] Part__Feature084  label="Leader036"
  Placement = pos=(0.25,5,0) rot=(0,0,1;1.5708rad)
  shape: bbox 0.27 x 1.1 x 0.875 mm, 22 faces (baked)
FEATURE [Part::Feature] Part__Feature085  label="Leader037"
  Placement = pos=(5,0.25,0) rot=(0,0,1;0rad)
  shape: bbox 1.1 x 0.27 x 0.875 mm, 22 faces (baked)
FEATURE [Part::Feature] Part__Feature086  label="Leader038"
  Placement = pos=(0.25,-5,0) rot=(0,0,-1;1.5708rad)
  shape: bbox 0.27 x 1.1 x 0.875 mm, 22 faces (baked)
FEATURE [Part::Feature] Part__Feature087  label="Leader039"
  Placement = pos=(-5,0.75,0) rot=(0,0,1;3.14159rad)
  shape: bbox 1.1 x 0.27 x 0.875 mm, 22 faces (baked)
FEATURE [Part::Feature] Part__Feature088  label="Leader040"
  Placement = pos=(0.75,5,0) rot=(0,0,1;1.5708rad)
  shape: bbox 0.27 x 1.1 x 0.875 mm, 22 faces (baked)
FEATURE [Part::Feature] Part__Feature089  label="Leader041"
  Placement = pos=(5,0.75,0) rot=(0,0,1;0rad)
  shape: bbox 1.1 x 0.27 x 0.875 mm, 22 faces (baked)
FEATURE [Part::Feature] Part__Feature090  label="Leader042"
  Placement = pos=(0.75,-5,0) rot=(0,0,-1;1.5708rad)
  shape: bbox 0.27 x 1.1 x 0.875 mm, 22 faces (baked)
FEATURE [Part::Feature] Part__Feature091  label="Leader043"
  Placement = pos=(-5,1.25,0) rot=(0,0,1;3.14159rad)
  shape: bbox 1.1 x 0.27 x 0.875 mm, 22 faces (baked)
FEATURE [Part::Feature] Part__Feature092  label="Leader044"
  Placement = pos=(1.25,5,0) rot=(0,0,1;1.5708rad)
  shape: bbox 0.27 x 1.1 x 0.875 mm, 22 faces (baked)
FEATURE [Part::Feature] Part__Feature093  label="Leader045"
  Placement = pos=(5,1.25,0) rot=(0,0,1;0rad)
  shape: bbox 1.1 x 0.27 x 0.875 mm, 22 faces (baked)
FEATURE [Part::Feature] Part__Feature094  label="Leader046"
  Placement = pos=(1.25,-5,0) rot=(0,0,-1;1.5708rad)
  shape: bbox 0.27 x 1.1 x 0.875 mm, 22 faces (baked)
FEATURE [Part::Feature] Part__Feature095  label="Leader047"
  Placement = pos=(-5,1.75,0) rot=(0,0,1;3.14159rad)
  shape: bbox 1.1 x 0.27 x 0.875 mm, 22 faces (baked)
FEATURE [Part::Feature] Part__Feature096  label="Leader048"
  Placement = pos=(1.75,5,0) rot=(0,0,1;1.5708rad)
  shape: bbox 0.27 x 1.1 x 0.875 mm, 22 faces (baked)
FEATURE [Part::Feature] Part__Feature097  label="Leader049"
  Placement = pos=(5,1.75,0) rot=(0,0,1;0rad)
  shape: bbox 1.1 x 0.27 x 0.875 mm, 22 faces (baked)
FEATURE [Part::Feature] Part__Feature098  label="Leader050"
  Placement = pos=(1.75,-5,0) rot=(0,0,-1;1.5708rad)
  shape: bbox 0.27 x 1.1 x 0.875 mm, 22 faces (baked)
FEATURE [Part::Feature] Part__Feature099  label="Leader051"
  Placement = pos=(-5,2.25,0) rot=(0,0,1;3.14159rad)
  shape: bbox 1.1 x 0.27 x 0.875 mm, 22 faces (baked)
FEATURE [Part::Feature] Part__Feature100  label="Leader052"
  Placement = pos=(2.25,5,0) rot=(0,0,1;1.5708rad)
  shape: bbox 0.27 x 1.1 x 0.875 mm, 22 faces (baked)
FEATURE [Part::Feature] Part__Feature101  label="Leader053"
  Placement = pos=(5,2.25,0) rot=(0,0,1;0rad)
  shape: bbox 1.1 x 0.27 x 0.875 mm, 22 faces (baked)
FEATURE [Part::Feature] Part__Feature102  label="Leader054"
  Placement = pos=(2.25,-5,0) rot=(0,0,-1;1.5708rad)
  shape: bbox 0.27 x 1.1 x 0.875 mm, 22 faces (baked)
FEATURE [Part::Feature] Part__Feature103  label="Leader055"
  Placement = pos=(-5,2.75,0) rot=(0,0,1;3.14159rad)
  shape: bbox 1.1 x 0.27 x 0.875 mm, 22 faces (baked)
FEATURE [Part::Feature] Part__Feature104  label="Leader056"
  Placement = pos=(2.75,5,0) rot=(0,0,1;1.5708rad)
  shape: bbox 0.27 x 1.1 x 0.875 mm, 22 faces (baked)
FEATURE [Part::Feature] Part__Feature105  label="Leader057"
  Placement = pos=(5,2.75,0) rot=(0,0,1;0rad)
  shape: bbox 1.1 x 0.27 x 0.875 mm, 22 faces (baked)
FEATURE [Part::Feature] Part__Feature106  label="Leader058"
  Placement = pos=(2.75,-5,0) rot=(0,0,-1;1.5708rad)
  shape: bbox 0.27 x 1.1 x 0.875 mm, 22 faces (baked)
FEATURE [Part::Feature] Part__Feature107  label="Leader059"
  Placement = pos=(-5,3.25,0) rot=(0,0,1;3.14159rad)
  shape: bbox 1.1 x 0.27 x 0.875 mm, 22 faces (baked)
FEATURE [Part::Feature] Part__Feature108  label="Leader060"
  Placement = pos=(3.25,5,0) rot=(0,0,1;1.5708rad)
  shape: bbox 0.27 x 1.1 x 0.875 mm, 22 faces (baked)
FEATURE [Part::Feature] Part__Feature109  label="Leader061"
  Placement = pos=(5,3.25,0) rot=(0,0,1;0rad)
  shape: bbox 1.1 x 0.27 x 0.875 mm, 22 faces (baked)
FEATURE [Part::Feature] Part__Feature110  label="Leader062"
  Placement = pos=(3.25,-5,0) rot=(0,0,-1;1.5708rad)
  shape: bbox 0.27 x 1.1 x 0.875 mm, 22 faces (baked)
FEATURE [Part::Feature] Part__Feature111  label="Leader063"
  Placement = pos=(-5,3.75,0) rot=(0,0,1;3.14159rad)
  shape: bbox 1.1 x 0.27 x 0.875 mm, 22 faces (baked)
FEATURE [Part::Feature] Part__Feature112  label="Leader064"
  Placement = pos=(3.75,5,0) rot=(0,0,1;1.5708rad)
  shape: bbox 0.27 x 1.1 x 0.875 mm, 22 faces (baked)
FEATURE [Part::Feature] Part__Feature113  label="Leader065"
  Placement = pos=(5,3.75,0) rot=(0,0,1;0rad)
  shape: bbox 1.1 x 0.27 x 0.875 mm, 22 faces (baked)
FEATURE [Part::Feature] Part__Feature114  label="Leader066"
  Placement = pos=(3.75,-5,0) rot=(0,0,-1;1.5708rad)
  shape: bbox 0.27 x 1.1 x 0.875 mm, 22 faces (baked)
FEATURE [App::Part] _422462560  label="6422462560"
  Group = -> [Body011,Part__Feature051,Part__Feature052,Part__Feature053,Part__Feature054,Part__Feature055,Part__Feature056,Part__Feature057,Part__Feature058,Part__Feature059,Part__Feature060,Part__Feature061,Part__Feature062,Part__Feature063,Part__Feature064,Part__Feature065,Part__Feature066,Part__Feature067,Part__Feature068,Part__Feature069,Part__Feature070,Part__Feature071,Part__Feature072,Part__Feature073,+41 more]
  Origin = -> Origin056
  Placement = pos=(12,10,0) rot=(0,0,1;0rad)
FEATURE [Part::Feature] Part__Feature115  label="Extruded007"
  shape: bbox 0.7002 x 0.7002 x 1.42 mm, 23 faces (baked)
FEATURE [App::Part] _219473552  label="7219473552"
  Group = -> [Part__Feature115]
  Origin = -> Origin057
  Placement = pos=(8.20008,13.7999,0.249999) rot=(0,0,1;0rad)
FEATURE [App::Part] Designator1
  Group = -> [_422462560,_219473552]
  Origin = -> Origin058
FEATURE [App::Part] RA4M1_v4  label="RA4M1 v4"
  Group = -> [Designator1]
  Origin = -> Origin059
  Placement = pos=(38.95,18.875,0) rot=(0,0,1;3.14159rad)
FEATURE [Part::Feature] Part__Feature116  label="Extruded008"
  shape: bbox 0.7002 x 0.7002 x 1.42 mm, 24 faces (baked)
FEATURE [App::Part] _325699712  label="7325699712"
  Group = -> [Part__Feature116]
  Origin = -> Origin060
  Placement = pos=(30.7499,5.07508,0.249999) rot=(0,0,1;0rad)
FEATURE [App::Part] U1
  Group = -> [RA4M1_v4,_325699712]
  Origin = -> Origin061
FEATURE [Part::Feature] Part__Feature117  label="RES-0414"
  Placement = pos=(5.64595,14.728,0) rot=(0,0,0.991678;0rad)
  shape: bbox 1 x 0.5 x 0.3375 mm, 36 faces (baked)
FEATURE [App::Part] R7
  Group = -> [Part__Feature117]
  Origin = -> Origin062
FEATURE [Part::Feature] Part__Feature118  label="RES-0415"
  Placement = pos=(35.3234,5.12704,0) rot=(0,0,1;3.14159rad)
  shape: bbox 1 x 0.5 x 0.3375 mm, 36 faces (baked)
FEATURE [App::Part] R13
  Group = -> [Part__Feature118]
  Origin = -> Origin063
FEATURE [Part::Feature] Part__Feature119  label="RES-0416"
  Placement = pos=(3.629,3.042,0) rot=(0,0,1;0rad)
  shape: bbox 1 x 0.5 x 0.3375 mm, 36 faces (baked)
FEATURE [App::Part] R9
  Group = -> [Part__Feature119]
  Origin = -> Origin064
FEATURE [Part::Feature] Part__Feature120  label="RES-0417"
  Placement = pos=(7.22626,3.93207,0) rot=(0,0,1;3.14159rad)
  shape: bbox 1 x 0.5 x 0.3375 mm, 36 faces (baked)
FEATURE [App::Part] R6
  Group = -> [Part__Feature120]
  Origin = -> Origin065
FEATURE [Part::Feature] Part__Feature121  label="RES-0418"
  Placement = pos=(7.22626,4.86207,0) rot=(0,0,1;3.14159rad)
  shape: bbox 1 x 0.5 x 0.3375 mm, 36 faces (baked)
FEATURE [App::Part] R5
  Group = -> [Part__Feature121]
  Origin = -> Origin066
FEATURE [Part::Feature] Part__Feature122  label="RES-0419"
  Placement = pos=(32.6465,3.53208,0) rot=(0,0,1;1.5708rad)
  shape: bbox 0.5 x 1 x 0.3375 mm, 36 faces (baked)
FEATURE [App::Part] R4
  Group = -> [Part__Feature122]
  Origin = -> Origin067
FEATURE [Part::Feature] Part__Feature123  label="RES-0420"
  Placement = pos=(7.35461,12.1629,0) rot=(0,0,1;1.5708rad)
  shape: bbox 0.5 x 1 x 0.3375 mm, 36 faces (baked)
FEATURE [App::Part] R3
  Group = -> [Part__Feature123]
  Origin = -> Origin068
FEATURE [Part::Feature] Part__Feature124  label="RES-0421"
  Placement = pos=(3.629,14.728,0) rot=(0,0,1;0rad)
  shape: bbox 1 x 0.5 x 0.3375 mm, 36 faces (baked)
FEATURE [App::Part] R8
  Group = -> [Part__Feature124]
  Origin = -> Origin069
FEATURE [Part::Feature] Part__Feature125  label="HSMx-190"
  Placement = pos=(1.40004,3.05,0) rot=(0,0,0.991678;0rad)
  shape: bbox 1.601 x 0.8052 x 0.7957 mm, 72 faces (baked)
FEATURE [App::Part] DL2
  Group = -> [Part__Feature125]
  Origin = -> Origin070
FEATURE [Part::Feature] Part__Feature126  label="CAP-0615"
  Placement = pos=(8.61119,4.38861,0) rot=(0,0,1;1.5708rad)
  shape: bbox 0.5 x 1 x 0.5 mm, 58 faces (baked)
FEATURE [App::Part] C22
  Group = -> [Part__Feature126]
  Origin = -> Origin071
FEATURE [Part::Feature] Part__Feature127  label="CAP-0616"
  Placement = pos=(9.75,4.77,0) rot=(0,0,-1;1.5708rad)
  shape: bbox 0.8 x 1.6 x 0.8 mm, 58 faces (baked)
FEATURE [App::Part] C23
  Group = -> [Part__Feature127]
  Origin = -> Origin072
FEATURE [Part::Feature] Part__Feature128  label="Open CASCADE STEP translator 6.8 19.1"
  Placement = pos=(-0.8,-1.05,0) rot=(0,0,1;0rad)
  shape: bbox 0.2 x 0.2 x 2e-07 mm, 1 faces, 0 solids (baked)
FEATURE [Part::Feature] Part__Feature129  label="Open CASCADE STEP translator 6.8 19.2.1"
  shape: bbox 1.6 x 2.1 x 0.9 mm, 8 faces (baked)
FEATURE [App::Part] Body012
  Group = -> [Part__Feature129]
  Origin = -> Origin073
  Placement = pos=(-0.8,-1.05,0) rot=(0,0,1;0rad)
FEATURE [Part::Feature] Part__Feature130  label="Open CASCADE STEP translator 6.8 19.3.1"
  shape: bbox 0.351 x 0.25 x 0.2 mm, 14 faces (baked)
FEATURE [App::Part] Pin_Shape
  Group = -> [Part__Feature130]
  Origin = -> Origin074
  Placement = pos=(-0.8,-0.875,0) rot=(0,0,1;0rad)
FEATURE [Part::Feature] Part__Feature131  label="Open CASCADE STEP translator 6.8 19.3.002"
  shape: bbox 0.351 x 0.25 x 0.2 mm, 14 faces (baked)
FEATURE [App::Part] Pin_Shape001
  Group = -> [Part__Feature131]
  Origin = -> Origin075
  Placement = pos=(0.8,0.875,0) rot=(0,0,1;3.14159rad)
FEATURE [Part::Feature] Part__Feature132  label="Open CASCADE STEP translator 6.8 19.3.003"
  shape: bbox 0.351 x 0.25 x 0.2 mm, 14 faces (baked)
FEATURE [App::Part] Pin_Shape002
  Group = -> [Part__Feature132]
  Origin = -> Origin076
  Placement = pos=(-0.8,-0.375,0) rot=(0,0,1;0rad)
FEATURE [Part::Feature] Part__Feature133  label="Open CASCADE STEP translator 6.8 19.3.004"
  shape: bbox 0.351 x 0.25 x 0.2 mm, 14 faces (baked)
FEATURE [App::Part] Pin_Shape003
  Group = -> [Part__Feature133]
  Origin = -> Origin077
  Placement = pos=(0.8,0.375,0) rot=(0,0,1;3.14159rad)
FEATURE [Part::Feature] Part__Feature134  label="Open CASCADE STEP translator 6.8 19.3.005"
  shape: bbox 0.351 x 0.25 x 0.2 mm, 14 faces (baked)
FEATURE [App::Part] Pin_Shape004
  Group = -> [Part__Feature134]
  Origin = -> Origin078
  Placement = pos=(-0.8,0.125,0) rot=(0,0,1;0rad)
FEATURE [Part::Feature] Part__Feature135  label="Open CASCADE STEP translator 6.8 19.3.006"
  shape: bbox 0.351 x 0.25 x 0.2 mm, 14 faces (baked)
FEATURE [App::Part] Pin_Shape005
  Group = -> [Part__Feature135]
  Origin = -> Origin079
  Placement = pos=(0.8,-0.125,0) rot=(0,0,1;3.14159rad)
FEATURE [Part::Feature] Part__Feature136  label="Open CASCADE STEP translator 6.8 19.3.007"
  shape: bbox 0.351 x 0.25 x 0.2 mm, 14 faces (baked)
FEATURE [App::Part] Pin_Shape006
  Group = -> [Part__Feature136]
  Origin = -> Origin080
  Placement = pos=(-0.8,0.625,0) rot=(0,0,1;0rad)
FEATURE [Part::Feature] Part__Feature137  label="Open CASCADE STEP translator 6.8 19.3.008"
  shape: bbox 0.351 x 0.25 x 0.2 mm, 14 faces (baked)
FEATURE [App::Part] Pin_Shape007
  Group = -> [Part__Feature137]
  Origin = -> Origin081
  Placement = pos=(0.8,-0.625,0) rot=(0,0,1;3.14159rad)
FEATURE [App::Part] _710435664  label="6710435664"
  Group = -> [Part__Feature128,Body012,Pin_Shape,Pin_Shape001,Pin_Shape002,Pin_Shape003,Pin_Shape004,Pin_Shape005,Pin_Shape006,Pin_Shape007]
  Origin = -> Origin082
  Placement = pos=(13.1183,4.89331,0) rot=(0,0,1;0rad)
FEATURE [App::Part] U2
  Group = -> [_710435664]
  Origin = -> Origin083
FEATURE [Part::Feature] Part__Feature138  label="CAP-0617"
  Placement = pos=(12.875,3.1975,0) rot=(0,0,1;3.14159rad)
  shape: bbox 1 x 0.5 x 0.5 mm, 58 faces (baked)
FEATURE [App::Part] C28
  Group = -> [Part__Feature138]
  Origin = -> Origin084
FEATURE [Part::Feature] Part__Feature139  label="CAP-0618"
  Placement = pos=(17.1,3.1975,0) rot=(0,0,1;0rad)
  shape: bbox 1 x 0.5 x 0.5 mm, 58 faces (baked)
FEATURE [App::Part] C25
  Group = -> [Part__Feature139]
  Origin = -> Origin085
FEATURE [Part::Feature] Part__Feature140  label="CAP-0619"
  Placement = pos=(14.7996,5.53043,0) rot=(0,0,-1;1.5708rad)
  shape: bbox 0.5 x 1 x 0.5 mm, 58 faces (baked)
FEATURE [App::Part] C20
  Group = -> [Part__Feature140]
  Origin = -> Origin086
FEATURE [Part::Feature] Part__Feature141  label="CAP-0620"
  Placement = pos=(13.5642,8.42444,0) rot=(0,0,1;0rad)
  shape: bbox 1.6 x 0.8 x 0.8 mm, 58 faces (baked)
FEATURE [App::Part] C27
  Group = -> [Part__Feature141]
  Origin = -> Origin087
FEATURE [Part::Feature] Part__Feature142  label="CAP-0621"
  Placement = pos=(13.5642,7.09443,0) rot=(0,0,1;0rad)
  shape: bbox 1.6 x 0.8 x 0.8 mm, 58 faces (baked)
FEATURE [App::Part] C26
  Group = -> [Part__Feature142]
  Origin = -> Origin088
FEATURE [Part::Feature] Part__Feature143  label="RES-0422"
  Placement = pos=(15.25,3.1975,0) rot=(0,0,1;0rad)
  shape: bbox 1 x 0.5 x 0.3375 mm, 36 faces (baked)
FEATURE [App::Part] R21
  Group = -> [Part__Feature143]
  Origin = -> Origin089
FEATURE [Part::Feature] Part__Feature144  label="RES-0423"
  Placement = pos=(17.1,4.149,0) rot=(0,0,0.991678;0rad)
  shape: bbox 1 x 0.5 x 0.3375 mm, 36 faces (baked)
FEATURE [App::Part] R18
  Group = -> [Part__Feature144]
  Origin = -> Origin090
FEATURE [Part::Feature] Part__Feature145  label="HSMx-191"
  Placement = pos=(1.4,14.73,0) rot=(0,0,0.991678;0rad)
  shape: bbox 1.601 x 0.8052 x 0.7957 mm, 72 faces (baked)
FEATURE [App::Part] DL3
  Group = -> [Part__Feature145]
  Origin = -> Origin091
FEATURE [Part::Feature] Part__Feature146  label="PTS820J20KSMTRLFS"
  Placement = pos=(10.7943,8.88999,0) rot=(0,0,1;1.5708rad)
  shape: bbox 2.9 x 4.5 x 2.005 mm, 253 faces (baked)
FEATURE [App::Part] PB1
  Group = -> [Part__Feature146]
  Origin = -> Origin092
FEATURE [Part::Feature] Part__Feature147  label="CX90B-16P_3D"
  Placement = pos=(0.25,-4.65,1.28) rot=(1,0,0;1.5708rad)
  shape: bbox 9.54 x 6.8 x 3.629 mm, 1192 faces (baked)
FEATURE [App::Part] CX90B_16P_CL0480_0755_0_00_3DDrawing_STEP_CX90B_16P_3D_48007525000_3D__STP  label="CX90B-16P_CL0480-0755-0-00_3DDrawing_STEP_CX90B-16P_3D_48007525000_3D_
STP"
  Group = -> [Part__Feature147]
  Origin = -> Origin093
  Placement = pos=(3.63805,8.89,0.309999) rot=(0,0,-1;1.5708rad)
FEATURE [App::Part] J1
  Group = -> [CX90B_16P_CL0480_0755_0_00_3DDrawing_STEP_CX90B_16P_3D_48007525000_3D__STP]
  Origin = -> Origin094
FEATURE [Part::Feature] Part__Feature148  label="CAP-0805"
  Placement = pos=(8.18914,14.0075,0) rot=(0,0,1;3.14159rad)
  shape: bbox 2 x 1.25 x 1.25 mm, 58 faces (baked)
FEATURE [App::Part] C16
  Group = -> [Part__Feature148]
  Origin = -> Origin095
FEATURE [PartDesign::CoordinateSystem] Nano_USB_Left
  AttacherType = Attacher::AttachEngine3D
  AttachmentOffset = pos=(0,0,0) rot=(0,0,-1;1.5708rad)
  AttachmentSupport = -> [Part__Feature]
  MapMode = 45
  Placement = pos=(1.27,1.27,2e-16) rot=(0,0,-1;1.5708rad)
FEATURE [App::Part] PCB
  Group = -> [Board,C1,L1,C24,Z3,Q1,D1,R25,Q2,Z2,Z1,R23,R22,R20,DL1,C12,U3,C11,R19,R17,R16,R15,Q3,J2,L3,Y1,R14,R11,R2,R1,L2,C10,C9,C8,C7,C6,C5,C4,C3,C2,U1,R7,R13,R9,R6,R5,R4,R3,R8,DL2,C22,C23,U2,C28,C25,C20,C27,C26,R21,R18,DL3,PB1,J1,C16,Nano_USB_Left]
  Origin = -> Origin096
  Placement = pos=(0,0,3) rot=(0,0,1;0rad)
FEATURE [Part::FeaturePython] Screw021  label="M5x40-Screw"  # WARN: FeaturePython — macro-defined, semantics opaque (R4)
  BaseObject = -> Body_Support [Pocket.Edge61]
  Diameter = 4
  Invert = false
  LeftHanded = false
  Length = 10
  LengthCustom = 40
  MatchOuter = false
  Offset = 1
  OffsetAngle = 0
  Placement = pos=(-1.17e-14,-1,-7.2e-15) rot=(1,0,0;1.5708rad)
  Thread = false
  Type = 43
FEATURE [Part::FeaturePython] Nut022  label="M5-Nut4878"  # WARN: FeaturePython — macro-defined, semantics opaque (R4)
  BaseObject = -> Screw021 [Edge73]
  Diameter = 7
  Invert = false
  LeftHanded = false
  MatchOuter = false
  Offset = 10
  OffsetAngle = 0
  Placement = pos=(-8.4e-15,29,-6e-16) rot=(1,0,0;1.5708rad)
  Thread = false
  Type = 31
FEATURE [Mesh::Feature] Mesh009  label="Body_Box_Arduino (Meshed)"
FEATURE [Sketcher::SketchObject] Sketch048
  ArcFitTolerance = 1e-06
  AttachmentSupport = -> [XZ_Plane110]
  ExternalTypes = [0]
  FullyConstrained = true
  MakeInternals = false
  MapMode = 5
  Placement = pos=(0,0,0) rot=(1,0,0;1.5708rad)
  _ExternalGeoVersion = 0
  sketch-geometry (6):
    g0: Circle CenterX=8.5 CenterY=-6.5 CenterZ=0 NormalX=0 NormalY=0 NormalZ=1 AngleXU=0 Radius=1.5
    g1: Circle CenterX=-8.5 CenterY=-6.5 CenterZ=0 NormalX=0 NormalY=0 NormalZ=1 AngleXU=0 Radius=1.5
    g2: Circle CenterX=-5.3 CenterY=-6.5 CenterZ=0 NormalX=0 NormalY=0 NormalZ=1 AngleXU=0 Radius=0.8
    g3: Circle CenterX=-2.8 CenterY=-6.5 CenterZ=0 NormalX=0 NormalY=0 NormalZ=1 AngleXU=0 Radius=0.8
    g4: Circle CenterX=2.8 CenterY=-6.5 CenterZ=0 NormalX=0 NormalY=0 NormalZ=1 AngleXU=0 Radius=0.8
    g5: Circle CenterX=5.3 CenterY=-6.5 CenterZ=0 NormalX=0 NormalY=0 NormalZ=1 AngleXU=0 Radius=0.8
  constraints (15):
    c: Equal(g0,g1)
    c: Equal(g5,g4)
    c: Equal(g4,g3)
    c: Equal(g3,g2)
    c: Symmetric(g0,g1,g-2)
    c: Diameter(g0) = 3
    c: DistanceX(g1,g0) = 17
    c: DistanceY(g0,g-1) = 6.5
    c: Diameter(g2) = 1.6
    c: Symmetric(g5,g2,g-2)
    c: Symmetric(g4,g3,g-2)
    c: DistanceX(g3,g4) = 5.6
    c: DistanceX(g2,g5) = 10.6
    c: DistanceY(g5,g-1) = 6.5
    c: DistanceY(g4,g-1) = 6.5
FEATURE [Sketcher::SketchObject] Sketch049
  ArcFitTolerance = 1e-06
  AttachmentSupport = -> [XZ_Plane110]
  ExternalTypes = [0]
  FullyConstrained = true
  MakeInternals = false
  MapMode = 5
  Placement = pos=(0,0,0) rot=(1,0,0;1.5708rad)
  _ExternalGeoVersion = 0
  sketch-geometry (4):
    g0: LineSegment StartX=-10 StartY=8 StartZ=0 EndX=-10 EndY=-8 EndZ=0
    g1: LineSegment StartX=-10 StartY=-8 StartZ=0 EndX=10 EndY=-8 EndZ=0
    g2: LineSegment StartX=10 StartY=-8 StartZ=0 EndX=10 EndY=8 EndZ=0
    g3: LineSegment StartX=10 StartY=8 StartZ=0 EndX=-10 EndY=8 EndZ=0
  constraints (11):
    c: Coincident(g0,g1)
    c: Coincident(g1,g2)
    c: Coincident(g2,g3)
    c: Coincident(g3,g0)
    c: Vertical(g0)
    c: Vertical(g2)
    c: Horizontal(g1)
    c: Horizontal(g3)
    c: Symmetric(g1,g0,g-1)
    c: DistanceY(g0,g0) = 16
    c: DistanceX(g1,g1) = 20
FEATURE [PartDesign::Pad] Pad030
  Direction = (0,-1,2e-16)
  Length = 64.5
  Length2 = 10
  Placement = pos=(0,0,0) rot=(1,0,0;1.5708rad)
  Profile = -> Sketch049
  ReferenceAxis = -> Sketch049 [N_Axis]
  Refine = true
  SideType = 0
  Suppressed = false
  Type = 0
  Type2 = 0
FEATURE [PartDesign::Fillet] Fillet007
  Base = -> Pad030 [Edge10,Edge4]
  BaseFeature = -> Pad030
  Placement = pos=(0,0,0) rot=(1,0,0;1.5708rad)
  Radius = 3
  Refine = true
  SupportTransform = false
  Suppressed = false
  UseAllEdges = false
FEATURE [PartDesign::Fillet] Fillet008
  Base = -> Fillet007 [Edge3,Edge13]
  BaseFeature = -> Fillet007
  Placement = pos=(0,0,0) rot=(1,0,0;1.5708rad)
  Radius = 9
  Refine = true
  SupportTransform = false
  Suppressed = false
  UseAllEdges = false
FEATURE [PartDesign::Pad] Pad031  label="Pad_Battery"
  BaseFeature = -> Fillet008
  Direction = (0,-1,2e-16)
  Length = 10
  Length2 = 10
  Placement = pos=(0,0,0) rot=(1,0,0;1.5708rad)
  Profile = -> Sketch048
  ReferenceAxis = -> Sketch048 [N_Axis]
  Refine = true
  SideType = 2
  Suppressed = false
  Type = 0
  Type2 = 0
FEATURE [PartDesign::CoordinateSystem] Battery
  AttacherType = Attacher::AttachEngine3D
  AttachmentSupport = -> [Pad031]
  MapMode = 45
  Placement = pos=(-7,-64.5,2.89e-14) rot=(0,0,1;0rad)
FEATURE [PartDesign::Body] Body014  label="Body_Battery_Tattu"
  AllowCompound = false
  Group = -> [Sketch049,Pad030,Fillet007,Fillet008,Sketch048,Pad031,Battery]
  Origin = -> Origin110
  Tip = -> Pad031
FEATURE [Sketcher::SketchObject] Sketch050
  ArcFitTolerance = 1e-06
  AttachmentSupport = -> [XY_Plane001]
  ExternalTypes = [0]
  FullyConstrained = true
  MakeInternals = false
  MapMode = 5
  _ExternalGeoVersion = 0
  sketch-geometry (2):
    g0: Circle CenterX=-27.5 CenterY=-5 CenterZ=0 NormalX=0 NormalY=0 NormalZ=1 AngleXU=0 Radius=2.3
    g1: Circle CenterX=27.5 CenterY=-5 CenterZ=0 NormalX=0 NormalY=0 NormalZ=1 AngleXU=0 Radius=2.3
  constraints (5):
    c: Equal(g1,g0)
    c: Diameter(g1) = 4.6
    c: DistanceX(g0,g1) = 55
    c: DistanceY(g1,g-1) = 5
    c: Symmetric(g1,g0,g-2)
FEATURE [PartDesign::Pocket] Pocket015
  BaseFeature = -> Pocket
  Direction = (0,0,-1)
  Length = 5
  Length2 = 5
  Placement = pos=(0,0,0) rot=(1,0,0;1.5708rad)
  Profile = -> Sketch050
  ReferenceAxis = -> Sketch050 [N_Axis]
  Refine = true
  Reversed = true
  SideType = 0
  Suppressed = false
  Type = 1
  Type2 = 0
FEATURE [PartDesign::Chamfer] Chamfer003
  Angle = 45
  Base = -> Pocket015 [Edge47,Edge40]
  BaseFeature = -> Pocket015
  ChamferType = 0
  FlipDirection = false
  Placement = pos=(0,0,0) rot=(1,0,0;1.5708rad)
  Refine = true
  Size = 1.5
  Size2 = 1
  SupportTransform = false
  Suppressed = false
  UseAllEdges = false
FEATURE [Sketcher::SketchObject] Sketch051
  ArcFitTolerance = 1e-06
  AttachmentSupport = -> [XY_Plane111]
  ExternalTypes = [0]
  FullyConstrained = true
  MakeInternals = false
  MapMode = 5
  _ExternalGeoVersion = 0
  sketch-geometry (1):
    g0: Circle CenterX=0 CenterY=55 CenterZ=0 NormalX=0 NormalY=0 NormalZ=1 AngleXU=0 Radius=2.3
  constraints (3):
    c: PointOnObject(g0,g-2)
    c: DistanceY(g-1,g0) = 55
    c: Diameter(g0) = 4.6
FEATURE [Sketcher::SketchObject] Sketch052
  ArcFitTolerance = 1e-06
  AttachmentSupport = -> [XY_Plane111]
  ExternalTypes = [0]
  FullyConstrained = true
  MakeInternals = false
  MapMode = 5
  _ExternalGeoVersion = 0
  sketch-geometry (1):
    g0: Circle CenterX=0 CenterY=0 CenterZ=0 NormalX=0 NormalY=0 NormalZ=1 AngleXU=0 Radius=62.5
  constraints (2):
    c: Coincident(g0,g-1)
    c: Diameter(g0) = 125
FEATURE [PartDesign::Pad] Pad032
  Direction = (0,0,1)
  Length = 3
  Length2 = 10
  Profile = -> Sketch052
  ReferenceAxis = -> Sketch052 [N_Axis]
  Refine = true
  SideType = 0
  Suppressed = false
  Type = 0
  Type2 = 0
FEATURE [PartDesign::Fillet] Fillet009
  Base = -> Pad032 [Edge3,Edge2]
  BaseFeature = -> Pad032
  Radius = 1.49
  Refine = true
  SupportTransform = false
  Suppressed = false
  UseAllEdges = false
FEATURE [PartDesign::Pocket] Pocket016
  BaseFeature = -> Fillet009
  Direction = (0,0,-1)
  Length = 5
  Length2 = 5
  Profile = -> Sketch051
  ReferenceAxis = -> Sketch051 [N_Axis]
  Refine = true
  Reversed = true
  SideType = 0
  Suppressed = false
  Type = 0
  Type2 = 0
FEATURE [PartDesign::PolarPattern] PolarPattern006
  Angle = 360
  Axis = -> Sketch051 [N_Axis]
  BaseFeature = -> Pocket016
  Mode = 0
  Occurrences = 6
  Offset = 120
  Originals = -> [Pocket016]
  Refine = true
  SpacingPattern = [0]
  Spacings = [-1,-1,-1,-1,-1]
  Suppressed = false
  TransformMode = 0
FEATURE [PartDesign::CoordinateSystem] Trepied
  AttacherType = Attacher::AttachEngine3D
  AttachmentOffset = pos=(0,0,0) rot=(0.707107,0.707107,0;3.14159rad)
  AttachmentSupport = -> [PolarPattern006]
  MapMode = 11
  Placement = pos=(-6.7e-15,-55,3) rot=(0,0,1;0rad)
FEATURE [PartDesign::CoordinateSystem] Support_Foot
  AttacherType = Attacher::AttachEngine3D
  AttachmentOffset = pos=(0,0,0) rot=(0.866025,-0.5,0;3.14159rad)
  AttachmentSupport = -> [Pocket015]
  MapMode = 11
  Placement = pos=(-27.5,-5,6) rot=(0,0,1;5.75959rad)
FEATURE [PartDesign::Fillet] Fillet010
  Base = -> Pocket015 [Edge31,Edge16,Edge13,Edge28]
  BaseFeature = -> Pocket015
  Placement = pos=(0,0,0) rot=(1,0,0;1.5708rad)
  Radius = 4.99
  Refine = true
  SupportTransform = false
  Suppressed = false
  UseAllEdges = false
FEATURE [PartDesign::Body] Body  label="Body_Support"
  AllowCompound = false
  Description = Pendulum
  Group = -> [Sketch,Pad,Sketch001,Pad001,Sketch002,Pad002,Sketch003,Pocket,Support,Sketch050,Pocket015,Chamfer003,Support_Foot,Fillet010]
  Origin = -> Origin001
  Tip = -> Fillet010
FEATURE [Part::FeaturePython] Screw026  label="M4x25-Screw"  # WARN: FeaturePython — macro-defined, semantics opaque (R4)
  BaseObject = -> Body_Support [Fillet010.Edge59]
  Diameter = 6
  Invert = true
  LeftHanded = false
  Length = 7
  LengthCustom = 25
  MatchOuter = false
  Offset = 1
  OffsetAngle = 0
  Placement = pos=(27.5,21.6,-19) rot=(0,0,1;0rad)
  Thread = false
  Type = 62
FEATURE [Part::FeaturePython] Screw027  label="M4x25-Screw058"  # WARN: FeaturePython — macro-defined, semantics opaque (R4)
  BaseObject = -> Body_Support [Fillet010.Edge44]
  Diameter = 6
  Invert = true
  LeftHanded = false
  Length = 7
  LengthCustom = 25
  MatchOuter = false
  Offset = 1
  OffsetAngle = 0
  Placement = pos=(-27.5,21.6,-19) rot=(0,0,1;0rad)
  Thread = false
  Type = 62
FEATURE [Part::FeaturePython] Nut027  label="M4-Nut236"  # WARN: FeaturePython — macro-defined, semantics opaque (R4)
  BaseObject = -> Screw027 [Edge1]
  Diameter = 6
  Invert = false
  LeftHanded = false
  MatchOuter = false
  Offset = 10
  OffsetAngle = 0
  Placement = pos=(-27.5,21.6,-34) rot=(0,0,1;0rad)
  Thread = false
  Type = 31
FEATURE [Part::FeaturePython] Nut028  label="M4-Nut235"  # WARN: FeaturePython — macro-defined, semantics opaque (R4)
  BaseObject = -> Screw026 [Edge1]
  Diameter = 6
  Invert = false
  LeftHanded = false
  MatchOuter = false
  Offset = 10
  OffsetAngle = 0
  Placement = pos=(27.5,21.6,-34) rot=(0,0,1;0rad)
  Thread = false
  Type = 31
FEATURE [Mesh::Feature] Mesh010  label="Body_Support (Meshed)"
FEATURE [Sketcher::SketchObject] Sketch053
  ArcFitTolerance = 1e-06
  AttachmentSupport = -> [PolarPattern006]
  ExternalTypes = [0]
  FullyConstrained = true
  MakeInternals = false
  MapMode = 5
  Placement = pos=(0,0,3) rot=(0,0,1;0rad)
  _ExternalGeoVersion = 0
  sketch-geometry (2):
    g0: Circle CenterX=0 CenterY=0 CenterZ=0 NormalX=0 NormalY=0 NormalZ=1 AngleXU=0 Radius=37
    g1: Circle CenterX=0 CenterY=0 CenterZ=0 NormalX=0 NormalY=0 NormalZ=1 AngleXU=0 Radius=35.3
  constraints (4):
    c: Coincident(g0,g-1)
    c: Diameter(g0) = 74
    c: Coincident(g1,g0)
    c: Diameter(g1) = 70.6
FEATURE [PartDesign::Pad] Pad033
  BaseFeature = -> PolarPattern006
  Direction = (0,0,1)
  Length = 60
  Length2 = 10
  Profile = -> Sketch053
  ReferenceAxis = -> Sketch053 [N_Axis]
  Refine = true
  Reversed = true
  SideType = 0
  Suppressed = false
  Type = 0
  Type2 = 0
FEATURE [Sketcher::SketchObject] Sketch054
  ArcFitTolerance = 1e-06
  AttachmentSupport = -> [XY_Plane112]
  ExternalTypes = [0]
  FullyConstrained = true
  MakeInternals = false
  MapMode = 5
  _ExternalGeoVersion = 0
  sketch-geometry (1):
    g0: Circle CenterX=0 CenterY=0 CenterZ=0 NormalX=0 NormalY=0 NormalZ=1 AngleXU=0 Radius=30
  constraints (2):
    c: Diameter(g0) = 60
    c: Coincident(g-1,g0)
FEATURE [PartDesign::Pad] Pad034
  Direction = (0,0,1)
  Length = 30
  Length2 = 10
  Profile = -> Sketch054
  ReferenceAxis = -> Sketch054 [N_Axis]
  Refine = true
  SideType = 0
  Suppressed = false
  Type = 0
  Type2 = 0
FEATURE [Sketcher::SketchObject] Sketch055
  ArcFitTolerance = 1e-06
  AttachmentSupport = -> [XZ_Plane112]
  ExternalGeometry = -> [Pad034]
  ExternalTypes = [0]
  FullyConstrained = true
  MakeInternals = false
  MapMode = 5
  Placement = pos=(0,0,0) rot=(1,0,0;1.5708rad)
  _ExternalGeoVersion = 0
  sketch-geometry (8):
    g0: LineSegment StartX=62.9979 StartY=30 StartZ=0 EndX=197.788 EndY=-162.501 EndZ=0
    g1: LineSegment StartX=197.788 StartY=-162.501 StartZ=0 EndX=157.788 EndY=-162.501 EndZ=0
    g2: LineSegment StartX=157.788 StartY=-162.501 StartZ=0 EndX=30 EndY=20 EndZ=0
    g3: LineSegment StartX=-157.788 StartY=-162.501 StartZ=0 EndX=-197.788 EndY=-162.501 EndZ=0
    g4: LineSegment StartX=-197.788 StartY=-162.501 StartZ=0 EndX=-62.9979 EndY=30 EndZ=0
    g5: LineSegment StartX=-62.9979 StartY=30 StartZ=0 EndX=62.9979 EndY=30 EndZ=0
    g6: LineSegment StartX=30 StartY=20 StartZ=0 EndX=-30 EndY=20 EndZ=0
    g7: LineSegment StartX=-30 StartY=20 StartZ=0 EndX=-157.788 EndY=-162.501 EndZ=0
  constraints (21):
    c: Coincident(g0,g1)
    c: Horizontal(g1)
    c: Coincident(g1,g2)
    c: Parallel(g0,g2)
    c: DistanceX(g1,g1) = 40
    c: Distance(g0) = 235
    c: Angle(g-1,g2) = 2.18166
    c: PointOnObject(g2,g-3)
    c: Horizontal(g3)
    c: Coincident(g3,g4)
    c: Coincident(g4,g5)
    c: Coincident(g6,g7)
    c: Coincident(g7,g3)
    c: Symmetric(g3,g1,g-2)
    c: DistanceX(g3,g3) = 40
    c: Symmetric(g4,g0,g-2)
    c: Symmetric(g6,g2,g-2)
    c: Coincident(g5,g0)
    c: Coincident(g6,g2)
    c: DistanceY(g6,g4) = 10
    c: PointOnObject(g-3,g5)
FEATURE [PartDesign::Pad] Pad035
  BaseFeature = -> Pad034
  Direction = (0,-1,2e-16)
  Length = 50
  Length2 = 10
  Profile = -> Sketch055
  ReferenceAxis = -> Sketch055 [N_Axis]
  Refine = true
  SideType = 2
  Suppressed = false
  Type = 0
  Type2 = 0
FEATURE [Sketcher::SketchObject] Sketch056
  ArcFitTolerance = 1e-06
  AttachmentSupport = -> [Pad035]
  ExternalTypes = [0]
  FullyConstrained = true
  MakeInternals = false
  MapMode = 5
  Placement = pos=(0,0,30) rot=(0,0,1;0rad)
  _ExternalGeoVersion = 0
  sketch-geometry (1):
    g0: Circle CenterX=0 CenterY=0 CenterZ=0 NormalX=0 NormalY=0 NormalZ=1 AngleXU=0 Radius=25.3
  constraints (2):
    c: Coincident(g0,g-1)
    c: Diameter(g0) = 50.6
FEATURE [Sketcher::SketchObject] Sketch057
  ArcFitTolerance = 1e-06
  AttachmentOffset = pos=(0,0,0) rot=(0,1,0;2.0944rad)
  AttachmentSupport = -> [XZ_Plane112]
  ExternalTypes = [0]
  FullyConstrained = true
  MakeInternals = false
  MapMode = 5
  Placement = pos=(0,0,0) rot=(0.377964,0.654654,0.654654;2.41886rad)
  _ExternalGeoVersion = 0
  sketch-geometry (6):
    g0: LineSegment StartX=0 StartY=30 StartZ=0 EndX=62.9979 EndY=30 EndZ=0
    g1: LineSegment StartX=62.9979 StartY=30 StartZ=0 EndX=197.788 EndY=-162.501 EndZ=0
    g2: LineSegment StartX=197.788 StartY=-162.501 StartZ=0 EndX=157.788 EndY=-162.501 EndZ=0
    g3: LineSegment StartX=157.788 StartY=-162.501 StartZ=0 EndX=30 EndY=20 EndZ=0
    g4: LineSegment StartX=30 StartY=20 StartZ=0 EndX=0 EndY=20 EndZ=0
    g5: LineSegment StartX=0 StartY=20 StartZ=0 EndX=0 EndY=30 EndZ=0
  constraints (18):
    c: PointOnObject(g0,g-2)
    c: Horizontal(g0)
    c: Coincident(g0,g1)
    c: Coincident(g1,g2)
    c: Horizontal(g2)
    c: Coincident(g2,g3)
    c: Coincident(g3,g4)
    c: Coincident(g4,g5)
    c: Coincident(g5,g0)
    c: Vertical(g5)
    c: Horizontal(g4)
    c: DistanceY(g5,g5) = 10
    c: DistanceX(g2,g2) = 40
    c: Angle(g-1,g3) = 2.18166
    c: Distance(g1) = 235
    c: Parallel(g3,g1)
    c: DistanceY(g-1,g4) = 20
    c: DistanceX(g4,g4) = 30
FEATURE [Sketcher::SketchObject] Sketch058
  ArcFitTolerance = 1e-06
  AttachmentOffset = pos=(0,0,0) rot=(0,1,0;1.0472rad)
  AttachmentSupport = -> [XZ_Plane112]
  ExternalTypes = [0]
  FullyConstrained = true
  MakeInternals = false
  MapMode = 5
  Placement = pos=(0,0,0) rot=(0.774597,0.447214,0.447214;1.82348rad)
  _ExternalGeoVersion = 0
  sketch-geometry (6):
    g0: LineSegment StartX=0 StartY=30 StartZ=0 EndX=62.9979 EndY=30 EndZ=0
    g1: LineSegment StartX=62.9979 StartY=30 StartZ=0 EndX=197.788 EndY=-162.501 EndZ=0
    g2: LineSegment StartX=197.788 StartY=-162.501 StartZ=0 EndX=157.788 EndY=-162.501 EndZ=0
    g3: LineSegment StartX=157.788 StartY=-162.501 StartZ=0 EndX=30 EndY=20 EndZ=0
    g4: LineSegment StartX=30 StartY=20 StartZ=0 EndX=0 EndY=20 EndZ=0
    g5: LineSegment StartX=0 StartY=20 StartZ=0 EndX=0 EndY=30 EndZ=0
  constraints (18):
    c: PointOnObject(g0,g-2)
    c: Horizontal(g0)
    c: Coincident(g0,g1)
    c: Coincident(g1,g2)
    c: Horizontal(g2)
    c: Coincident(g2,g3)
    c: Coincident(g3,g4)
    c: Coincident(g4,g5)
    c: Coincident(g5,g0)
    c: Vertical(g5)
    c: Horizontal(g4)
    c: DistanceY(g5,g5) = 10
    c: DistanceX(g2,g2) = 40
    c: Angle(g-1,g3) = 2.18166
    c: Distance(g1) = 235
    c: Parallel(g3,g1)
    c: DistanceY(g-1,g4) = 20
    c: DistanceX(g4,g4) = 30
FEATURE [Sketcher::SketchObject] Sketch059
  ArcFitTolerance = 1e-06
  AttachmentOffset = pos=(0,0,-163) rot=(0,0,1;0rad)
  AttachmentSupport = -> [XY_Plane112]
  ExternalTypes = [0]
  FullyConstrained = true
  MakeInternals = false
  MapMode = 5
  Placement = pos=(0,0,-163) rot=(0,0,1;0rad)
  _ExternalGeoVersion = 0
  sketch-geometry (6):
    g0: ArcOfCircle CenterX=0 CenterY=0 CenterZ=0 NormalX=0 NormalY=0 NormalZ=1 AngleXU=0 Radius=145 StartAngle=1.8326 EndAngle=3.40339
    g1: ArcOfCircle CenterX=0 CenterY=0 CenterZ=0 NormalX=0 NormalY=0 NormalZ=1 AngleXU=0 Radius=205 StartAngle=1.8326 EndAngle=3.40339
    g2: LineSegment [constr] StartX=0 StartY=0 StartZ=0 EndX=-212.504 EndY=-56.9402 EndZ=0
    g3: LineSegment [constr] StartX=0 StartY=0 StartZ=0 EndX=-56.9402 EndY=212.504 EndZ=0
    g4: ArcOfCircle CenterX=-169.037 CenterY=-45.2933 CenterZ=0 NormalX=0 NormalY=0 NormalZ=1 AngleXU=0 Radius=30 StartAngle=3.40339 EndAngle=6.54498
    g5: ArcOfCircle CenterX=-45.2933 CenterY=169.037 CenterZ=0 NormalX=0 NormalY=0 NormalZ=1 AngleXU=0 Radius=30 StartAngle=4.97419 EndAngle=8.11578
  constraints (20):
    c: Coincident(g0,g-1)
    c: Coincident(g2,g0)
    c: Coincident(g3,g1)
    c: Coincident(g1,g0)
    c: PointOnObject(g0,g2)
    c: PointOnObject(g1,g2)
    c: PointOnObject(g1,g3)
    c: Angle(g2,g-1) = 2.87979
    c: Angle(g-2,g3) = 0.261799
    c: Radius(g0) = 145
    c: Diameter(g5) = 60
    c: Coincident(g5,g1)
    c: Coincident(g5,g0)
    c: Diameter(g4) = 60
    c: Coincident(g4,g1)
    c: Coincident(g4,g0)
    c: PointOnObject(g4,g2)
    c: PointOnObject(g0,g3)
    c: Equal(g3,g2)
    c: Distance(g3) = 220
FEATURE [PartDesign::Pad] Pad036
  BaseFeature = -> Pad035
  Direction = (0,0,1)
  Length = 5
  Length2 = 10
  Profile = -> Sketch059
  ReferenceAxis = -> Sketch059 [N_Axis]
  Refine = true
  SideType = 0
  Suppressed = false
  Type = 0
  Type2 = 0
FEATURE [Sketcher::SketchObject] Sketch004
  ArcFitTolerance = 1e-06
  AttachmentSupport = -> [Pad036]
  ExternalGeometry = -> [Pad036]
  ExternalTypes = [0]
  FullyConstrained = true
  MakeInternals = false
  MapMode = 5
  Placement = pos=(0,0,-158) rot=(0,0,1;0rad)
  _ExternalGeoVersion = 0
  sketch-geometry (4):
    g0: ArcOfCircle CenterX=0 CenterY=0 CenterZ=0 NormalX=0 NormalY=0 NormalZ=1 AngleXU=0 Radius=145 StartAngle=6.02139 EndAngle=7.59218
    g1: ArcOfCircle CenterX=0 CenterY=0 CenterZ=0 NormalX=0 NormalY=0 NormalZ=1 AngleXU=0 Radius=205 StartAngle=6.02139 EndAngle=7.59218
    g2: ArcOfCircle CenterX=45.2933 CenterY=169.037 CenterZ=0 NormalX=0 NormalY=0 NormalZ=1 AngleXU=0 Radius=30 StartAngle=1.309 EndAngle=4.45059
    g3: ArcOfCircle CenterX=169.037 CenterY=-45.2933 CenterZ=0 NormalX=0 NormalY=0 NormalZ=1 AngleXU=0 Radius=30 StartAngle=2.87979 EndAngle=6.02139
  constraints (11):
    c: Coincident(g0,g-1)
    c: Coincident(g1,g0)
    c: Symmetric(g-3,g0,g-2)
    c: Symmetric(g1,g-3,g-2)
    c: Coincident(g2,g1)
    c: Coincident(g2,g0)
    c: Coincident(g3,g1)
    c: Coincident(g3,g0)
    c: Radius(g2) = 30
    c: Radius(g3) = 30
    c: Symmetric(g-4,g3,g-2)
FEATURE [PartDesign::Pad] Pad003
  BaseFeature = -> Pad036
  Direction = (0,0,1)
  Length = 5
  Length2 = 10
  Profile = -> Sketch004
  ReferenceAxis = -> Sketch004 [N_Axis]
  Refine = true
  Reversed = true
  SideType = 0
  Suppressed = false
  Type = 0
  Type2 = 0
FEATURE [PartDesign::Pad] Pad037
  BaseFeature = -> Pad003
  Direction = (0.866025,-0.5,1e-16)
  Length = 50
  Length2 = 10
  Profile = -> Sketch058
  ReferenceAxis = -> Sketch058 [N_Axis]
  Refine = true
  SideType = 2
  Suppressed = false
  Type = 0
  Type2 = 0
FEATURE [PartDesign::Pad] Pad038
  BaseFeature = -> Pad037
  Direction = (0.866025,0.5,-1e-16)
  Length = 50
  Length2 = 10
  Profile = -> Sketch057
  ReferenceAxis = -> Sketch057 [N_Axis]
  Refine = true
  SideType = 2
  Suppressed = false
  Type = 0
  Type2 = 0
FEATURE [PartDesign::Pocket] Pocket017
  BaseFeature = -> Pad038
  Direction = (0,0,-1)
  Length = 5
  Length2 = 5
  Profile = -> Sketch056
  ReferenceAxis = -> Sketch056 [N_Axis]
  Refine = true
  SideType = 0
  Suppressed = false
  Type = 1
  Type2 = 0
FEATURE [Sketcher::SketchObject] Sketch060
  ArcFitTolerance = 1e-06
  AttachmentSupport = -> [Pad003]
  ExternalTypes = [0]
  FullyConstrained = true
  MakeInternals = false
  MapMode = 5
  Placement = pos=(0,0,-158) rot=(0,0,1;0rad)
  _ExternalGeoVersion = 0
  sketch-geometry (5):
    g0: LineSegment StartX=-120.651 StartY=158.973 StartZ=0 EndX=-77.3494 EndY=183.973 EndZ=0
    g1: LineSegment StartX=-77.3494 StartY=183.973 StartZ=0 EndX=-57.3494 EndY=149.332 EndZ=0
    g2: LineSegment StartX=-57.3494 StartY=149.332 StartZ=0 EndX=-100.651 EndY=124.332 EndZ=0
    g3: LineSegment StartX=-100.651 StartY=124.332 StartZ=0 EndX=-120.651 EndY=158.973 EndZ=0
    g4: LineSegment [constr] StartX=0 StartY=0 StartZ=0 EndX=-115 EndY=199.186 EndZ=0
  constraints (13):
    c: Coincident(g0,g1)
    c: Coincident(g1,g2)
    c: Coincident(g2,g3)
    c: Coincident(g3,g0)
    c: Coincident(g4,g-1)
    c: Angle(g-1,g4) = 2.0944
    c: Symmetric(g0,g0,g4)
    c: Distance(g0) = 50
    c: Parallel(g1,g3)
    c: Distance(g3) = 40
    c: Distance(g4,g2) = 158
    c: Symmetric(g1,g2,g4)
    c: Distance(g4) = 230
FEATURE [PartDesign::CoordinateSystem] Pedestral_Top
  AttacherType = Attacher::AttachEngine3D
  AttachmentOffset = pos=(0,0,0) rot=(0,0,1;-0.523599rad)
  AttachmentSupport = -> [Pocket017]
  MapMode = 45
  Placement = pos=(1.208e-13,1.4e-15,30) rot=(0,0,1;5.75959rad)
FEATURE [PartDesign::Body] Body016  label="Body_Pedestral"
  AllowCompound = false
  Group = -> [Sketch054,Pad034,Sketch055,Pad035,Sketch056,Sketch059,Pad036,Sketch004,Pad003,Sketch060,Sketch058,Pad037,Sketch057,Pad038,Pocket017,Pedestral_Top]
  Origin = -> Origin112
  Tip = -> Pocket017
FEATURE [Sketcher::SketchObject] Sketch061
  ArcFitTolerance = 1e-06
  AttachmentSupport = -> [YZ_Plane113]
  ExternalTypes = [0]
  FullyConstrained = true
  MakeInternals = false
  MapMode = 5
  Placement = pos=(0,0,0) rot=(0.57735,0.57735,0.57735;2.0944rad)
  _ExternalGeoVersion = 0
  sketch-geometry (1):
    g0: Circle CenterX=0 CenterY=41 CenterZ=0 NormalX=0 NormalY=0 NormalZ=1 AngleXU=0 Radius=2.3
  constraints (3):
    c: PointOnObject(g0,g-2)
    c: Diameter(g0) = 4.6
    c: DistanceY(g-1,g0) = 41
FEATURE [Sketcher::SketchObject] Sketch062
  ArcFitTolerance = 1e-06
  AttachmentSupport = -> [XY_Plane113]
  ExternalTypes = [0]
  FullyConstrained = true
  MakeInternals = false
  MapMode = 5
  _ExternalGeoVersion = 0
  sketch-geometry (2):
    g0: Circle CenterX=0 CenterY=0 CenterZ=0 NormalX=0 NormalY=0 NormalZ=1 AngleXU=0 Radius=25
    g1: Circle CenterX=0 CenterY=0 CenterZ=0 NormalX=0 NormalY=0 NormalZ=1 AngleXU=0 Radius=23
  constraints (4):
    c: Coincident(g0,g-1)
    c: Coincident(g1,g0)
    c: Diameter(g1) = 46
    c: Diameter(g0) = 50
FEATURE [PartDesign::Pad] Pad039
  Direction = (0,0,1)
  Length = 70
  Length2 = 10
  Profile = -> Sketch062
  ReferenceAxis = -> Sketch062 [N_Axis]
  Refine = true
  SideType = 0
  Suppressed = false
  Type = 0
  Type2 = 0
FEATURE [PartDesign::Pocket] Pocket018
  BaseFeature = -> Pad039
  Direction = (-1,0,0)
  Length = 5
  Length2 = 5
  Profile = -> Sketch061
  ReferenceAxis = -> Sketch061 [N_Axis]
  Refine = true
  SideType = 0
  Suppressed = false
  Type = 1
  Type2 = 0
FEATURE [PartDesign::CoordinateSystem] Pedestral_Connector
  AttacherType = Attacher::AttachEngine3D
  AttachmentOffset = pos=(0,0,0) rot=(0,0,-1;1.5708rad)
  AttachmentSupport = -> [Pocket018]
  MapMode = 11
  Placement = pos=(0,0,70) rot=(0,0,1;0rad)
FEATURE [PartDesign::Body] Body017  label="Body_Pedestral_Connector"
  AllowCompound = false
  Group = -> [Sketch061,Sketch062,Pad039,Pocket018,Pedestral_Connector]
  Origin = -> Origin113
  Tip = -> Pocket018
FEATURE [Mesh::Feature] Mesh011  label="Body_BearingLock (Meshed)"
FEATURE [PartDesign::CoordinateSystem] Arm_Axis_Bottom
  AttacherType = Attacher::AttachEngine3D
  AttachmentSupport = -> [Pocket010]
  MapMode = 45
  Placement = pos=(4.26e-14,-84.8494,8) rot=(0,0,1;0rad)
FEATURE [PartDesign::Body] Body003  label="Body_Arm"
  AllowCompound = false
  Group = -> [Sketch007,Pad004,Sketch006,Pocket001,Arm_Axis_Top,Arm_MPU6050_Right,Chamfer002,Sketch027,Pad017,Sketch032,Pocket009,Sketch033,Pocket010,Arm_Axis_Bottom]
  Origin = -> Origin004
  Tip = -> Pocket010
FEATURE [Part::Feature] Part__Feature149  label="C_Disc_D5.0mm_W2.5mm_P5.00mm"
  Placement = pos=(-1,40.5,1.595) rot=(0,0,1;3.14159rad)
  shape: bbox 5.5 x 2.5 x 7.1 mm, 10 faces (baked)
FEATURE [Part::Feature] Part__Feature150  label="R_Axial_DIN0207_L6.3mm_D2.5mm_P7.62mm_Horizontal"
  Placement = pos=(2.69,31.5,1.595) rot=(0,0,1;0rad)
  shape: bbox 8.418 x 2.706 x 5.603 mm, 15 faces (baked)
FEATURE [Part::Feature] Part__Feature151  label="R_Axial_DIN0207_L6.3mm_D2.5mm_P7.62mm_Horizontal001"
  Placement = pos=(-8.62,24,1.595) rot=(0,0,1;0rad)
  shape: bbox 8.418 x 2.706 x 5.603 mm, 15 faces (baked)
FEATURE [Part::Feature] Part__Feature152  label="PinHeader_1x08_P2.54mm_Vertical"
  Placement = pos=(-14.5,14.42,1.595) rot=(0,0,1;3.14159rad)
  shape: bbox 2.54 x 20.32 x 11.54 mm, 196 faces (baked)
FEATURE [Part::Feature] Part__Feature153  label="TerminalBlock_Phoenix_MKDS-1,5-2_1x02_P5.00mm_Horizontal"
  Placement = pos=(26,38.1725,1.595) rot=(0,0,1;3.14159rad)
  shape: bbox 10.74 x 9.8 x 17.3 mm, 89 faces (baked)
FEATURE [Part::Feature] Part__Feature154  label="PinHeader_1x04_P2.54mm_Vertical"
  Placement = pos=(-7.5,6,1.595) rot=(0,0,-1;1.5708rad)
  shape: bbox 10.16 x 2.54 x 11.54 mm, 100 faces (baked)
FEATURE [Part::Feature] Part__Feature155  label="TO-92L_Inline"
  Placement = pos=(47,6.5,1.595) rot=(0,0,1;1.5708rad)
  shape: bbox 3.9 x 4.9 x 12.95 mm, 19 faces (baked)
FEATURE [Part::Feature] Part__Feature156  label="R_Axial_DIN0207_L6.3mm_D2.5mm_P7.62mm_Horizontal002"
  Placement = pos=(21.81,25,1.595) rot=(0,0,1;3.14159rad)
  shape: bbox 8.418 x 2.706 x 5.603 mm, 15 faces (baked)
FEATURE [Part::Feature] Part__Feature157  label="Buzzer_12x9.5RM7.6"
  Placement = pos=(40,31.1,1.595) rot=(0,0,-1;1.5708rad)
  shape: bbox 12.99 x 12.99 x 12.53 mm, 13 faces (baked)
FEATURE [Part::Feature] Part__Feature158  label="PinHeader_1x15_P2.54mm_Vertical"
  Placement = pos=(3.81,1.27,-0.085) rot=(0.707107,-0.707107,0;3.14159rad)
  shape: bbox 38.1 x 2.54 x 11.54 mm, 364 faces (baked)
FEATURE [Part::Feature] Part__Feature159  label="PinHeader_1x15_P2.54mm_Vertical001"
  Placement = pos=(3.81,16.51,-0.085) rot=(0.707107,-0.707107,0;3.14159rad)
  shape: bbox 38.1 x 2.54 x 11.54 mm, 364 faces (baked)
FEATURE [PartDesign::CoordinateSystem] main_circuit
  AttacherType = Attacher::AttachEngine3D
  AttachmentOffset = pos=(0,0,0) rot=(0,0,-1;1.5708rad)
  MapMode = 45
  Placement = pos=(-17.96,-2.96,1.51) rot=(0,0,1.00001;4e-06rad)
FEATURE [PartDesign::CoordinateSystem] circuit_PCB
  AttacherType = Attacher::AttachEngine3D
  MapMode = 45
  Placement = pos=(0,0,0.755) rot=(0,0,1;0rad)
FEATURE [App::Part] main_Circuit_kicad_Circuit_1  label="main_Circuit-kicad"
  Group = -> [Part__Feature149,Part__Feature150,Part__Feature151,Part__Feature152,Part__Feature153,Part__Feature154,Part__Feature155,Part__Feature156,Part__Feature157,Part__Feature158,Part__Feature159,main_circuit,circuit_PCB]
  Origin = -> Origin114
FEATURE [PartDesign::CoordinateSystem] Trepied_Bottom
  AttacherType = Attacher::AttachEngine3D
  AttachmentOffset = pos=(0,0,0) rot=(0,0,-1;0.523599rad)
  AttachmentSupport = -> [Pad033]
  MapMode = 45
  Placement = pos=(-47.6314,27.5,3) rot=(0,0,1;0.523595rad)
FEATURE [App::Link] Body_Trepied  label="Body_Trepied001"
  AttachedBy = #Trepied
  AttachedTo = Body_Support#Support_Foot
  AttachmentOffset = pos=(0,0,-6) rot=(0,0,1;0rad)
  LinkPlacement = pos=(1.42e-14,69.2314,-29) rot=(0,0,-1;0.523599rad)
  LinkedObject = -> Body015
  Placement = pos=(1.42e-14,69.2314,-29) rot=(0,0,-1;0.523599rad)
  SolverId = Asm4EE
  expr: Placement = Body_Support.Placement * Support_Foot.Placement * AttachmentOffset * Trepied.Placement ^ -1
FEATURE [PartDesign::CoordinateSystem] Trepied_Axial
  AttacherType = Attacher::AttachEngine3D
  AttachmentSupport = -> [Pad033]
  MapMode = 45
  Placement = pos=(1.683e-13,3.2e-15,-57) rot=(0,0,1;0rad)
FEATURE [PartDesign::Body] Body015  label="Body_Trepied"
  AllowCompound = false
  Group = -> [Sketch052,Pad032,Fillet009,Sketch051,Pocket016,PolarPattern006,Trepied,Sketch053,Pad033,Trepied_Bottom,Trepied_Axial]
  Origin = -> Origin111
  Tip = -> Pad033
FEATURE [App::Link] Body_Pedestral_Connector  label="Body_Pedestral_Connector001"
  AttachedBy = #Pedestral_Connector
  AttachedTo = Body_Trepied#Trepied_Axial
  AttachmentOffset = pos=(0,0,36) rot=(0,0,1;0rad)
  LinkPlacement = pos=(1.851e-13,69.2314,-120) rot=(0,0,-1;0.523599rad)
  LinkedObject = -> Body017
  Placement = pos=(1.851e-13,69.2314,-120) rot=(0,0,-1;0.523599rad)
  SolverId = Asm4EE
  expr: Placement = Body_Trepied.Placement * Trepied_Axial.Placement * AttachmentOffset * Pedestral_Connector.Placement ^ -1
FEATURE [App::Link] Body_Pedestral  label="Body_Pedestral001"
  AttachedBy = #Pedestral_Top
  AttachedTo = Body_Pedestral_Connector#Pedestral_Connector
  AttachmentOffset = pos=(0,0,-50) rot=(0,0,1;0rad)
  LinkPlacement = pos=(6.69e-14,69.2314,-130) rot=(0,0,1;0rad)
  LinkedObject = -> Body016
  Placement = pos=(6.69e-14,69.2314,-130) rot=(0,0,1;0rad)
  SolverId = Asm4EE
  expr: Placement = Body_Pedestral_Connector.Placement * Pedestral_Connector.Placement * AttachmentOffset * Pedestral_Top.Placement ^ -1
FEATURE [Mesh::Feature] Mesh013  label="Body_circuit_house (Meshed)"
FEATURE [App::DocumentObjectGroup] Group001  label="Group_Meshes"
  Group = -> [Mesh010,Mesh002,Mesh003,Mesh006,Mesh,Mesh008,Mesh009,Mesh011,Mesh013]
FEATURE [App::Point] Origin116  label="Origin"
  Role = Origin
FEATURE [App::Point] Origin117  label="Origin"
  Role = Origin
FEATURE [App::Point] Origin118  label="Origin"
  Role = Origin
FEATURE [App::Point] Origin119  label="Origin"
  Role = Origin
FEATURE [App::Point] Origin120  label="Origin"
  Role = Origin
FEATURE [App::Point] Origin121  label="Origin"
  Role = Origin
FEATURE [App::Point] Origin122  label="Origin"
  Role = Origin
FEATURE [App::Point] Origin123  label="Origin"
  Role = Origin
FEATURE [App::Point] Origin124  label="Origin"
  Role = Origin
FEATURE [App::Point] Origin125  label="Origin"
  Role = Origin
FEATURE [App::Point] Origin126  label="Origin"
  Role = Origin
FEATURE [App::Point] Origin127  label="Origin"
  Role = Origin
FEATURE [App::Point] Origin128  label="Origin"
  Role = Origin
FEATURE [App::Point] Origin129  label="Origin"
  Role = Origin
FEATURE [App::Point] Origin130  label="Origin"
  Role = Origin
FEATURE [App::Point] Origin131  label="Origin"
  Role = Origin
FEATURE [App::Point] Origin132  label="Origin"
  Role = Origin
FEATURE [App::Point] Origin133  label="Origin"
  Role = Origin
FEATURE [App::Point] Origin134  label="Origin"
  Role = Origin
FEATURE [App::Point] Origin135  label="Origin"
  Role = Origin
FEATURE [App::Point] Origin136  label="Origin"
  Role = Origin
FEATURE [App::Point] Origin137  label="Origin"
  Role = Origin
FEATURE [App::Point] Origin138  label="Origin"
  Role = Origin
FEATURE [App::Point] Origin139  label="Origin"
  Role = Origin
FEATURE [App::Point] Origin140  label="Origin"
  Role = Origin
FEATURE [App::Point] Origin141  label="Origin"
  Role = Origin
FEATURE [App::Point] Origin142  label="Origin"
  Role = Origin
FEATURE [App::Point] Origin143  label="Origin"
  Role = Origin
FEATURE [App::Point] Origin144  label="Origin"
  Role = Origin
FEATURE [App::Point] Origin145  label="Origin"
  Role = Origin
FEATURE [App::Point] Origin146  label="Origin"
  Role = Origin
FEATURE [App::Point] Origin147  label="Origin"
  Role = Origin
FEATURE [App::Point] Origin148  label="Origin"
  Role = Origin
FEATURE [App::Point] Origin149  label="Origin"
  Role = Origin
FEATURE [App::Point] Origin150  label="Origin"
  Role = Origin
FEATURE [App::Point] Origin151  label="Origin"
  Role = Origin
FEATURE [App::Point] Origin152  label="Origin"
  Role = Origin
FEATURE [App::Point] Origin153  label="Origin"
  Role = Origin
FEATURE [App::Point] Origin154  label="Origin"
  Role = Origin
FEATURE [App::Point] Origin155  label="Origin"
  Role = Origin
FEATURE [App::Point] Origin156  label="Origin"
  Role = Origin
FEATURE [App::Point] Origin157  label="Origin"
  Role = Origin
FEATURE [App::Point] Origin158  label="Origin"
  Role = Origin
FEATURE [App::Point] Origin159  label="Origin"
  Role = Origin
FEATURE [App::Point] Origin160  label="Origin"
  Role = Origin
FEATURE [App::Point] Origin161  label="Origin"
  Role = Origin
FEATURE [App::Point] Origin162  label="Origin"
  Role = Origin
FEATURE [App::Point] Origin163  label="Origin"
  Role = Origin
FEATURE [App::Point] Origin164  label="Origin"
  Role = Origin
FEATURE [App::Point] Origin165  label="Origin"
  Role = Origin
FEATURE [App::Point] Origin166  label="Origin"
  Role = Origin
FEATURE [App::Point] Origin167  label="Origin"
  Role = Origin
FEATURE [App::Point] Origin168  label="Origin"
  Role = Origin
FEATURE [App::Point] Origin169  label="Origin"
  Role = Origin
FEATURE [App::Point] Origin170  label="Origin"
  Role = Origin
FEATURE [App::Point] Origin171  label="Origin"
  Role = Origin
FEATURE [App::Point] Origin172  label="Origin"
  Role = Origin
FEATURE [App::Point] Origin173  label="Origin"
  Role = Origin
FEATURE [App::Point] Origin174  label="Origin"
  Role = Origin
FEATURE [App::Point] Origin175  label="Origin"
  Role = Origin
FEATURE [App::Point] Origin176  label="Origin"
  Role = Origin
FEATURE [App::Point] Origin177  label="Origin"
  Role = Origin
FEATURE [App::Point] Origin178  label="Origin"
  Role = Origin
FEATURE [App::Point] Origin179  label="Origin"
  Role = Origin
FEATURE [App::Point] Origin180  label="Origin"
  Role = Origin
FEATURE [App::Point] Origin181  label="Origin"
  Role = Origin
FEATURE [App::Point] Origin182  label="Origin"
  Role = Origin
FEATURE [App::Point] Origin183  label="Origin"
  Role = Origin
FEATURE [App::Point] Origin184  label="Origin"
  Role = Origin
FEATURE [App::Point] Origin185  label="Origin"
  Role = Origin
FEATURE [App::Point] Origin186  label="Origin"
  Role = Origin
FEATURE [App::Point] Origin187  label="Origin"
  Role = Origin
FEATURE [App::Point] Origin188  label="Origin"
  Role = Origin
FEATURE [App::Point] Origin189  label="Origin"
  Role = Origin
FEATURE [App::Point] Origin190  label="Origin"
  Role = Origin
FEATURE [App::Point] Origin191  label="Origin"
  Role = Origin
FEATURE [App::Point] Origin192  label="Origin"
  Role = Origin
FEATURE [App::Point] Origin193  label="Origin"
  Role = Origin
FEATURE [App::Point] Origin194  label="Origin"
  Role = Origin
FEATURE [App::Point] Origin195  label="Origin"
  Role = Origin
FEATURE [App::Point] Origin196  label="Origin"
  Role = Origin
FEATURE [App::Point] Origin197  label="Origin"
  Role = Origin
FEATURE [App::Point] Origin198  label="Origin"
  Role = Origin
FEATURE [App::Point] Origin199  label="Origin"
  Role = Origin
FEATURE [App::Point] Origin200  label="Origin"
  Role = Origin
FEATURE [App::Point] Origin201  label="Origin"
  Role = Origin
FEATURE [App::Point] Origin202  label="Origin"
  Role = Origin
FEATURE [App::Point] Origin203  label="Origin"
  Role = Origin
FEATURE [App::Point] Origin204  label="Origin"
  Role = Origin
FEATURE [App::Point] Origin205  label="Origin"
  Role = Origin
FEATURE [App::Point] Origin206  label="Origin"
  Role = Origin
FEATURE [App::Point] Origin207  label="Origin"
  Role = Origin
FEATURE [App::Point] Origin208  label="Origin"
  Role = Origin
FEATURE [App::Point] Origin209  label="Origin"
  Role = Origin
FEATURE [App::Point] Origin210  label="Origin"
  Role = Origin
FEATURE [App::Point] Origin211  label="Origin"
  Role = Origin
FEATURE [App::Point] Origin212  label="Origin"
  Role = Origin
FEATURE [App::Point] Origin213  label="Origin"
  Role = Origin
FEATURE [App::Point] Origin214  label="Origin"
  Role = Origin
FEATURE [App::Point] Origin215  label="Origin"
  Role = Origin
FEATURE [App::Point] Origin216  label="Origin"
  Role = Origin
FEATURE [App::Point] Origin217  label="Origin"
  Role = Origin
FEATURE [App::Point] Origin218  label="Origin"
  Role = Origin
FEATURE [App::Point] Origin219  label="Origin"
  Role = Origin
FEATURE [App::Point] Origin220  label="Origin"
  Role = Origin
FEATURE [App::Point] Origin221  label="Origin"
  Role = Origin
FEATURE [App::Point] Origin222  label="Origin"
  Role = Origin
FEATURE [App::Point] Origin223  label="Origin"
  Role = Origin
FEATURE [App::Point] Origin224  label="Origin"
  Role = Origin
FEATURE [App::Point] Origin225  label="Origin"
  Role = Origin
FEATURE [App::Point] Origin227  label="Origin"
  Role = Origin
FEATURE [App::Point] Origin229
  Role = Origin
FEATURE [PartDesign::CoordinateSystem] LCS_Origin001
  AttacherType = Attacher::AttachEngine3D
  AttachmentSupport = -> [X_Axis116]
  MapMode = 2
FEATURE [Sketcher::SketchObject] Sketch068
  ArcFitTolerance = 1e-06
  AttachmentSupport = -> [Origin228]
  ExternalTypes = [0]
  FullyConstrained = true
  MakeInternals = false
  MapMode = 5
  _ExternalGeoVersion = 1
  sketch-geometry (1):
    g0: Circle CenterX=0 CenterY=0 CenterZ=0 NormalX=0 NormalY=0 NormalZ=1 AngleXU=0 Radius=4.2
  constraints (2):
    c: Coincident(g0,g-1)
    c: Diameter(g0) = 8.4
FEATURE [PartDesign::Pad] Pad042
  Direction = (0,0,1)
  Length = 30
  Length2 = 10
  Profile = -> Sketch068
  ReferenceAxis = -> Sketch068 [N_Axis]
  Refine = true
  SideType = 0
  Suppressed = false
  Type = 0
  Type2 = 0
FEATURE [PartDesign::Hole] Hole
  BaseFeature = -> Pad042
  BaseProfileType = 7
  CustomThreadClearance = 0
  Depth = 30
  DepthType = 0
  Diameter = 4
  DrillForDepth = false
  DrillPoint = 0
  DrillPointAngle = 118
  HoleCutCountersinkAngle = 90
  HoleCutCustomValues = false
  HoleCutDepth = 0
  HoleCutDiameter = 0
  HoleCutType = 0
  ModelThread = false
  Profile = -> Pad042 [Face3]
  Refine = true
  Suppressed = false
  Tapered = false
  TaperedAngle = 90
  ThreadClass = 0
  ThreadDepth = 30
  ThreadDepthType = 0
  ThreadDiameter = 4
  ThreadDirection = 0
  ThreadFit = 0
  ThreadSize = 0
  ThreadType = 0
  Threaded = false
  UseCustomThreadClearance = false
FEATURE [PartDesign::Body] Body_Cylinders
  AllowCompound = true
  Group = -> [LCS_Origin001,Sketch068,Pad042,Hole]
  Origin = -> Origin228
  Tip = -> Hole
FEATURE [App::Link] Body_Cylinders001
  AttachedBy = #LCS_Origin001
  AttachedTo = Body_Trepied#Trepied_Bottom
  LinkPlacement = pos=(-27.5,116.863,-26) rot=(0,0,-0.999977;4e-06rad)
  LinkedObject = -> Body_Cylinders
  Placement = pos=(-27.5,116.863,-26) rot=(0,0,-0.999977;4e-06rad)
  SolverId = Asm4EE
  expr: Placement = Body_Trepied.Placement * Trepied_Bottom.Placement * AttachmentOffset * LCS_Origin001.Placement ^ -1
FEATURE [App::Link] Body_Cylinders002
  AttachedBy = #LCS_Origin001
  AttachedTo = Body_Trepied#Trepied_Bottom
  AttachmentOffset = pos=(55,0,0) rot=(0,0,1;0rad)
  LinkPlacement = pos=(27.5,116.863,-26) rot=(0,0,-0.999977;4e-06rad)
  LinkedObject = -> Body_Cylinders
  Placement = pos=(27.5,116.863,-26) rot=(0,0,-0.999977;4e-06rad)
  SolverId = Asm4EE
  expr: Placement = Body_Trepied.Placement * Trepied_Bottom.Placement * AttachmentOffset * LCS_Origin001.Placement ^ -1
FEATURE [Sketcher::SketchObject] Sketch069
  ArcFitTolerance = 1e-06
  AttachmentSupport = -> [XY_Plane117]
  ExternalTypes = [0]
  FullyConstrained = true
  MakeInternals = false
  MapMode = 5
  _ExternalGeoVersion = 0
  sketch-geometry (23):
    g0: LineSegment StartX=-48 StartY=31 StartZ=0 EndX=-48 EndY=-31 EndZ=0
    g1: LineSegment StartX=-48 StartY=-31 StartZ=0 EndX=48 EndY=-31 EndZ=0
    g2: LineSegment StartX=48 StartY=-31 StartZ=0 EndX=48 EndY=31 EndZ=0
    g3: LineSegment [constr] StartX=48 StartY=31 StartZ=0 EndX=-48 EndY=31 EndZ=0
    g4: LineSegment StartX=-45 StartY=28 StartZ=0 EndX=-45 EndY=6 EndZ=0
    g5: LineSegment StartX=-45 StartY=6 StartZ=0 EndX=45 EndY=6 EndZ=0
    g6: LineSegment StartX=45 StartY=6 StartZ=0 EndX=45 EndY=28 EndZ=0
    g7: LineSegment StartX=45 StartY=28 StartZ=0 EndX=-45 EndY=28 EndZ=0
    g8: LineSegment StartX=-45 StartY=-6 StartZ=0 EndX=-45 EndY=-28 EndZ=0
    g9: LineSegment StartX=-45 StartY=-28 StartZ=0 EndX=45 EndY=-28 EndZ=0
    g10: LineSegment StartX=45 StartY=-28 StartZ=0 EndX=45 EndY=-6 EndZ=0
    g11: LineSegment StartX=45 StartY=-6 StartZ=0 EndX=-45 EndY=-6 EndZ=0
    g12: Circle CenterX=-36.85 CenterY=0 CenterZ=0 NormalX=0 NormalY=0 NormalZ=1 AngleXU=0 Radius=1.8
    g13: Circle CenterX=36.85 CenterY=0 CenterZ=0 NormalX=0 NormalY=0 NormalZ=1 AngleXU=0 Radius=1.8
    g14: ArcOfCircle CenterX=-27.5 CenterY=38.25 CenterZ=0 NormalX=0 NormalY=0 NormalZ=1 AngleXU=0 Radius=7.25 StartAngle=1.5708 EndAngle=4.71239
    g15: ArcOfCircle CenterX=27.5 CenterY=38.25 CenterZ=0 NormalX=0 NormalY=0 NormalZ=1 AngleXU=0 Radius=7.25 StartAngle=4.71239 EndAngle=7.85398
    g16: LineSegment StartX=-27.5 StartY=45.5 StartZ=0 EndX=27.5 EndY=45.5 EndZ=0
    g17: LineSegment [constr] StartX=-27.5 StartY=31 StartZ=0 EndX=27.5 EndY=31 EndZ=0
    g18: Circle CenterX=-27.5 CenterY=38.25 CenterZ=0 NormalX=0 NormalY=0 NormalZ=1 AngleXU=0 Radius=2.3
    g19: Circle CenterX=27.5 CenterY=38.25 CenterZ=0 NormalX=0 NormalY=0 NormalZ=1 AngleXU=0 Radius=2.3
    g20: Circle CenterX=0 CenterY=38.25 CenterZ=0 NormalX=0 NormalY=0 NormalZ=1 AngleXU=0 Radius=5.3
    g21: LineSegment StartX=-48 StartY=31 StartZ=0 EndX=-27.5 EndY=31 EndZ=0
    g22: LineSegment StartX=48 StartY=31 StartZ=0 EndX=27.5 EndY=31 EndZ=0
  constraints (58):
    c: Coincident(g0,g1)
    c: Coincident(g1,g2)
    c: Coincident(g2,g3)
    c: Coincident(g3,g0)
    c: Vertical(g0)
    c: Vertical(g2)
    c: Horizontal(g1)
    c: Horizontal(g3)
    c: Symmetric(g0,g1,g-1)
    c: DistanceX(g3,g3) = 96
    c: DistanceY(g2,g2) = 62
    c: Coincident(g4,g5)
    c: Coincident(g5,g6)
    c: Coincident(g6,g7)
    c: Coincident(g7,g4)
    c: Vertical(g4)
    c: Vertical(g6)
    c: Horizontal(g5)
    c: Horizontal(g7)
    c: Coincident(g8,g9)
    c: Coincident(g9,g10)
    c: Coincident(g10,g11)
    c: Coincident(g11,g8)
    c: Vertical(g8)
    c: Vertical(g10)
    c: Horizontal(g9)
    c: Horizontal(g11)
    c: Symmetric(g8,g4,g-1)
    c: Equal(g4,g8)
    c: Equal(g5,g11)
    c: DistanceX(g0,g4) = 3
    c: DistanceX(g6,g2) = 3
    c: DistanceY(g1,g9) = 3
    c: DistanceY(g10,g5) = 12
    c: PointOnObject(g12,g-1)
    c: Symmetric(g12,g13,g-2)
    c: Equal(g12,g13)
    c: DistanceX(g12,g13) = 73.7
    c: Diameter(g12) = 3.6
    c: Tangent(g14,g16) = 1.5708
    c: Tangent(g14,g17) = -1.5708
    c: Tangent(g15,g16) = 1.5708
    c: Tangent(g15,g17) = -1.5708
    c: Equal(g14,g15)
    c: Symmetric(g14,g15,g-2)
    c: Coincident(g18,g14)
    c: Coincident(g19,g15)
    c: PointOnObject(g20,g-2)
    c: Equal(g18,g19)
    c: Diameter(g20) = 10.6
    c: DistanceX(g16,g16) = 55
    c: DistanceY(g20,g15) = 0
    c: Diameter(g14) = 14.5
    c: Diameter(g18) = 4.6
    c: Coincident(g21,g0)
    c: Coincident(g21,g14)
    c: Coincident(g22,g2)
    c: Tangent(g22,g15) = 1.5708
FEATURE [PartDesign::Pad] Pad043
  Direction = (0,0,1)
  Length = 10
  Length2 = 10
  Profile = -> Sketch069
  ReferenceAxis = -> Sketch069 [N_Axis]
  Refine = true
  SideType = 0
  Suppressed = false
  Type = 0
  Type2 = 0
FEATURE [Sketcher::SketchObject] Sketch070
  ArcFitTolerance = 1e-06
  AttachmentSupport = -> [Pad043]
  ExternalGeometry = -> [Pad043]
  ExternalTypes = [0]
  FullyConstrained = true
  MakeInternals = false
  MapMode = 5
  Placement = pos=(0,0,10) rot=(0,0,1;0rad)
  _ExternalGeoVersion = 0
  sketch-geometry (4):
    g0: LineSegment StartX=-45 StartY=6 StartZ=0 EndX=-45 EndY=-6 EndZ=0
    g1: LineSegment StartX=-45 StartY=-6 StartZ=0 EndX=45 EndY=-6 EndZ=0
    g2: LineSegment StartX=45 StartY=-6 StartZ=0 EndX=45 EndY=6 EndZ=0
    g3: LineSegment StartX=45 StartY=6 StartZ=0 EndX=-45 EndY=6 EndZ=0
  constraints (10):
    c: Coincident(g0,g1)
    c: Coincident(g1,g2)
    c: Coincident(g2,g3)
    c: Coincident(g3,g0)
    c: Vertical(g0)
    c: Vertical(g2)
    c: Horizontal(g1)
    c: Horizontal(g3)
    c: Coincident(g1,g-4)
    c: Coincident(g0,g-3)
FEATURE [PartDesign::Pocket] Pocket021
  BaseFeature = -> Pad043
  Direction = (0,0,-1)
  Length = 7
  Length2 = 5
  Profile = -> Sketch070
  ReferenceAxis = -> Sketch070 [N_Axis]
  Refine = true
  SideType = 0
  Suppressed = false
  Type = 0
  Type2 = 0
FEATURE [Sketcher::SketchObject] Sketch071
  ArcFitTolerance = 1e-06
  AttachmentSupport = -> [Pocket021]
  ExternalGeometry = -> [Pocket021]
  ExternalTypes = [0]
  FullyConstrained = true
  MakeInternals = false
  MapMode = 5
  Placement = pos=(0,0,10) rot=(0,0,1;0rad)
  _ExternalGeoVersion = 0
  sketch-geometry (4):
    g0: LineSegment StartX=-35 StartY=45.5 StartZ=0 EndX=-35 EndY=31 EndZ=0
    g1: LineSegment StartX=-35 StartY=31 StartZ=0 EndX=35 EndY=31 EndZ=0
    g2: LineSegment StartX=35 StartY=31 StartZ=0 EndX=35 EndY=45.5 EndZ=0
    g3: LineSegment StartX=35 StartY=45.5 StartZ=0 EndX=-35 EndY=45.5 EndZ=0
  constraints (12):
    c: Coincident(g0,g1)
    c: Coincident(g1,g2)
    c: Coincident(g2,g3)
    c: Coincident(g3,g0)
    c: Vertical(g0)
    c: Vertical(g2)
    c: Horizontal(g1)
    c: Horizontal(g3)
    c: PointOnObject(g-4,g3)
    c: PointOnObject(g-3,g1)
    c: DistanceX(g0,g-1) = 35
    c: DistanceX(g-1,g2) = 35
FEATURE [PartDesign::Pocket] Pocket022
  BaseFeature = -> Pocket021
  Direction = (0,0,-1)
  Length = 5
  Length2 = 5
  Profile = -> Sketch071
  ReferenceAxis = -> Sketch071 [N_Axis]
  Refine = true
  SideType = 0
  Suppressed = false
  Type = 0
  Type2 = 0
FEATURE [App::Point] Origin230  label="Origin231"
  Role = Origin
FEATURE [PartDesign::CoordinateSystem] LCS_Circuit_Housing
  AttacherType = Attacher::AttachEngine3D
  AttachmentSupport = -> [Pocket022]
  MapMode = 45
  Placement = pos=(-27.5,38.25,5) rot=(0,0,1;0rad)
FEATURE [App::Link] Body_circuit_housing  label="Body_circuit_housing001"
  AttachedBy = #LCS_Circuit_Housing
  AttachedTo = Body_Trepied#Trepied_Bottom
  AttachmentOffset = pos=(0,0,35) rot=(0,0,1;0rad)
  LinkPlacement = pos=(-0.000138669,78.6127,4) rot=(0,0,-0.999977;4e-06rad)
  LinkedObject = -> Body019
  Placement = pos=(-0.000138669,78.6127,4) rot=(0,0,-0.999977;4e-06rad)
  SolverId = Asm4EE
  expr: Placement = Body_Trepied.Placement * Trepied_Bottom.Placement * AttachmentOffset * LCS_Circuit_Housing.Placement ^ -1
FEATURE [App::Point] Origin233  label="Origin234"
  Role = Origin
FEATURE [Part::Feature] Part__Feature161  label="C_Disc_D5.0mm_W2.5mm_P5.00mm001"
  Placement = pos=(51.5,15,1.595) rot=(0,0,1;3.14159rad)
  shape: bbox 5.5 x 2.5 x 7.1 mm, 10 faces (baked)
FEATURE [Part::Feature] Part__Feature162  label="R_Axial_DIN0207_L6.3mm_D2.5mm_P7.62mm_Horizontal003"
  Placement = pos=(44,19.5,1.595) rot=(0,0,1;0rad)
  shape: bbox 8.418 x 2.706 x 5.603 mm, 15 faces (baked)
FEATURE [Part::Feature] Part__Feature002  label="R_Axial_DIN0207_L6.3mm_D2.5mm_P7.62mm_Horizontal004"
  Placement = pos=(51.5,32.62,1.595) rot=(0,0,-1;1.5708rad)
  shape: bbox 2.706 x 8.418 x 5.603 mm, 15 faces (baked)
FEATURE [Part::Feature] Part__Feature163  label="PinHeader_1x08_P2.54mm_Vertical001"
  Placement = pos=(3.76,29,1.595) rot=(0,0,1;1.5708rad)
  shape: bbox 20.32 x 2.54 x 11.54 mm, 196 faces (baked)
FEATURE [Part::Feature] Part__Feature164  label="TerminalBlock_Phoenix_MKDS-1,5-2_1x02_P5.00mm_Horizontal001"
  Placement = pos=(68.5,25,1.595) rot=(0,0,1;2.44346rad)
  shape: bbox 14.18 x 13.94 x 17.3 mm, 89 faces (baked)
FEATURE [Part::Feature] Part__Feature165  label="PinHeader_1x04_P2.54mm_Vertical001"
  Placement = pos=(30.04,-10,1.595) rot=(0,0,-1;1.5708rad)
  shape: bbox 10.16 x 2.54 x 11.54 mm, 100 faces (baked)
FEATURE [Part::Feature] Part__Feature166  label="TO-92L_Inline001"
  Placement = pos=(54.2,-3.05,1.595) rot=(0,0,1;3.14159rad)
  shape: bbox 4.9 x 3.9 x 12.95 mm, 19 faces (baked)
FEATURE [Part::Feature] Part__Feature167  label="R_Axial_DIN0207_L6.3mm_D2.5mm_P7.62mm_Horizontal005"
  Placement = pos=(55.5,7.5,1.595) rot=(0,0,1;3.14159rad)
  shape: bbox 8.418 x 2.706 x 5.603 mm, 15 faces (baked)
FEATURE [Part::Feature] Part__Feature168  label="Buzzer_12x9.5RM7.001"
  Placement = pos=(65.5,-12.8,1.595) rot=(0,0,1;1.5708rad)
  shape: bbox 12.99 x 12.99 x 12.53 mm, 13 faces (baked)
FEATURE [Part::Feature] Part__Feature169  label="kiCAD_PCB"
  shape: bbox 88 x 51.5 x 1.51 mm, 43 faces (baked)
FEATURE [PartDesign::CoordinateSystem] LCS_Arduino
  AttacherType = Attacher::AttachEngine3D
  AttachmentOffset = pos=(0,0,0) rot=(-0.57735,0.57735,0.57735;2.0944rad)
  AttachmentSupport = -> [Part__Feature169]
  MapMode = 7
  Placement = pos=(0,0,1.51) rot=(0,0,1;0rad)
FEATURE [PartDesign::CoordinateSystem] LCS_Hole
  AttacherType = Attacher::AttachEngine3D
  AttachmentOffset = pos=(0,0,0) rot=(0,1,0;3.14159rad)
  AttachmentSupport = -> [Part__Feature169]
  MapMode = 11
  Placement = pos=(-4,8.25,1.51) rot=(0,0,1;0rad)
FEATURE [App::Part] kiCad_Board_1  label="kiCad_Board"
  Group = -> [Part__Feature161,Part__Feature162,Part__Feature002,Part__Feature163,Part__Feature164,Part__Feature165,Part__Feature166,Part__Feature167,Part__Feature168,LCS_Arduino,LCS_Hole,Part__Feature169]
  Origin = -> Origin232
FEATURE [App::Link] kiCad_Board  label="kiCad_Board001"
  AttachedBy = #LCS_Arduino
  AttachedTo = Body_circuit_housing#LCS_Circuit_Housing
  AttachmentOffset = pos=(-5,-47,7) rot=(0,0,1;0rad)
  LinkPlacement = pos=(-32.5002,69.8628,14.49) rot=(0,0,-0.999953;4e-06rad)
  LinkedObject = -> kiCad_Board_1
  Placement = pos=(-32.5002,69.8628,14.49) rot=(0,0,-0.999953;4e-06rad)
  SolverId = Asm4EE
  expr: Placement = Body_circuit_housing.Placement * LCS_Circuit_Housing.Placement * AttachmentOffset * LCS_Arduino.Placement ^ -1
FEATURE [App::Link] PCB001
  AttachedBy = #Nano_USB_Left
  AttachedTo = kiCad_Board#LCS_Arduino
  AttachmentOffset = pos=(1,1,2) rot=(0,0,1;4.71239rad)
  LinkPlacement = pos=(-32.7702,69.5928,18) rot=(0,0,0.999971;6.28318rad)
  LinkedObject = -> PCB
  Placement = pos=(-32.7702,69.5928,18) rot=(0,0,0.999971;6.28318rad)
  SolverId = Asm4EE
  expr: Placement = kiCad_Board.Placement * LCS_Arduino.Placement * AttachmentOffset * Nano_USB_Left.Placement ^ -1
FEATURE [Part::FeaturePython] Screw028  label="M4x16-Screw002"  # WARN: FeaturePython — macro-defined, semantics opaque (R4)
  BaseObject = -> Assembly [Body_Cylinders002.Hole.Edge5]
  Diameter = 2
  Invert = false
  LeftHanded = false
  Length = 5
  LengthCustom = 16
  MatchOuter = false
  Offset = 6
  OffsetAngle = 0
  Placement = pos=(27.5,116.863,10) rot=(0,0,1;0rad)
  Thread = false
  Type = 86
FEATURE [Part::FeaturePython] Screw029  label="M4x16-Screw"  # WARN: FeaturePython — macro-defined, semantics opaque (R4)
  BaseObject = -> Assembly [Body_Cylinders001.Hole.Edge5]
  Diameter = 2
  Invert = false
  LeftHanded = false
  Length = 5
  LengthCustom = 16
  MatchOuter = false
  Offset = 6
  OffsetAngle = 0
  Placement = pos=(-27.5,116.863,10) rot=(0,0,1;0rad)
  Thread = false
  Type = 86
FEATURE [Part::FeaturePython] Screw030  label="M4x8-Screw4811"  # WARN: FeaturePython — macro-defined, semantics opaque (R4)
  BaseObject = -> Assembly [Body_Cylinders002.Hole.Edge4]
  Diameter = 2
  Invert = true
  LeftHanded = false
  Length = 1
  LengthCustom = 8
  MatchOuter = false
  Offset = 4
  OffsetAngle = 0
  Placement = pos=(27.5,116.863,-30) rot=(0.686843,0.726806,0;3.14159rad)
  Thread = false
  Type = 86
FEATURE [Part::FeaturePython] Screw031  label="M4x8-Screw4812"  # WARN: FeaturePython — macro-defined, semantics opaque (R4)
  BaseObject = -> Assembly [Body_Cylinders001.Hole.Edge4]
  Diameter = 2
  Invert = true
  LeftHanded = false
  Length = 1
  LengthCustom = 8
  MatchOuter = false
  Offset = 4
  OffsetAngle = 0
  Placement = pos=(-27.5,116.863,-30) rot=(0.686843,0.726806,0;3.14159rad)
  Thread = false
  Type = 86
FEATURE [Part::FeaturePython] Screw032  label="M3x16-Screw"  # WARN: FeaturePython — macro-defined, semantics opaque (R4)
  BaseObject = -> Assembly [kiCad_Board.Part__Feature169.Edge63]
  Diameter = 1
  Invert = true
  LeftHanded = false
  Length = 5
  LengthCustom = 16
  MatchOuter = false
  OffsetAngle = 0
  Placement = pos=(-36.5001,78.1128,16) rot=(0,0,1;0rad)
  Thread = false
  Type = 85
FEATURE [Part::FeaturePython] Screw033  label="M3x16-Screw002"  # WARN: FeaturePython — macro-defined, semantics opaque (R4)
  BaseObject = -> Assembly [kiCad_Board.Part__Feature169.Edge81]
  Diameter = 1
  Invert = true
  LeftHanded = false
  Length = 5
  LengthCustom = 16
  MatchOuter = false
  OffsetAngle = 0
  Placement = pos=(37.1999,78.1126,16) rot=(0,0,1;0rad)
  Thread = false
  Type = 85
FEATURE [Part::FeaturePython] Nut029  label="(M3.5)-Nut007"  # WARN: FeaturePython — macro-defined, semantics opaque (R4)
  BaseObject = -> Screw032 [Edge27]
  Diameter = 5
  Invert = false
  LeftHanded = false
  MatchOuter = false
  OffsetAngle = 0
  Placement = pos=(-36.5001,78.1128,0.3) rot=(0,0,1;0rad)
  Thread = false
  Type = 31
FEATURE [Part::FeaturePython] Nut030  label="(M3.5)-Nut008"  # WARN: FeaturePython — macro-defined, semantics opaque (R4)
  BaseObject = -> Screw033 [Edge27]
  Diameter = 5
  Invert = false
  LeftHanded = false
  MatchOuter = false
  OffsetAngle = 0
  Placement = pos=(37.1999,78.1126,0.3) rot=(0,0,1;0rad)
  Thread = false
  Type = 31
FEATURE [App::DocumentObjectGroup] Group  label="Group_Screws"
  Group = -> [Screw,Screw001,Screw002,Screw003,Screw004,Nut,Nut003,Screw006,Screw007,Screw008,Screw009,Screw010,Screw011,Screw012,Screw013,Screw014,Screw015,Nut004,Nut005,Nut006,Nut007,Nut008,Nut009,Nut010,Nut011,Nut012,Nut013,Nut014,Nut015,Screw016,Screw017,Screw018,Screw019,Screw020,Nut019,Nut020,Nut021,Screw021,Nut022,Nut028,Screw027,Screw026,Nut027,Screw028,Screw029,Screw030,Screw031,Screw032,Screw033,+2 more]
FEATURE [App::Point] Origin234  label="Origin235"
  Role = Origin
FEATURE [Sketcher::SketchObject] Sketch072
  ArcFitTolerance = 1e-06
  AttachmentSupport = -> [Origin235]
  ExternalTypes = [0]
  FullyConstrained = true
  MakeInternals = false
  MapMode = 5
  _ExternalGeoVersion = 1
  sketch-geometry (1):
    g0: Circle CenterX=0 CenterY=0 CenterZ=0 NormalX=0 NormalY=0 NormalZ=1 AngleXU=0 Radius=7.5
  constraints (2):
    c: Coincident(g0,g-1)
    c: Diameter(g0) = 15
FEATURE [PartDesign::Pad] Pad044
  Direction = (0,0,1)
  Length = 8
  Length2 = 10
  Profile = -> Sketch072
  ReferenceAxis = -> Sketch072 [N_Axis]
  Refine = true
  SideType = 0
  Suppressed = false
  Type = 0
  Type2 = 0
FEATURE [Sketcher::SketchObject] Sketch073
  ArcFitTolerance = 1e-06
  AttachmentSupport = -> [Pad044]
  ExternalTypes = [0]
  FullyConstrained = true
  MakeInternals = false
  MapMode = 5
  Placement = pos=(0,0,8) rot=(0,0,1;0rad)
  _ExternalGeoVersion = 1
  sketch-geometry (1):
    g0: Circle CenterX=0 CenterY=0 CenterZ=0 NormalX=0 NormalY=0 NormalZ=1 AngleXU=0 Radius=5
  constraints (2):
    c: Coincident(g0,g-1)
    c: Diameter(g0) = 10
FEATURE [PartDesign::Pad] Pad045
  BaseFeature = -> Pad044
  Direction = (0,0,1)
  Length = 5
  Length2 = 10
  Profile = -> Sketch073
  ReferenceAxis = -> Sketch073 [N_Axis]
  Refine = true
  SideType = 0
  Suppressed = false
  Type = 0
  Type2 = 0
FEATURE [Sketcher::SketchObject] Sketch074
  ArcFitTolerance = 1e-06
  AttachmentSupport = -> [Pad045]
  ExternalTypes = [0]
  FullyConstrained = true
  MakeInternals = false
  MapMode = 5
  Placement = pos=(0,0,0) rot=(1,0,0;3.14159rad)
  _ExternalGeoVersion = 1
  sketch-geometry (1):
    g0: Circle CenterX=0 CenterY=0 CenterZ=0 NormalX=0 NormalY=0 NormalZ=1 AngleXU=0 Radius=4.3
  constraints (2):
    c: Coincident(g0,g-1)
    c: Diameter(g0) = 8.6
FEATURE [PartDesign::Pad] Pad046
  BaseFeature = -> Pad045
  Direction = (0,0,-1)
  Length = 13
  Length2 = 10
  Profile = -> Sketch074
  ReferenceAxis = -> Sketch074 [N_Axis]
  Refine = true
  SideType = 0
  Suppressed = false
  Type = 0
  Type2 = 0
FEATURE [Sketcher::SketchObject] Sketch075
  ArcFitTolerance = 1e-06
  AttachmentSupport = -> [Pad046]
  ExternalTypes = [0]
  FullyConstrained = true
  MakeInternals = false
  MapMode = 5
  Placement = pos=(0,0,-13) rot=(1,0,0;3.14159rad)
  _ExternalGeoVersion = 1
  sketch-geometry (8):
    g0: LineSegment StartX=-2.2 StartY=2 StartZ=0 EndX=-2.2 EndY=-2 EndZ=0
    g1: LineSegment StartX=-2.2 StartY=-2 StartZ=0 EndX=-2 EndY=-2 EndZ=0
    g2: LineSegment StartX=-2 StartY=-2 StartZ=0 EndX=-2 EndY=2 EndZ=0
    g3: LineSegment StartX=-2 StartY=2 StartZ=0 EndX=-2.2 EndY=2 EndZ=0
    g4: LineSegment StartX=2 StartY=2 StartZ=0 EndX=2 EndY=-2 EndZ=0
    g5: LineSegment StartX=2 StartY=-2 StartZ=0 EndX=2.2 EndY=-2 EndZ=0
    g6: LineSegment StartX=2.2 StartY=-2 StartZ=0 EndX=2.2 EndY=2 EndZ=0
    g7: LineSegment StartX=2.2 StartY=2 StartZ=0 EndX=2 EndY=2 EndZ=0
  constraints (22):
    c: Coincident(g0,g1)
    c: Coincident(g1,g2)
    c: Coincident(g2,g3)
    c: Coincident(g3,g0)
    c: Vertical(g0)
    c: Vertical(g2)
    c: Horizontal(g1)
    c: Horizontal(g3)
    c: Coincident(g4,g5)
    c: Coincident(g5,g6)
    c: Coincident(g6,g7)
    c: Coincident(g7,g4)
    c: Vertical(g4)
    c: Horizontal(g5)
    c: Horizontal(g7)
    c: Symmetric(g6,g5,g-1)
    c: Symmetric(g2,g4,g-2)
    c: Equal(g2,g4)
    c: Equal(g3,g7)
    c: DistanceX(g3,g3) = 0.2
    c: DistanceY(g0,g0) = 4
    c: DistanceX(g1,g4) = 4
FEATURE [PartDesign::Pad] Pad047
  BaseFeature = -> Pad046
  Direction = (0,0,-1)
  Length = 8
  Length2 = 10
  Profile = -> Sketch075
  ReferenceAxis = -> Sketch075 [N_Axis]
  Refine = true
  SideType = 0
  Suppressed = false
  Type = 0
  Type2 = 0
FEATURE [Sketcher::SketchObject] Sketch076
  ArcFitTolerance = 1e-06
  AttachmentSupport = -> [Pad047]
  ExternalTypes = [0]
  FullyConstrained = true
  MakeInternals = false
  MapMode = 5
  Placement = pos=(2.2,0,0) rot=(0.57735,0.57735,0.57735;2.0944rad)
  _ExternalGeoVersion = 1
  sketch-geometry (1):
    g0: Circle CenterX=0 CenterY=-18 CenterZ=0 NormalX=0 NormalY=0 NormalZ=1 AngleXU=0 Radius=1
  constraints (3):
    c: PointOnObject(g0,g-2)
    c: Diameter(g0) = 2
    c: DistanceY(g0,g-1) = 18
FEATURE [PartDesign::Pocket] Pocket023
  BaseFeature = -> Pad047
  Direction = (-1,0,0)
  Length = 5
  Length2 = 5
  Profile = -> Sketch076
  ReferenceAxis = -> Sketch076 [N_Axis]
  Refine = true
  SideType = 0
  Suppressed = false
  Type = 1
  Type2 = 0
FEATURE [PartDesign::Fillet] Fillet011
  Base = -> Pocket023 [Edge35,Edge25,Edge30,Edge20]
  BaseFeature = -> Pocket023
  Radius = 6.5
  Refine = true
  SupportTransform = false
  Suppressed = false
  UseAllEdges = false
FEATURE [PartDesign::CoordinateSystem] LCS_Button
  AttacherType = Attacher::AttachEngine3D
  AttachmentSupport = -> [Fillet011]
  MapMode = 45
  Placement = pos=(3.05e-14,-1e-16,10) rot=(0,0,1;0rad)
FEATURE [PartDesign::Body] Body020  label="Body_Button_Round"
  AllowCompound = false
  Group = -> [Sketch072,Pad044,Sketch073,Pad045,Sketch074,Pad046,Sketch075,Pad047,Sketch076,Pocket023,Fillet011,LCS_Button]
  Origin = -> Origin235
  Tip = -> Fillet011
FEATURE [PartDesign::CoordinateSystem] LCS_Circuit_Button
  AttacherType = Attacher::AttachEngine3D
  AttachmentSupport = -> [Pocket022]
  MapMode = 45
  Placement = pos=(-4e-16,38.25,4.5869) rot=(0,0,1;1.5708rad)
FEATURE [PartDesign::Body] Body019  label="Body_circuit_housing"
  AllowCompound = false
  Group = -> [Sketch069,Pad043,Sketch070,Pocket021,Sketch071,Pocket022,LCS_Circuit_Housing,LCS_Circuit_Button]
  Origin = -> Origin231
  Tip = -> Pocket022
FEATURE [App::DocumentObjectGroup] Parts
  Group = -> [Body019,Body,Body003,Body004,Body005,Body002,Body001,Body006,Body007,PCB,Body014,Body015,Body016,Body017,main_Circuit_kicad_Circuit_1,Body_Cylinders,kiCad_Board_1,Body020]
FEATURE [App::Link] Body_Button_Round  label="Body_Button_Round001"
  AttachedBy = #LCS_Button
  AttachedTo = Body_circuit_housing#LCS_Circuit_Button
  AttachmentOffset = pos=(0,0,11) rot=(0,0,1;0rad)
  LinkPlacement = pos=(-1.81392e-10,116.863,9.5869) rot=(0,0,0.999977;1.57079rad)
  LinkedObject = -> Body020
  Placement = pos=(-1.81392e-10,116.863,9.5869) rot=(0,0,0.999977;1.57079rad)
  SolverId = Asm4EE
  expr: Placement = Body_circuit_housing.Placement * LCS_Circuit_Button.Placement * AttachmentOffset * LCS_Button.Placement ^ -1
FEATURE [App::Part] Assembly
  AssemblyType = Part::Link
  Description = Pendulum - 3D printing models
  Group = -> [LCS_Origin,Constraints,Variables,Configurations,Body_Support,Body_Bearing,Body_Rondelle,Body_Arm,Body_Motor,Body_ReactionWheel,Motor_Shaft,Body_MPU6050,Body_BearingLock,Body_Trepied,Body_Pedestral_Connector,Body_Pedestral,Body_Cylinders001,Body_Cylinders002,Body_circuit_housing,kiCad_Board,PCB001,Body_Button_Round]
  Origin = -> Origin
  Type = Assembly
